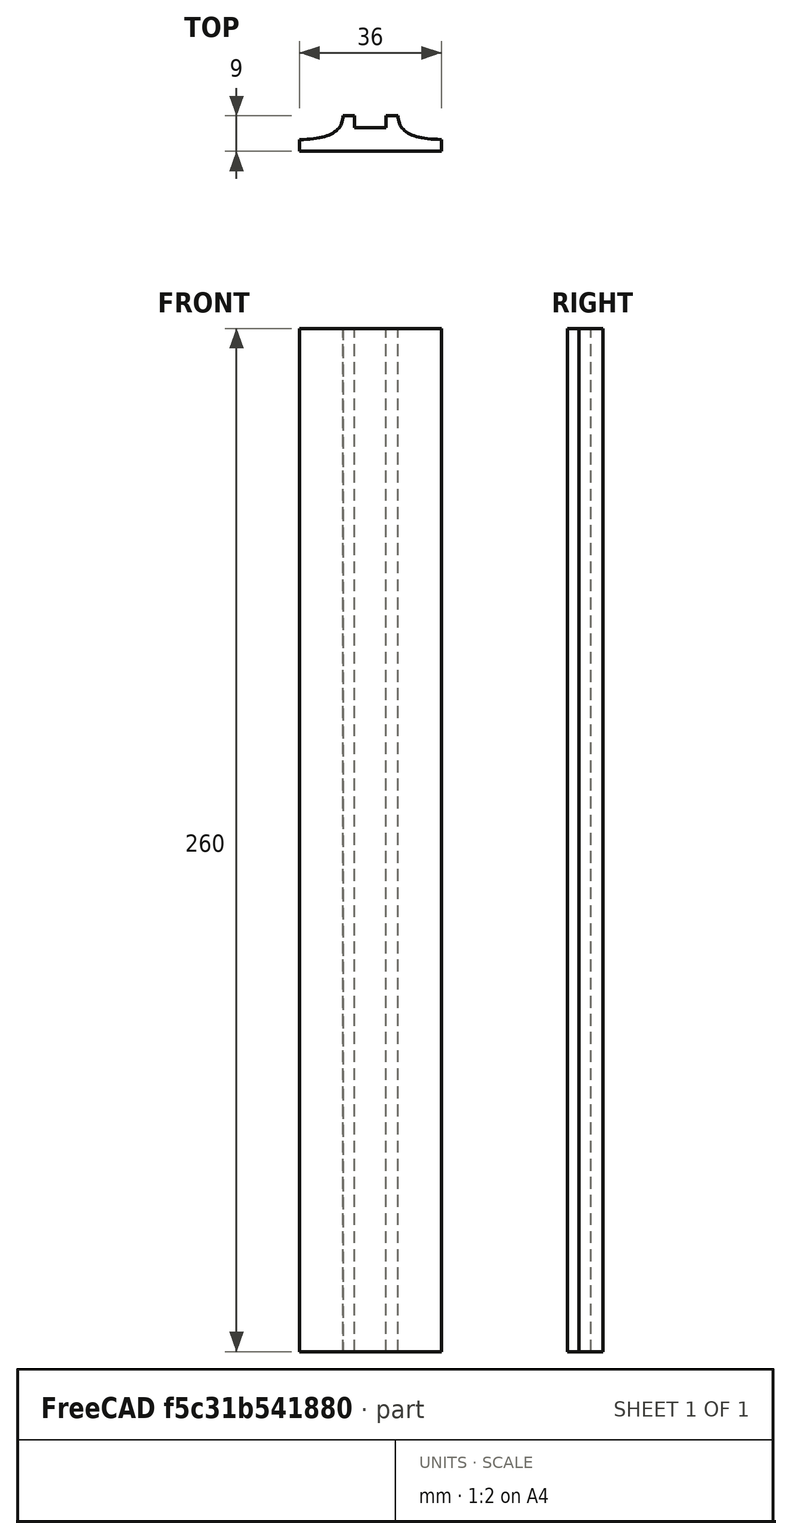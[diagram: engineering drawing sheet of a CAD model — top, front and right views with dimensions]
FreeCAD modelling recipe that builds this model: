
FCSTD DOCUMENT  (FreeCAD 0.19R0.19.2)
Label: laptopStand296.FCStd
License: All rights reserved
LicenseURL: http://en.wikipedia.org/wiki/All_rights_reserved
objects: Sketcher::SketchObject×10, Part::Extrusion×1
note: 11 computed .brp shape members not serialized (recipe doc carries the construction recipe); baked Part::Feature solids carry a one-line shape summary decoded from their .brp

FEATURE [Sketcher::SketchObject] Sketch001  label="legTop"
  FullyConstrained = true
  MapMode = 4
  Placement = pos=(0,0,0) rot=(0.57735,0.57735,0.57735;2.0944rad)
  sketch-geometry (41):
    g0: BSplineCurve PolesCount=3 KnotsCount=2 Degree=2 IsPeriodic=0
    g1: ArcOfCircle CenterX=73.1223 CenterY=-32.291 CenterZ=0 NormalX=0 NormalY=0 NormalZ=1 AngleXU=0 Radius=13 StartAngle=5.92268 EndAngle=9.06428
    g2: ArcOfCircle CenterX=66.7816 CenterY=-49.1439 CenterZ=0 NormalX=0 NormalY=0 NormalZ=1 AngleXU=0 Radius=13 StartAngle=2.78068 EndAngle=5.92131
    g3-g6: Circle x4 (B-spline internal-alignment scaffolding for g7; pole/knot coordinates omitted)
    g7: BSplineCurve PolesCount=4 KnotsCount=2 Degree=3 IsPeriodic=0
    g8: GeomPoint X=28.8094 Y=-19.0875 Z=0
    g9: GeomPoint X=47.0443 Y=-50.4712 Z=0
    g10: Circle CenterX=53.5586 CenterY=-23.2695 CenterZ=0 NormalX=0 NormalY=0 NormalZ=1 AngleXU=0 Radius=3.24518
    g11: LineSegment StartX=17.2232 StartY=-16.0875 StartZ=0 EndX=17.2232 EndY=-19.0875 EndZ=0
    g12: ArcOfCircle CenterX=17.2475 CenterY=-181.166 CenterZ=0 NormalX=0 NormalY=0 NormalZ=1 AngleXU=0 Radius=13 StartAngle=5.92268 EndAngle=7.49361
    g13: ArcOfCircle CenterX=29.5716 CenterY=-148.408 CenterZ=0 NormalX=0 NormalY=0 NormalZ=1 AngleXU=0 Radius=13 StartAngle=4.35228 EndAngle=5.92131
    g14: ArcOfCircle CenterX=35.8967 CenterY=-131.555 CenterZ=0 NormalX=0 NormalY=0 NormalZ=1 AngleXU=0 Radius=13 StartAngle=5.92268 EndAngle=7.49902
    g15: ArcOfCircle CenterX=48.1805 CenterY=-98.7782 CenterZ=0 NormalX=0 NormalY=0 NormalZ=1 AngleXU=0 Radius=13 StartAngle=4.34921 EndAngle=5.92131
    g16: ArcOfCircle CenterX=54.5183 CenterY=-81.9247 CenterZ=0 NormalX=0 NormalY=0 NormalZ=1 AngleXU=0 Radius=13 StartAngle=5.92268 EndAngle=8.70432
    g17: ArcOfCircle CenterX=20.184 CenterY=-217.506 CenterZ=0 NormalX=0 NormalY=0 NormalZ=1 AngleXU=0 Radius=3.81084 StartAngle=1.88136 EndAngle=6.80465
    g18: ArcOfCircle CenterX=36.3663 CenterY=-113.042 CenterZ=0 NormalX=0 NormalY=0 NormalZ=1 AngleXU=0 Radius=3.60555 StartAngle=0.230024 EndAngle=5.3372
    g19: LineSegment StartX=42.6867 StartY=-113.271 StartZ=0 EndX=43.5628 EndY=-110.929 EndZ=0
    g20: ArcOfCircle CenterX=17.7945 CenterY=-162.686 CenterZ=0 NormalX=0 NormalY=0 NormalZ=1 AngleXU=0 Radius=3.60555 StartAngle=0.230024 EndAngle=5.3372
    g21: ArcOfCircle CenterX=49.8795 CenterY=-62.6074 CenterZ=0 NormalX=0 NormalY=0 NormalZ=1 AngleXU=0 Radius=3.84187 StartAngle=4.46973 EndAngle=9.40343
    g22: LineSegment StartX=23.4884 StartY=-215.608 StartZ=0 EndX=94.6579 EndY=-26.1359 EndZ=0
    g23: LineSegment StartX=22.7134 StartY=-166.661 StartZ=0 EndX=21.8316 EndY=-169.001 EndZ=0
    g24: LineSegment StartX=48.061 StartY=-136.14 StartZ=0 EndX=41.7296 EndY=-153.01 EndZ=0
    g25: LineSegment StartX=24.1149 StartY=-162.915 StartZ=0 EndX=24.9906 EndY=-160.574 EndZ=0
    g26: LineSegment StartX=41.2852 StartY=-117.017 StartZ=0 EndX=40.4148 EndY=-119.365 EndZ=0
    g27: LineSegment StartX=48.9563 StartY=-66.3367 StartZ=0 EndX=44.7488 EndY=-73.3482 EndZ=0
    g28: LineSegment StartX=21.3051 StartY=-161.864 StartZ=0 EndX=24.1149 EndY=-162.915 EndZ=0
    g29: LineSegment StartX=19.9036 StartY=-165.61 StartZ=0 EndX=22.7134 EndY=-166.661 EndZ=0
    g30: LineSegment StartX=29.4118 StartY=-185.752 StartZ=0 EndX=19.0195 EndY=-213.878 EndZ=0
    g31: LineSegment StartX=39.8769 StartY=-112.22 StartZ=0 EndX=42.6867 EndY=-113.271 EndZ=0
    g32: LineSegment StartX=38.4753 StartY=-115.966 StartZ=0 EndX=41.2852 EndY=-117.017 EndZ=0
    g33: LineSegment StartX=60.3386 StartY=-103.381 StartZ=0 EndX=66.6827 EndY=-86.5104 EndZ=0
    g34: LineSegment StartX=41.085 StartY=-66.3176 StartZ=0 EndX=46.0385 EndY=-62.5254 EndZ=0
    g35: LineSegment StartX=47.0443 StartY=-50.4712 StartZ=0 EndX=41.085 EndY=-66.3176 EndZ=0
    g36: LineSegment StartX=17.2232 StartY=-16.0875 StartZ=0 EndX=117.223 EndY=-16.0875 EndZ=0
    g37: LineSegment StartX=28.8094 StartY=-19.0875 StartZ=0 EndX=17.2232 EndY=-19.0875 EndZ=0
    g38: LineSegment StartX=117.223 StartY=-16.0875 StartZ=0 EndX=117.223 EndY=-19.0875 EndZ=0
    g39: LineSegment StartX=85.2866 StartY=-36.8766 StartZ=0 EndX=78.9396 EndY=-53.7463 EndZ=0
    g40: LineSegment StartX=60.9579 StartY=-27.7053 StartZ=0 EndX=54.6191 EndY=-44.5532 EndZ=0
  constraints (65):
    c: Block(g0)
    c: Block(g1)
    c: Block(g2)
    c: Weight(g3) = 1
    c: Equal(g3,g4)
    c: Equal(g3,g5)
    c: Equal(g3,g6)
    c: InternalAlignment(g3-g6 -> g7) x4
    c: InternalAlignment(g8,g7)
    c: InternalAlignment(g9,g7)
    c: Block(g10)
    c: Block(g7)
    c: Vertical(g11)
    c: Block(g12)
    c: Block(g13)
    c: Block(g14)
    c: Block(g15)
    c: Block(g16)
    c: Block(g17)
    c: Block(g18)
    c: Block(g19)
    c: Block(g20)
    c: Block(g21)
    c: PointOnObject(g15,g19)
    c: Coincident(g22,g17)
    c: Coincident(g22,g0)
    c: Coincident(g23,g12)
    c: Coincident(g24,g14)
    c: Coincident(g24,g13)
    c: Coincident(g25,g13)
    c: Coincident(g26,g14)
    c: Coincident(g27,g21)
    c: Coincident(g27,g16)
    c: Coincident(g28,g20)
    c: Coincident(g28,g25)
    c: Coincident(g29,g20)
    c: Coincident(g29,g23)
    c: Block(g28)
    c: Block(g29)
    c: Coincident(g30,g12)
    c: Coincident(g30,g17)
    c: Coincident(g31,g18)
    c: Coincident(g31,g19)
    c: Coincident(g32,g18)
    c: Coincident(g32,g26)
    c: Block(g32)
    c: Coincident(g33,g15)
    c: Coincident(g33,g16)
    c: Coincident(g34,g21)
    c: Block(g34)
    c: Coincident(g35,g7)
    c: Coincident(g35,g34)
    c: Coincident(g36,g11)
    c: Horizontal(g36)
    c: Coincident(g37,g7)
    c: Coincident(g37,g11)
    c: Horizontal(g37)
    c: Coincident(g38,g36)
    c: Coincident(g38,g0)
    c: Vertical(g38)
    c: Block(g36)
    c: Coincident(g39,g1)
    c: Coincident(g39,g2)
    c: Coincident(g40,g1)
    c: Coincident(g40,g2)
FEATURE [Sketcher::SketchObject] Sketch002
  FullyConstrained = true
  sketch-geometry (20):
    g0: LineSegment StartX=-2.77179 StartY=-200.304 StartZ=0 EndX=5.22821 EndY=-200.304 EndZ=0
    g1: LineSegment StartX=5.22821 StartY=-200.304 StartZ=0 EndX=5.22821 EndY=-197.304 EndZ=0
    g2: LineSegment StartX=-2.77179 StartY=-200.304 StartZ=0 EndX=-2.77179 EndY=-197.304 EndZ=0
    g3: LineSegment StartX=5.22821 StartY=-197.304 StartZ=0 EndX=8.22821 EndY=-197.304 EndZ=0
    g4: LineSegment StartX=-2.77179 StartY=-197.304 StartZ=0 EndX=-5.77179 EndY=-197.304 EndZ=0
    g5: LineSegment StartX=19.2282 StartY=-203.304 StartZ=0 EndX=19.2282 EndY=-206.304 EndZ=0
    g6: LineSegment StartX=-16.7718 StartY=-203.304 StartZ=0 EndX=-16.7718 EndY=-206.304 EndZ=0
    g7: LineSegment StartX=-16.7718 StartY=-206.304 StartZ=0 EndX=19.2282 EndY=-206.304 EndZ=0
    g8: Circle CenterX=-16.7718 CenterY=-203.304 CenterZ=0 NormalX=0 NormalY=0 NormalZ=1 AngleXU=0 Radius=1
    g9: Circle CenterX=-5.77179 CenterY=-203.304 CenterZ=0 NormalX=0 NormalY=0 NormalZ=1 AngleXU=0 Radius=1
    g10: Circle CenterX=-5.77179 CenterY=-197.304 CenterZ=0 NormalX=0 NormalY=0 NormalZ=1 AngleXU=0 Radius=1
    g11: BSplineCurve PolesCount=3 KnotsCount=2 Degree=2 IsPeriodic=0
    g12: GeomPoint X=-16.7718 Y=-203.304 Z=0
    g13: GeomPoint X=-5.77179 Y=-197.304 Z=0
    g14: Circle CenterX=19.2282 CenterY=-203.304 CenterZ=0 NormalX=0 NormalY=0 NormalZ=1 AngleXU=0 Radius=1
    g15: Circle CenterX=8.22821 CenterY=-203.304 CenterZ=0 NormalX=0 NormalY=0 NormalZ=1 AngleXU=0 Radius=1
    g16: Circle CenterX=8.22821 CenterY=-197.304 CenterZ=0 NormalX=0 NormalY=0 NormalZ=1 AngleXU=0 Radius=1
    g17: BSplineCurve PolesCount=3 KnotsCount=2 Degree=2 IsPeriodic=0
    g18: GeomPoint X=19.2282 Y=-203.304 Z=0
    g19: GeomPoint X=8.22821 Y=-197.304 Z=0
  constraints (41):
    c: Horizontal(g0)
    c: Distance(g0) = 8
    c: Coincident(g1,g0)
    c: Vertical(g1)
    c: Distance(g1) = 3
    c: Coincident(g2,g0)
    c: Vertical(g2)
    c: Distance(g2) = 3
    c: Coincident(g3,g1)
    c: Horizontal(g3)
    c: Distance(g3) = 3
    c: Coincident(g4,g2)
    c: Horizontal(g4)
    c: Distance(g4) = 3
    c: Vertical(g5)
    c: Vertical(g6)
    c: Coincident(g7,g6)
    c: Coincident(g7,g5)
    c: Weight(g8) = 1
    c: Equal(g8,g9)
    c: Equal(g8,g10)
    c: Coincident(g11,g4)
    c: InternalAlignment(g8,g11)
    c: InternalAlignment(g9,g11)
    c: InternalAlignment(g10,g11)
    c: InternalAlignment(g12,g11)
    c: InternalAlignment(g13,g11)
    c: Coincident(g17,g5)
    c: Weight(g14) = 1
    c: Equal(g14,g15)
    c: Equal(g14,g16)
    c: Coincident(g17,g3)
    c: InternalAlignment(g14,g17)
    c: InternalAlignment(g15,g17)
    c: InternalAlignment(g16,g17)
    c: InternalAlignment(g18,g17)
    c: InternalAlignment(g19,g17)
    c: Block(g7)
    c: Block(g17)
    c: Block(g11)
    c: Block(g6)
FEATURE [Part::Extrusion] Extrude003
  Base = -> Sketch002
  Dir = (0,0,1)
  DirMode = 2
  FaceMakerClass = Part::FaceMakerBullseye
  LengthFwd = 260
  LengthRev = 0
  Solid = true
  Symmetric = false
FEATURE [Sketcher::SketchObject] Sketch003  label="original"
  FullyConstrained = false
  sketch-geometry (469):
    g0: LineSegment StartX=-42.9272 StartY=136.221 StartZ=0 EndX=-42.9272 EndY=-103.779 EndZ=0
    g1: LineSegment StartX=407.073 StartY=136.221 StartZ=0 EndX=407.073 EndY=-103.779 EndZ=0
    g2: ArcOfCircle CenterX=-26.9272 CenterY=-83.7794 CenterZ=0 NormalX=0 NormalY=0 NormalZ=1 AngleXU=0 Radius=8 StartAngle=3.14159 EndAngle=6.28319
    g3: ArcOfCircle CenterX=391.073 CenterY=-83.7794 CenterZ=0 NormalX=0 NormalY=0 NormalZ=1 AngleXU=0 Radius=8 StartAngle=3.14159 EndAngle=6.28319
    g4: Circle CenterX=175.022 CenterY=27.0628 CenterZ=0 NormalX=0 NormalY=0 NormalZ=1 AngleXU=0 Radius=1
    g5: Circle CenterX=179.022 CenterY=24.8665 CenterZ=0 NormalX=0 NormalY=0 NormalZ=1 AngleXU=0 Radius=1
    g6: Circle CenterX=179.022 CenterY=27.0628 CenterZ=0 NormalX=0 NormalY=0 NormalZ=1 AngleXU=0 Radius=1
    g7: BSplineCurve PolesCount=3 KnotsCount=2 Degree=2 IsPeriodic=0
    g8: GeomPoint X=175.022 Y=27.0628 Z=0
    g9: GeomPoint X=179.022 Y=27.0628 Z=0
    g10: Circle CenterX=189.124 CenterY=27.0628 CenterZ=0 NormalX=0 NormalY=0 NormalZ=1 AngleXU=0 Radius=1
    g11: Circle CenterX=185.124 CenterY=24.8665 CenterZ=0 NormalX=0 NormalY=0 NormalZ=1 AngleXU=0 Radius=1
    g12: Circle CenterX=185.124 CenterY=27.0628 CenterZ=0 NormalX=0 NormalY=0 NormalZ=1 AngleXU=0 Radius=1
    g13: BSplineCurve PolesCount=3 KnotsCount=2 Degree=2 IsPeriodic=0
    g14: GeomPoint X=189.124 Y=27.0628 Z=0
    g15: GeomPoint X=185.124 Y=27.0628 Z=0
    g16: Circle CenterX=175.022 CenterY=5.37834 CenterZ=0 NormalX=0 NormalY=0 NormalZ=1 AngleXU=0 Radius=1
    g17: Circle CenterX=179.022 CenterY=7.57463 CenterZ=0 NormalX=0 NormalY=0 NormalZ=1 AngleXU=0 Radius=1
    g18: Circle CenterX=179.022 CenterY=5.34704 CenterZ=0 NormalX=0 NormalY=0 NormalZ=1 AngleXU=0 Radius=1
    g19: BSplineCurve PolesCount=3 KnotsCount=2 Degree=2 IsPeriodic=0
    g20: GeomPoint X=175.022 Y=5.37834 Z=0
    g21: GeomPoint X=179.022 Y=5.34704 Z=0
    g22: Circle CenterX=189.124 CenterY=5.37834 CenterZ=0 NormalX=0 NormalY=0 NormalZ=1 AngleXU=0 Radius=1
    g23: Circle CenterX=185.124 CenterY=7.57463 CenterZ=0 NormalX=0 NormalY=0 NormalZ=1 AngleXU=0 Radius=1
    g24: Circle CenterX=185.124 CenterY=5.34704 CenterZ=0 NormalX=0 NormalY=0 NormalZ=1 AngleXU=0 Radius=1
    g25: BSplineCurve PolesCount=3 KnotsCount=2 Degree=2 IsPeriodic=0
    g26: GeomPoint X=189.124 Y=5.37834 Z=0
    g27: GeomPoint X=185.124 Y=5.34704 Z=0
    g28: Circle CenterX=165.871 CenterY=18.1458 CenterZ=0 NormalX=0 NormalY=0 NormalZ=1 AngleXU=0 Radius=1
    g29: Circle CenterX=169.377 CenterY=16.2206 CenterZ=0 NormalX=0 NormalY=0 NormalZ=1 AngleXU=0 Radius=1
    g30: Circle CenterX=165.871 CenterY=14.2956 CenterZ=0 NormalX=0 NormalY=0 NormalZ=1 AngleXU=0 Radius=1
    g31: BSplineCurve PolesCount=3 KnotsCount=2 Degree=2 IsPeriodic=0
    g32: GeomPoint X=165.871 Y=18.1458 Z=0
    g33: GeomPoint X=165.871 Y=14.2956 Z=0
    g34: Circle CenterX=198.275 CenterY=18.1318 CenterZ=0 NormalX=0 NormalY=0 NormalZ=1 AngleXU=0 Radius=1
    g35: Circle CenterX=194.768 CenterY=16.2206 CenterZ=0 NormalX=0 NormalY=0 NormalZ=1 AngleXU=0 Radius=1
    g36: Circle CenterX=198.264 CenterY=14.2963 CenterZ=0 NormalX=0 NormalY=0 NormalZ=1 AngleXU=0 Radius=1
    g37: BSplineCurve PolesCount=3 KnotsCount=2 Degree=2 IsPeriodic=0
    g38: GeomPoint X=198.275 Y=18.1318 Z=0
    g39: GeomPoint X=198.264 Y=14.2963 Z=0
    g40: LineSegment StartX=407.073 StartY=-103.779 StartZ=0 EndX=-42.9272 EndY=-103.779 EndZ=0
    g41: Circle CenterX=125.607 CenterY=54.1951 CenterZ=0 NormalX=0 NormalY=0 NormalZ=1 AngleXU=0 Radius=1
    g42: Circle CenterX=139.632 CenterY=46.4944 CenterZ=0 NormalX=0 NormalY=0 NormalZ=1 AngleXU=0 Radius=1
    g43: Circle CenterX=127.326 CenterY=56.7187 CenterZ=0 NormalX=0 NormalY=0 NormalZ=1 AngleXU=0 Radius=1
    g44: BSplineCurve PolesCount=3 KnotsCount=2 Degree=2 IsPeriodic=0
    g45: GeomPoint X=125.607 Y=54.1951 Z=0
    g46: GeomPoint X=127.326 Y=56.7187 Z=0
    g47: Circle CenterX=236.824 CenterY=56.7187 CenterZ=0 NormalX=0 NormalY=0 NormalZ=1 AngleXU=0 Radius=1
    g48: Circle CenterX=224.513 CenterY=46.4944 CenterZ=0 NormalX=0 NormalY=0 NormalZ=1 AngleXU=0 Radius=1
    g49: Circle CenterX=238.538 CenterY=54.1951 CenterZ=0 NormalX=0 NormalY=0 NormalZ=1 AngleXU=0 Radius=1
    g50: BSplineCurve PolesCount=3 KnotsCount=2 Degree=2 IsPeriodic=0
    g51: GeomPoint X=236.824 Y=56.7187 Z=0
    g52: GeomPoint X=238.538 Y=54.1951 Z=0
    g53: Circle CenterX=238.538 CenterY=-21.7516 CenterZ=0 NormalX=0 NormalY=0 NormalZ=1 AngleXU=0 Radius=1
    g54: Circle CenterX=224.513 CenterY=-14.0532 CenterZ=0 NormalX=0 NormalY=0 NormalZ=1 AngleXU=0 Radius=1
    g55: Circle CenterX=236.584 CenterY=-24.2775 CenterZ=0 NormalX=0 NormalY=0 NormalZ=1 AngleXU=0 Radius=1
    g56: BSplineCurve PolesCount=3 KnotsCount=2 Degree=2 IsPeriodic=0
    g57: GeomPoint X=238.538 Y=-21.7516 Z=0
    g58: GeomPoint X=236.584 Y=-24.2775 Z=0
    g59: Circle CenterX=125.607 CenterY=-21.7539 CenterZ=0 NormalX=0 NormalY=0 NormalZ=1 AngleXU=0 Radius=1
    g60: Circle CenterX=139.632 CenterY=-14.0532 CenterZ=0 NormalX=0 NormalY=0 NormalZ=1 AngleXU=0 Radius=1
    g61: Circle CenterX=127.325 CenterY=-24.2775 CenterZ=0 NormalX=0 NormalY=0 NormalZ=1 AngleXU=0 Radius=1
    g62: BSplineCurve PolesCount=3 KnotsCount=2 Degree=2 IsPeriodic=0
    g63: GeomPoint X=125.607 Y=-21.7539 Z=0
    g64: GeomPoint X=127.325 Y=-24.2775 Z=0
    g65: Circle CenterX=302.996 CenterY=111.695 CenterZ=0 NormalX=0 NormalY=0 NormalZ=1 AngleXU=0 Radius=1
    g66: Circle CenterX=306.073 CenterY=114.251 CenterZ=0 NormalX=0 NormalY=0 NormalZ=1 AngleXU=0 Radius=1
    g67: Circle CenterX=306.073 CenterY=110.251 CenterZ=0 NormalX=0 NormalY=0 NormalZ=1 AngleXU=0 Radius=1
    g68: BSplineCurve PolesCount=3 KnotsCount=2 Degree=2 IsPeriodic=0
    g69: GeomPoint X=302.996 Y=111.695 Z=0
    g70: GeomPoint X=306.073 Y=110.251 Z=0
    g71: Circle CenterX=306.073 CenterY=95.2763 CenterZ=0 NormalX=0 NormalY=0 NormalZ=1 AngleXU=0 Radius=1
    g72: Circle CenterX=306.073 CenterY=91.2763 CenterZ=0 NormalX=0 NormalY=0 NormalZ=1 AngleXU=0 Radius=1
    g73: Circle CenterX=302.567 CenterY=89.3511 CenterZ=0 NormalX=0 NormalY=0 NormalZ=1 AngleXU=0 Radius=1
    g74: BSplineCurve PolesCount=3 KnotsCount=2 Degree=2 IsPeriodic=0
    g75: GeomPoint X=306.073 Y=95.2763 Z=0
    g76: GeomPoint X=302.567 Y=89.3511 Z=0
    g77: LineSegment StartX=306.073 StartY=110.251 StartZ=0 EndX=306.073 EndY=95.2763 EndZ=0
    g78: LineSegment StartX=302.996 StartY=111.695 StartZ=0 EndX=236.824 EndY=56.7187 EndZ=0
    g79: LineSegment StartX=238.538 StartY=54.1951 StartZ=0 EndX=302.567 EndY=89.3511 EndZ=0
    g80: Circle CenterX=61.1496 CenterY=111.695 CenterZ=0 NormalX=0 NormalY=0 NormalZ=1 AngleXU=0 Radius=1
    g81: Circle CenterX=58.0728 CenterY=114.251 CenterZ=0 NormalX=0 NormalY=0 NormalZ=1 AngleXU=0 Radius=1
    g82: Circle CenterX=58.0728 CenterY=110.251 CenterZ=0 NormalX=0 NormalY=0 NormalZ=1 AngleXU=0 Radius=1
    g83: BSplineCurve PolesCount=3 KnotsCount=2 Degree=2 IsPeriodic=0
    g84: GeomPoint X=61.1496 Y=111.695 Z=0
    g85: GeomPoint X=58.0728 Y=110.251 Z=0
    g86: Circle CenterX=61.5791 CenterY=89.3511 CenterZ=0 NormalX=0 NormalY=0 NormalZ=1 AngleXU=0 Radius=1
    g87: Circle CenterX=58.0728 CenterY=91.2763 CenterZ=0 NormalX=0 NormalY=0 NormalZ=1 AngleXU=0 Radius=1
    g88: Circle CenterX=58.0728 CenterY=95.2763 CenterZ=0 NormalX=0 NormalY=0 NormalZ=1 AngleXU=0 Radius=1
    g89: BSplineCurve PolesCount=3 KnotsCount=2 Degree=2 IsPeriodic=0
    g90: GeomPoint X=61.5791 Y=89.3511 Z=0
    g91: GeomPoint X=58.0728 Y=95.2763 Z=0
    g92: LineSegment StartX=58.0728 StartY=110.251 StartZ=0 EndX=58.0728 EndY=95.2763 EndZ=0
    g93: LineSegment StartX=61.1496 StartY=111.695 StartZ=0 EndX=127.326 EndY=56.7187 EndZ=0
    g94: LineSegment StartX=125.607 StartY=54.1951 StartZ=0 EndX=61.5791 EndY=89.3511 EndZ=0
    g95: Circle CenterX=61.5791 CenterY=-56.9099 CenterZ=0 NormalX=0 NormalY=0 NormalZ=1 AngleXU=0 Radius=1
    g96: Circle CenterX=58.0728 CenterY=-58.8351 CenterZ=0 NormalX=0 NormalY=0 NormalZ=1 AngleXU=0 Radius=1
    g97: Circle CenterX=58.0728 CenterY=-62.8351 CenterZ=0 NormalX=0 NormalY=0 NormalZ=1 AngleXU=0 Radius=1
    g98: BSplineCurve PolesCount=3 KnotsCount=2 Degree=2 IsPeriodic=0
    g99: GeomPoint X=61.5791 Y=-56.9099 Z=0
    g100: GeomPoint X=58.0728 Y=-62.8351 Z=0
    g101: Circle CenterX=58.0728 CenterY=-77.8102 CenterZ=0 NormalX=0 NormalY=0 NormalZ=1 AngleXU=0 Radius=1
    g102: Circle CenterX=58.0728 CenterY=-81.8102 CenterZ=0 NormalX=0 NormalY=0 NormalZ=1 AngleXU=0 Radius=1
    g103: Circle CenterX=61.1496 CenterY=-79.2541 CenterZ=0 NormalX=0 NormalY=0 NormalZ=1 AngleXU=0 Radius=1
    g104: BSplineCurve PolesCount=3 KnotsCount=2 Degree=2 IsPeriodic=0
    g105: GeomPoint X=58.0728 Y=-77.8102 Z=0
    g106: GeomPoint X=61.1496 Y=-79.2541 Z=0
    g107: LineSegment StartX=58.0728 StartY=-62.8351 StartZ=0 EndX=58.0728 EndY=-77.8102 EndZ=0
    g108: LineSegment StartX=61.1496 StartY=-79.2541 StartZ=0 EndX=127.325 EndY=-24.2775 EndZ=0
    g109: LineSegment StartX=125.607 StartY=-21.7539 StartZ=0 EndX=61.5791 EndY=-56.9099 EndZ=0
    g110: Circle CenterX=302.567 CenterY=-56.9099 CenterZ=0 NormalX=0 NormalY=0 NormalZ=1 AngleXU=0 Radius=1
    g111: Circle CenterX=306.073 CenterY=-58.8351 CenterZ=0 NormalX=0 NormalY=0 NormalZ=1 AngleXU=0 Radius=1
    g112: Circle CenterX=306.073 CenterY=-62.8351 CenterZ=0 NormalX=0 NormalY=0 NormalZ=1 AngleXU=0 Radius=1
    g113: BSplineCurve PolesCount=3 KnotsCount=2 Degree=2 IsPeriodic=0
    g114: GeomPoint X=302.567 Y=-56.9099 Z=0
    g115: GeomPoint X=306.073 Y=-62.8351 Z=0
    g116: Circle CenterX=302.996 CenterY=-79.2541 CenterZ=0 NormalX=0 NormalY=0 NormalZ=1 AngleXU=0 Radius=1
    g117: Circle CenterX=306.073 CenterY=-81.8102 CenterZ=0 NormalX=0 NormalY=0 NormalZ=1 AngleXU=0 Radius=1
    g118: Circle CenterX=306.073 CenterY=-77.8102 CenterZ=0 NormalX=0 NormalY=0 NormalZ=1 AngleXU=0 Radius=1
    g119: BSplineCurve PolesCount=3 KnotsCount=2 Degree=2 IsPeriodic=0
    g120: GeomPoint X=302.996 Y=-79.2541 Z=0
    g121: GeomPoint X=306.073 Y=-77.8102 Z=0
    g122: LineSegment StartX=306.073 StartY=-62.8351 StartZ=0 EndX=306.073 EndY=-77.8102 EndZ=0
    g123: LineSegment StartX=302.996 StartY=-79.2541 StartZ=0 EndX=236.584 EndY=-24.2775 EndZ=0
    g124: LineSegment StartX=238.538 StartY=-21.7516 StartZ=0 EndX=302.567 EndY=-56.9099 EndZ=0
    g125: Circle CenterX=61.6457 CenterY=-88.8112 CenterZ=0 NormalX=0 NormalY=0 NormalZ=1 AngleXU=0 Radius=1
    g126: Circle CenterX=58.0728 CenterY=-91.7794 CenterZ=0 NormalX=0 NormalY=0 NormalZ=1 AngleXU=0 Radius=1
    g127: Circle CenterX=63.9135 CenterY=-91.7791 CenterZ=0 NormalX=0 NormalY=0 NormalZ=1 AngleXU=0 Radius=1
    g128: BSplineCurve PolesCount=3 KnotsCount=2 Degree=2 IsPeriodic=0
    g129: GeomPoint X=61.6457 Y=-88.8112 Z=0
    g130: GeomPoint X=63.9135 Y=-91.7791 Z=0
    g131: Circle CenterX=179.022 CenterY=-85.8163 CenterZ=0 NormalX=0 NormalY=0 NormalZ=1 AngleXU=0 Radius=1
    g132: Circle CenterX=179.022 CenterY=-91.7794 CenterZ=0 NormalX=0 NormalY=0 NormalZ=1 AngleXU=0 Radius=1
    g133: Circle CenterX=171.895 CenterY=-91.7791 CenterZ=0 NormalX=0 NormalY=0 NormalZ=1 AngleXU=0 Radius=1
    g134: BSplineCurve PolesCount=3 KnotsCount=2 Degree=2 IsPeriodic=0
    g135: GeomPoint X=179.022 Y=-85.8163 Z=0
    g136: GeomPoint X=171.895 Y=-91.7791 Z=0
    g137: Circle CenterX=185.124 CenterY=-86.2028 CenterZ=0 NormalX=0 NormalY=0 NormalZ=1 AngleXU=0 Radius=1
    g138: Circle CenterX=185.124 CenterY=-91.7794 CenterZ=0 NormalX=0 NormalY=0 NormalZ=1 AngleXU=0 Radius=1
    g139: Circle CenterX=191.747 CenterY=-91.7794 CenterZ=0 NormalX=0 NormalY=0 NormalZ=1 AngleXU=0 Radius=1
    g140: BSplineCurve PolesCount=3 KnotsCount=2 Degree=2 IsPeriodic=0
    g141: GeomPoint X=185.124 Y=-86.2028 Z=0
    g142: GeomPoint X=191.747 Y=-91.7794 Z=0
    g143: Circle CenterX=299.888 CenterY=-86.6413 CenterZ=0 NormalX=0 NormalY=0 NormalZ=1 AngleXU=0 Radius=1
    g144: Circle CenterX=306.073 CenterY=-91.7794 CenterZ=0 NormalX=0 NormalY=0 NormalZ=1 AngleXU=0 Radius=1
    g145: Circle CenterX=298.776 CenterY=-91.7794 CenterZ=0 NormalX=0 NormalY=0 NormalZ=1 AngleXU=0 Radius=1
    g146: BSplineCurve PolesCount=3 KnotsCount=2 Degree=2 IsPeriodic=0
    g147: GeomPoint X=299.888 Y=-86.6413 Z=0
    g148: GeomPoint X=298.776 Y=-91.7794 Z=0
    g149: LineSegment StartX=189.124 StartY=5.37834 StartZ=0 EndX=299.888 EndY=-86.6413 EndZ=0
    g150: LineSegment StartX=298.776 StartY=-91.7794 StartZ=0 EndX=191.747 EndY=-91.7794 EndZ=0
    g151: LineSegment StartX=185.124 StartY=-86.2028 StartZ=0 EndX=185.124 EndY=5.34704 EndZ=0
    g152: LineSegment StartX=179.022 StartY=5.34704 StartZ=0 EndX=179.022 EndY=-85.8163 EndZ=0
    g153: LineSegment StartX=171.895 StartY=-91.7791 StartZ=0 EndX=63.9135 EndY=-91.7791 EndZ=0
    g154: LineSegment StartX=61.6457 StartY=-88.8112 StartZ=0 EndX=175.022 EndY=5.37834 EndZ=0
    g155: Circle CenterX=302.073 CenterY=124.221 CenterZ=0 NormalX=0 NormalY=0 NormalZ=1 AngleXU=0 Radius=1
    g156: Circle CenterX=306.073 CenterY=124.221 CenterZ=0 NormalX=0 NormalY=0 NormalZ=1 AngleXU=0 Radius=1
    g157: Circle CenterX=302.996 CenterY=121.665 CenterZ=0 NormalX=0 NormalY=0 NormalZ=1 AngleXU=0 Radius=1
    g158: BSplineCurve PolesCount=3 KnotsCount=2 Degree=2 IsPeriodic=0
    g159: GeomPoint X=302.073 Y=124.221 Z=0
    g160: GeomPoint X=302.996 Y=121.665 Z=0
    g161: Circle CenterX=189.124 CenterY=124.221 CenterZ=0 NormalX=0 NormalY=0 NormalZ=1 AngleXU=0 Radius=1
    g162: Circle CenterX=185.124 CenterY=124.221 CenterZ=0 NormalX=0 NormalY=0 NormalZ=1 AngleXU=0 Radius=1
    g163: Circle CenterX=185.124 CenterY=120.221 CenterZ=0 NormalX=0 NormalY=0 NormalZ=1 AngleXU=0 Radius=1
    g164: BSplineCurve PolesCount=3 KnotsCount=2 Degree=2 IsPeriodic=0
    g165: GeomPoint X=189.124 Y=124.221 Z=0
    g166: GeomPoint X=185.124 Y=120.221 Z=0
    g167: Circle CenterX=175.022 CenterY=124.221 CenterZ=0 NormalX=0 NormalY=0 NormalZ=1 AngleXU=0 Radius=1
    g168: Circle CenterX=179.022 CenterY=124.221 CenterZ=0 NormalX=0 NormalY=0 NormalZ=1 AngleXU=0 Radius=1
    g169: Circle CenterX=179.022 CenterY=120.221 CenterZ=0 NormalX=0 NormalY=0 NormalZ=1 AngleXU=0 Radius=1
    g170: BSplineCurve PolesCount=3 KnotsCount=2 Degree=2 IsPeriodic=0
    g171: GeomPoint X=175.022 Y=124.221 Z=0
    g172: GeomPoint X=179.022 Y=120.221 Z=0
    g173: Circle CenterX=62.0728 CenterY=124.221 CenterZ=0 NormalX=0 NormalY=0 NormalZ=1 AngleXU=0 Radius=1
    g174: Circle CenterX=58.0728 CenterY=124.221 CenterZ=0 NormalX=0 NormalY=0 NormalZ=1 AngleXU=0 Radius=1
    g175: Circle CenterX=61.1496 CenterY=121.665 CenterZ=0 NormalX=0 NormalY=0 NormalZ=1 AngleXU=0 Radius=1
    g176: BSplineCurve PolesCount=3 KnotsCount=2 Degree=2 IsPeriodic=0
    g177: GeomPoint X=62.0728 Y=124.221 Z=0
    g178: GeomPoint X=61.1496 Y=121.665 Z=0
    g179: LineSegment StartX=179.022 StartY=120.221 StartZ=0 EndX=179.022 EndY=27.0628 EndZ=0
    g180: LineSegment StartX=185.124 StartY=27.0628 StartZ=0 EndX=185.124 EndY=120.221 EndZ=0
    g181: LineSegment StartX=302.996 StartY=121.665 StartZ=0 EndX=189.124 EndY=27.0628 EndZ=0
    g182: LineSegment StartX=175.022 StartY=27.0628 StartZ=0 EndX=61.1496 EndY=121.665 EndZ=0
    g183: Circle CenterX=61.5791 CenterY=75.4095 CenterZ=0 NormalX=0 NormalY=0 NormalZ=1 AngleXU=0 Radius=1
    g184: Circle CenterX=58.0728 CenterY=77.3346 CenterZ=0 NormalX=0 NormalY=0 NormalZ=1 AngleXU=0 Radius=1
    g185: Circle CenterX=58.0728 CenterY=73.3346 CenterZ=0 NormalX=0 NormalY=0 NormalZ=1 AngleXU=0 Radius=1
    g186: BSplineCurve PolesCount=3 KnotsCount=2 Degree=2 IsPeriodic=0
    g187: GeomPoint X=61.5791 Y=75.4095 Z=0
    g188: GeomPoint X=58.0728 Y=73.3346 Z=0
    g189: Circle CenterX=58.0728 CenterY=-40.8935 CenterZ=0 NormalX=0 NormalY=0 NormalZ=1 AngleXU=0 Radius=1
    g190: Circle CenterX=58.0728 CenterY=-44.8935 CenterZ=0 NormalX=0 NormalY=0 NormalZ=1 AngleXU=0 Radius=1
    g191: Circle CenterX=61.5791 CenterY=-42.9683 CenterZ=0 NormalX=0 NormalY=0 NormalZ=1 AngleXU=0 Radius=1
    g192: BSplineCurve PolesCount=3 KnotsCount=2 Degree=2 IsPeriodic=0
    g193: GeomPoint X=58.0728 Y=-40.8935 Z=0
    g194: GeomPoint X=61.5791 Y=-42.9683 Z=0
    g195: LineSegment StartX=61.5791 StartY=-42.9683 StartZ=0 EndX=165.871 EndY=14.2956 EndZ=0
    g196: LineSegment StartX=165.871 StartY=18.1458 StartZ=0 EndX=61.5791 EndY=75.4095 EndZ=0
    g197: LineSegment StartX=58.0728 StartY=73.3346 StartZ=0 EndX=58.0728 EndY=-40.8935 EndZ=0
    g198: Circle CenterX=302.567 CenterY=-42.9683 CenterZ=0 NormalX=0 NormalY=0 NormalZ=1 AngleXU=0 Radius=1
    g199: Circle CenterX=306.073 CenterY=-44.8935 CenterZ=0 NormalX=0 NormalY=0 NormalZ=1 AngleXU=0 Radius=1
    g200: Circle CenterX=306.073 CenterY=-40.8935 CenterZ=0 NormalX=0 NormalY=0 NormalZ=1 AngleXU=0 Radius=1
    g201: BSplineCurve PolesCount=3 KnotsCount=2 Degree=2 IsPeriodic=0
    g202: GeomPoint X=302.567 Y=-42.9683 Z=0
    g203: GeomPoint X=306.073 Y=-40.8935 Z=0
    g204: Circle CenterX=306.073 CenterY=73.3346 CenterZ=0 NormalX=0 NormalY=0 NormalZ=1 AngleXU=0 Radius=1
    g205: Circle CenterX=306.073 CenterY=77.3346 CenterZ=0 NormalX=0 NormalY=0 NormalZ=1 AngleXU=0 Radius=1
    g206: Circle CenterX=302.535 CenterY=75.4095 CenterZ=0 NormalX=0 NormalY=0 NormalZ=1 AngleXU=0 Radius=1
    g207: BSplineCurve PolesCount=3 KnotsCount=2 Degree=2 IsPeriodic=0
    g208: GeomPoint X=306.073 Y=73.3346 Z=0
    g209: GeomPoint X=302.535 Y=75.4095 Z=0
    g210: LineSegment StartX=302.567 StartY=-42.9683 StartZ=0 EndX=198.264 EndY=14.2963 EndZ=0
    g211: LineSegment StartX=198.275 StartY=18.1318 StartZ=0 EndX=302.535 EndY=75.4095 EndZ=0
    g212: LineSegment StartX=306.073 StartY=73.3346 StartZ=0 EndX=306.073 EndY=-40.8935 EndZ=0
    g213: LineSegment StartX=322.073 StartY=105.865 StartZ=0 EndX=328.643 EndY=105.865 EndZ=0
    g214: LineSegment StartX=318.073 StartY=120.221 StartZ=0 EndX=318.073 EndY=109.865 EndZ=0
    g215: LineSegment StartX=336.157 StartY=107.779 StartZ=0 EndX=362.567 EndY=122.294 EndZ=0
    g216: Circle CenterX=362.073 CenterY=124.221 CenterZ=0 NormalX=0 NormalY=0 NormalZ=1 AngleXU=0 Radius=1
    g217: Circle CenterX=366.073 CenterY=124.221 CenterZ=0 NormalX=0 NormalY=0 NormalZ=1 AngleXU=0 Radius=1
    g218: Circle CenterX=362.567 CenterY=122.294 CenterZ=0 NormalX=0 NormalY=0 NormalZ=1 AngleXU=0 Radius=1
    g219: BSplineCurve PolesCount=3 KnotsCount=2 Degree=2 IsPeriodic=0
    g220: GeomPoint X=362.073 Y=124.221 Z=0
    g221: GeomPoint X=362.567 Y=122.294 Z=0
    g222: Circle CenterX=322.073 CenterY=124.221 CenterZ=0 NormalX=0 NormalY=0 NormalZ=1 AngleXU=0 Radius=1
    g223: Circle CenterX=318.073 CenterY=124.221 CenterZ=0 NormalX=0 NormalY=0 NormalZ=1 AngleXU=0 Radius=1
    g224: Circle CenterX=318.073 CenterY=120.221 CenterZ=0 NormalX=0 NormalY=0 NormalZ=1 AngleXU=0 Radius=1
    g225: BSplineCurve PolesCount=3 KnotsCount=2 Degree=2 IsPeriodic=0
    g226: GeomPoint X=322.073 Y=124.221 Z=0
    g227: GeomPoint X=318.073 Y=120.221 Z=0
    g228: Circle CenterX=322.073 CenterY=105.865 CenterZ=0 NormalX=0 NormalY=0 NormalZ=1 AngleXU=0 Radius=1
    g229: Circle CenterX=318.073 CenterY=105.865 CenterZ=0 NormalX=0 NormalY=0 NormalZ=1 AngleXU=0 Radius=1
    g230: Circle CenterX=318.073 CenterY=109.865 CenterZ=0 NormalX=0 NormalY=0 NormalZ=1 AngleXU=0 Radius=1
    g231: BSplineCurve PolesCount=3 KnotsCount=2 Degree=2 IsPeriodic=0
    g232: GeomPoint X=322.073 Y=105.865 Z=0
    g233: GeomPoint X=318.073 Y=109.865 Z=0
    g234: Circle CenterX=336.157 CenterY=107.779 CenterZ=0 NormalX=0 NormalY=0 NormalZ=1 AngleXU=0 Radius=1
    g235: Circle CenterX=332.651 CenterY=105.853 CenterZ=0 NormalX=0 NormalY=0 NormalZ=1 AngleXU=0 Radius=1
    g236: Circle CenterX=328.643 CenterY=105.865 CenterZ=0 NormalX=0 NormalY=0 NormalZ=1 AngleXU=0 Radius=1
    g237: BSplineCurve PolesCount=3 KnotsCount=2 Degree=2 IsPeriodic=0
    g238: GeomPoint X=336.157 Y=107.779 Z=0
    g239: GeomPoint X=328.643 Y=105.865 Z=0
    g240: LineSegment StartX=322.073 StartY=124.221 StartZ=0 EndX=362.073 EndY=124.221 EndZ=0
    g241: Circle CenterX=371.567 CenterY=-80.8644 CenterZ=0 NormalX=0 NormalY=0 NormalZ=1 AngleXU=0 Radius=1
    g242: Circle CenterX=375.073 CenterY=-82.7896 CenterZ=0 NormalX=0 NormalY=0 NormalZ=1 AngleXU=0 Radius=1
    g243: Circle CenterX=375.073 CenterY=-78.7896 CenterZ=0 NormalX=0 NormalY=0 NormalZ=1 AngleXU=0 Radius=1
    g244: BSplineCurve PolesCount=3 KnotsCount=2 Degree=2 IsPeriodic=0
    g245: GeomPoint X=371.567 Y=-80.8644 Z=0
    g246: GeomPoint X=375.073 Y=-78.7896 Z=0
    g247: Circle CenterX=321.579 CenterY=-53.4075 CenterZ=0 NormalX=0 NormalY=0 NormalZ=1 AngleXU=0 Radius=1
    g248: Circle CenterX=318.073 CenterY=-51.4823 CenterZ=0 NormalX=0 NormalY=0 NormalZ=1 AngleXU=0 Radius=1
    g249: Circle CenterX=318.073 CenterY=-47.4805 CenterZ=0 NormalX=0 NormalY=0 NormalZ=1 AngleXU=0 Radius=1
    g250: BSplineCurve PolesCount=3 KnotsCount=2 Degree=2 IsPeriodic=0
    g251: GeomPoint X=321.579 Y=-53.4075 Z=0
    g252: GeomPoint X=318.073 Y=-47.4805 Z=0
    g253: LineSegment StartX=371.567 StartY=-80.8644 StartZ=0 EndX=321.579 EndY=-53.4075 EndZ=0
    g254: Circle CenterX=321.579 CenterY=-67.3492 CenterZ=0 NormalX=0 NormalY=0 NormalZ=1 AngleXU=0 Radius=1
    g255: Circle CenterX=318.073 CenterY=-65.424 CenterZ=0 NormalX=0 NormalY=0 NormalZ=1 AngleXU=0 Radius=1
    g256: Circle CenterX=318.073 CenterY=-69.424 CenterZ=0 NormalX=0 NormalY=0 NormalZ=1 AngleXU=0 Radius=1
    g257: BSplineCurve PolesCount=3 KnotsCount=2 Degree=2 IsPeriodic=0
    g258: GeomPoint X=321.579 Y=-67.3492 Z=0
    g259: GeomPoint X=318.073 Y=-69.424 Z=0
    g260: Circle CenterX=362.567 CenterY=-89.8542 CenterZ=0 NormalX=0 NormalY=0 NormalZ=1 AngleXU=0 Radius=1
    g261: Circle CenterX=366.073 CenterY=-91.7794 CenterZ=0 NormalX=0 NormalY=0 NormalZ=1 AngleXU=0 Radius=1
    g262: Circle CenterX=362.073 CenterY=-91.7794 CenterZ=0 NormalX=0 NormalY=0 NormalZ=1 AngleXU=0 Radius=1
    g263: BSplineCurve PolesCount=3 KnotsCount=2 Degree=2 IsPeriodic=0
    g264: GeomPoint X=362.567 Y=-89.8542 Z=0
    g265: GeomPoint X=362.073 Y=-91.7794 Z=0
    g266: Circle CenterX=322.073 CenterY=-91.7794 CenterZ=0 NormalX=0 NormalY=0 NormalZ=1 AngleXU=0 Radius=1
    g267: Circle CenterX=318.073 CenterY=-91.7794 CenterZ=0 NormalX=0 NormalY=0 NormalZ=1 AngleXU=0 Radius=1
    g268: Circle CenterX=318.073 CenterY=-87.7794 CenterZ=0 NormalX=0 NormalY=0 NormalZ=1 AngleXU=0 Radius=1
    g269: BSplineCurve PolesCount=3 KnotsCount=2 Degree=2 IsPeriodic=0
    g270: GeomPoint X=322.073 Y=-91.7794 Z=0
    g271: GeomPoint X=318.073 Y=-87.7794 Z=0
    g272: LineSegment StartX=362.567 StartY=-89.8542 StartZ=0 EndX=321.579 EndY=-67.3492 EndZ=0
    g273: LineSegment StartX=318.073 StartY=-69.424 StartZ=0 EndX=318.073 EndY=-87.7794 EndZ=0
    g274: LineSegment StartX=322.073 StartY=-91.7794 StartZ=0 EndX=362.073 EndY=-91.7794 EndZ=0
    g275: Circle CenterX=2.07281 CenterY=124.221 CenterZ=0 NormalX=0 NormalY=0 NormalZ=1 AngleXU=0 Radius=1
    g276: Circle CenterX=1.57905 CenterY=122.295 CenterZ=0 NormalX=0 NormalY=0 NormalZ=1 AngleXU=0 Radius=1
    g277: BSplineCurve PolesCount=3 KnotsCount=2 Degree=2 IsPeriodic=0
    g278: GeomPoint X=2.07281 Y=124.221 Z=0
    g279: GeomPoint X=1.57905 Y=122.295 Z=0
    g280: Circle CenterX=42.0728 CenterY=124.221 CenterZ=0 NormalX=0 NormalY=0 NormalZ=1 AngleXU=0 Radius=1
    g281: Circle CenterX=46.0728 CenterY=124.221 CenterZ=0 NormalX=0 NormalY=0 NormalZ=1 AngleXU=0 Radius=1
    g282: Circle CenterX=46.0728 CenterY=120.221 CenterZ=0 NormalX=0 NormalY=0 NormalZ=1 AngleXU=0 Radius=1
    g283: BSplineCurve PolesCount=3 KnotsCount=2 Degree=2 IsPeriodic=0
    g284: GeomPoint X=42.0728 Y=124.221 Z=0
    g285: GeomPoint X=46.0728 Y=120.221 Z=0
    g286: Circle CenterX=46.0728 CenterY=109.865 CenterZ=0 NormalX=0 NormalY=0 NormalZ=1 AngleXU=0 Radius=1
    g287: Circle CenterX=46.0728 CenterY=105.865 CenterZ=0 NormalX=0 NormalY=0 NormalZ=1 AngleXU=0 Radius=1
    g288: Circle CenterX=42.0728 CenterY=105.865 CenterZ=0 NormalX=0 NormalY=0 NormalZ=1 AngleXU=0 Radius=1
    g289: BSplineCurve PolesCount=3 KnotsCount=2 Degree=2 IsPeriodic=0
    g290: GeomPoint X=46.0728 Y=109.865 Z=0
    g291: GeomPoint X=42.0728 Y=105.865 Z=0
    g292: Circle CenterX=35.5028 CenterY=105.865 CenterZ=0 NormalX=0 NormalY=0 NormalZ=1 AngleXU=0 Radius=1
    g293: Circle CenterX=31.5028 CenterY=105.865 CenterZ=0 NormalX=0 NormalY=0 NormalZ=1 AngleXU=0 Radius=1
    g294: Circle CenterX=27.9965 CenterY=107.79 CenterZ=0 NormalX=0 NormalY=0 NormalZ=1 AngleXU=0 Radius=1
    g295: BSplineCurve PolesCount=3 KnotsCount=2 Degree=2 IsPeriodic=0
    g296: GeomPoint X=35.5028 Y=105.865 Z=0
    g297: GeomPoint X=27.9965 Y=107.79 Z=0
    g298: LineSegment StartX=2.07281 StartY=124.221 StartZ=0 EndX=42.0728 EndY=124.221 EndZ=0
    g299: LineSegment StartX=46.0728 StartY=120.221 StartZ=0 EndX=46.0728 EndY=109.865 EndZ=0
    g300: LineSegment StartX=42.0728 StartY=105.865 StartZ=0 EndX=35.5028 EndY=105.865 EndZ=0
    g301: LineSegment StartX=27.9965 StartY=107.79 StartZ=0 EndX=1.57905 EndY=122.295 EndZ=0
    g302: Circle CenterX=42.5666 CenterY=-67.3492 CenterZ=0 NormalX=0 NormalY=0 NormalZ=1 AngleXU=0 Radius=1
    g303: Circle CenterX=46.0728 CenterY=-65.424 CenterZ=0 NormalX=0 NormalY=0 NormalZ=1 AngleXU=0 Radius=1
    g304: Circle CenterX=46.0728 CenterY=-69.424 CenterZ=0 NormalX=0 NormalY=0 NormalZ=1 AngleXU=0 Radius=1
    g305: BSplineCurve PolesCount=3 KnotsCount=2 Degree=2 IsPeriodic=0
    g306: GeomPoint X=42.5666 Y=-67.3492 Z=0
    g307: GeomPoint X=46.0728 Y=-69.424 Z=0
    g308: Circle CenterX=46.0728 CenterY=-87.7794 CenterZ=0 NormalX=0 NormalY=0 NormalZ=1 AngleXU=0 Radius=1
    g309: Circle CenterX=46.0728 CenterY=-91.7794 CenterZ=0 NormalX=0 NormalY=0 NormalZ=1 AngleXU=0 Radius=1
    g310: Circle CenterX=42.0728 CenterY=-91.7794 CenterZ=0 NormalX=0 NormalY=0 NormalZ=1 AngleXU=0 Radius=1
    g311: BSplineCurve PolesCount=3 KnotsCount=2 Degree=2 IsPeriodic=0
    g312: GeomPoint X=46.0728 Y=-87.7794 Z=0
    g313: GeomPoint X=42.0728 Y=-91.7794 Z=0
    g314: Circle CenterX=2.07281 CenterY=-91.7794 CenterZ=0 NormalX=0 NormalY=0 NormalZ=1 AngleXU=0 Radius=1
    g315: Circle CenterX=-1.92719 CenterY=-91.7794 CenterZ=0 NormalX=0 NormalY=0 NormalZ=1 AngleXU=0 Radius=1
    g316: Circle CenterX=1.57905 CenterY=-89.8542 CenterZ=0 NormalX=0 NormalY=0 NormalZ=1 AngleXU=0 Radius=1
    g317: BSplineCurve PolesCount=3 KnotsCount=2 Degree=2 IsPeriodic=0
    g318: GeomPoint X=2.07281 Y=-91.7794 Z=0
    g319: GeomPoint X=1.57905 Y=-89.8542 Z=0
    g320: LineSegment StartX=2.07281 StartY=-91.7794 StartZ=0 EndX=42.0728 EndY=-91.7794 EndZ=0
    g321: LineSegment StartX=46.0728 StartY=-87.7794 StartZ=0 EndX=46.0728 EndY=-69.424 EndZ=0
    g322: LineSegment StartX=42.5666 StartY=-67.3492 StartZ=0 EndX=1.57905 EndY=-89.8542 EndZ=0
    g323: Circle CenterX=322.073 CenterY=76.4095 CenterZ=0 NormalX=0 NormalY=0 NormalZ=1 AngleXU=0 Radius=4
    g324: BSplineCurve PolesCount=3 KnotsCount=2 Degree=2 IsPeriodic=0
    g325: GeomPoint X=318.073 Y=72.4095 Z=0
    g326: GeomPoint X=322.073 Y=76.4095 Z=0
    g327: Circle CenterX=375.073 CenterY=72.4095 CenterZ=0 NormalX=0 NormalY=0 NormalZ=1 AngleXU=0 Radius=1
    g328: Circle CenterX=375.073 CenterY=76.4095 CenterZ=0 NormalX=0 NormalY=0 NormalZ=1 AngleXU=0 Radius=1
    g329: Circle CenterX=371.073 CenterY=76.4095 CenterZ=0 NormalX=0 NormalY=0 NormalZ=1 AngleXU=0 Radius=1
    g330: BSplineCurve PolesCount=3 KnotsCount=2 Degree=2 IsPeriodic=0
    g331: GeomPoint X=375.073 Y=72.4095 Z=0
    g332: GeomPoint X=371.073 Y=76.4095 Z=0
    g333: LineSegment StartX=322.073 StartY=76.4095 StartZ=0 EndX=371.073 EndY=76.4095 EndZ=0
    g334: LineSegment StartX=318.073 StartY=72.4095 StartZ=0 EndX=318.073 EndY=-47.4805 EndZ=0
    g335: LineSegment StartX=375.073 StartY=72.4095 StartZ=0 EndX=375.073 EndY=-78.7896 EndZ=0
    g336: ArcOfCircle CenterX=-26.9272 CenterY=22.1087 CenterZ=0 NormalX=0 NormalY=0 NormalZ=1 AngleXU=0 Radius=4 StartAngle=5e-16 EndAngle=3.14159
    g337: LineSegment StartX=-22.9272 StartY=22.1087 StartZ=0 EndX=-18.9272 EndY=-83.7794 EndZ=0
    g338: LineSegment StartX=-34.9272 StartY=-83.7794 StartZ=0 EndX=-30.9272 EndY=22.1087 EndZ=0
    g339: ArcOfCircle CenterX=391.073 CenterY=22.1087 CenterZ=0 NormalX=0 NormalY=0 NormalZ=1 AngleXU=0 Radius=4 StartAngle=0 EndAngle=3.14159
    g340: LineSegment StartX=387.073 StartY=22.1087 StartZ=0 EndX=383.073 EndY=-83.7794 EndZ=0
    g341: LineSegment StartX=395.073 StartY=22.1087 StartZ=0 EndX=399.073 EndY=-83.7794 EndZ=0
    g342: Circle CenterX=-10.9272 CenterY=-78.7794 CenterZ=0 NormalX=0 NormalY=0 NormalZ=1 AngleXU=0 Radius=1
    g343: Circle CenterX=-10.9272 CenterY=-82.7794 CenterZ=0 NormalX=0 NormalY=0 NormalZ=1 AngleXU=0 Radius=1
    g344: Circle CenterX=-7.42095 CenterY=-80.8542 CenterZ=0 NormalX=0 NormalY=0 NormalZ=1 AngleXU=0 Radius=1
    g345: BSplineCurve PolesCount=3 KnotsCount=2 Degree=2 IsPeriodic=0
    g346: GeomPoint X=-10.9272 Y=-78.7794 Z=0
    g347: GeomPoint X=-7.42095 Y=-80.8542 Z=0
    g348: Circle CenterX=42.5666 CenterY=-53.4075 CenterZ=0 NormalX=0 NormalY=0 NormalZ=1 AngleXU=0 Radius=1
    g349: Circle CenterX=46.0728 CenterY=-51.4823 CenterZ=0 NormalX=0 NormalY=0 NormalZ=1 AngleXU=0 Radius=1
    g350: Circle CenterX=46.0728 CenterY=-47.4823 CenterZ=0 NormalX=0 NormalY=0 NormalZ=1 AngleXU=0 Radius=1
    g351: BSplineCurve PolesCount=3 KnotsCount=2 Degree=2 IsPeriodic=0
    g352: GeomPoint X=42.5666 Y=-53.4075 Z=0
    g353: GeomPoint X=46.0728 Y=-47.4823 Z=0
    g354: Circle CenterX=46.0728 CenterY=72.4095 CenterZ=0 NormalX=0 NormalY=0 NormalZ=1 AngleXU=0 Radius=1
    g355: Circle CenterX=46.0728 CenterY=76.4095 CenterZ=0 NormalX=0 NormalY=0 NormalZ=1 AngleXU=0 Radius=1
    g356: Circle CenterX=42.0728 CenterY=76.4095 CenterZ=0 NormalX=0 NormalY=0 NormalZ=1 AngleXU=0 Radius=1
    g357: BSplineCurve PolesCount=3 KnotsCount=2 Degree=2 IsPeriodic=0
    g358: GeomPoint X=46.0728 Y=72.4095 Z=0
    g359: GeomPoint X=42.0728 Y=76.4095 Z=0
    g360: Circle CenterX=-6.92719 CenterY=76.4095 CenterZ=0 NormalX=0 NormalY=0 NormalZ=1 AngleXU=0 Radius=1
    g361: Circle CenterX=-10.9272 CenterY=76.4095 CenterZ=0 NormalX=0 NormalY=0 NormalZ=1 AngleXU=0 Radius=1
    g362: Circle CenterX=-10.9272 CenterY=72.4095 CenterZ=0 NormalX=0 NormalY=0 NormalZ=1 AngleXU=0 Radius=1
    g363: BSplineCurve PolesCount=3 KnotsCount=2 Degree=2 IsPeriodic=0
    g364: GeomPoint X=-6.92719 Y=76.4095 Z=0
    g365: GeomPoint X=-10.9272 Y=72.4095 Z=0
    g366: LineSegment StartX=-10.9272 StartY=72.4095 StartZ=0 EndX=-10.9272 EndY=-78.7794 EndZ=0
    g367: LineSegment StartX=-7.42095 StartY=-80.8542 StartZ=0 EndX=42.5666 EndY=-53.4075 EndZ=0
    g368: LineSegment StartX=46.0728 StartY=-47.4823 StartZ=0 EndX=46.0728 EndY=72.4095 EndZ=0
    g369: LineSegment StartX=42.0728 StartY=76.4095 StartZ=0 EndX=-6.92719 EndY=76.4095 EndZ=0
    g370: LineSegment StartX=-42.9272 StartY=136.221 StartZ=0 EndX=407.073 EndY=136.221 EndZ=0
    g371: LineSegment StartX=232.072 StartY=136.221 StartZ=0 EndX=220.072 EndY=136.221 EndZ=0
    g372: LineSegment StartX=232.072 StartY=136.221 StartZ=0 EndX=232.072 EndY=124.221 EndZ=0
    g373: LineSegment StartX=220.072 StartY=136.221 StartZ=0 EndX=220.072 EndY=124.221 EndZ=0
    g374: LineSegment StartX=220.072 StartY=136.221 StartZ=0 EndX=226.072 EndY=136.221 EndZ=0
    g375: LineSegment StartX=220.072 StartY=136.221 StartZ=0 EndX=220.072 EndY=130.221 EndZ=0
    g376: LineSegment StartX=220.072 StartY=124.221 StartZ=0 EndX=226.072 EndY=124.221 EndZ=0
    g377: LineSegment StartX=232.072 StartY=124.221 StartZ=0 EndX=232.072 EndY=127.221 EndZ=0
    g378: LineSegment StartX=232.072 StartY=136.221 StartZ=0 EndX=232.072 EndY=133.221 EndZ=0
    g379-g383: Circle x5 (B-spline internal-alignment scaffolding for g384; pole/knot coordinates omitted)
    g384: BSplineCurve PolesCount=5 KnotsCount=3 Degree=3 IsPeriodic=0
    g385: GeomPoint X=232.072 Y=133.221 Z=0
    g386: GeomPoint X=223.072 Y=130.221 Z=0
    g387: GeomPoint X=232.072 Y=127.221 Z=0
    g388: LineSegment StartX=189.124 StartY=124.221 StartZ=0 EndX=302.073 EndY=124.221 EndZ=0
    g389: LineSegment StartX=132.072 StartY=136.221 StartZ=0 EndX=132.072 EndY=124.221 EndZ=0
    g390: LineSegment StartX=132.072 StartY=136.221 StartZ=0 EndX=144.072 EndY=136.221 EndZ=0
    g391: LineSegment StartX=144.072 StartY=136.221 StartZ=0 EndX=144.072 EndY=124.221 EndZ=0
    g392: LineSegment StartX=144.072 StartY=136.221 StartZ=0 EndX=138.072 EndY=136.221 EndZ=0
    g393: LineSegment StartX=144.072 StartY=136.221 StartZ=0 EndX=144.072 EndY=130.221 EndZ=0
    g394: LineSegment StartX=132.072 StartY=136.221 StartZ=0 EndX=132.072 EndY=133.221 EndZ=0
    g395: LineSegment StartX=132.072 StartY=133.221 StartZ=0 EndX=132.072 EndY=127.221 EndZ=0
    g396-g400: Circle x5 (B-spline internal-alignment scaffolding for g401; pole/knot coordinates omitted)
    g401: BSplineCurve PolesCount=5 KnotsCount=3 Degree=3 IsPeriodic=0
    g402: GeomPoint X=132.072 Y=133.221 Z=0
    g403: GeomPoint X=141.072 Y=130.221 Z=0
    g404: GeomPoint X=132.072 Y=127.221 Z=0
    g405: LineSegment StartX=132.072 StartY=124.221 StartZ=0 EndX=175.022 EndY=124.221 EndZ=0
    g406: LineSegment StartX=62.0728 StartY=124.221 StartZ=0 EndX=132.072 EndY=124.221 EndZ=0
    g407: LineSegment StartX=132.072 StartY=136.221 StartZ=0 EndX=131.457 EndY=138.832 EndZ=0
    ... +61 more geometry lines
  constraints (808):
    c: Vertical(g0)
    c: Vertical(g1)
    c: Block(g1)
    c: Block(g0)
    c: Weight(g4) = 1
    c: Equal(g4,g5)
    c: Equal(g4,g6)
    c: InternalAlignment(g4,g7)
    c: InternalAlignment(g5,g7)
    c: InternalAlignment(g6,g7)
    c: InternalAlignment(g8,g7)
    c: InternalAlignment(g9,g7)
    c: Weight(g10) = 1
    c: Equal(g10,g11)
    c: Equal(g10,g12)
    c: InternalAlignment(g10,g13)
    c: InternalAlignment(g11,g13)
    c: InternalAlignment(g12,g13)
    c: InternalAlignment(g14,g13)
    c: InternalAlignment(g15,g13)
    c: Block(g13)
    c: Block(g7)
    c: Weight(g16) = 1
    c: Equal(g16,g17)
    c: Equal(g16,g18)
    c: InternalAlignment(g16,g19)
    c: InternalAlignment(g17,g19)
    c: InternalAlignment(g18,g19)
    c: InternalAlignment(g20,g19)
    c: InternalAlignment(g21,g19)
    c: Weight(g22) = 1
    c: Equal(g22,g23)
    c: Equal(g22,g24)
    c: InternalAlignment(g22,g25)
    c: InternalAlignment(g23,g25)
    c: InternalAlignment(g24,g25)
    c: InternalAlignment(g26,g25)
    c: InternalAlignment(g27,g25)
    c: Block(g25)
    c: Block(g19)
    c: Weight(g28) = 1
    c: Equal(g28,g29)
    c: Equal(g28,g30)
    c: InternalAlignment(g28,g31)
    c: InternalAlignment(g29,g31)
    c: InternalAlignment(g30,g31)
    c: InternalAlignment(g32,g31)
    c: InternalAlignment(g33,g31)
    c: Weight(g34) = 1
    c: Equal(g34,g35)
    c: Equal(g34,g36)
    c: InternalAlignment(g34,g37)
    c: InternalAlignment(g35,g37)
    c: InternalAlignment(g36,g37)
    c: InternalAlignment(g38,g37)
    c: InternalAlignment(g39,g37)
    c: Block(g31)
    c: Block(g37)
    c: Coincident(g40,g1)
    c: Coincident(g40,g0)
    c: Horizontal(g40)
    c: Distance(g40) = 450
    c: Weight(g41) = 1
    c: Equal(g41,g42)
    c: Equal(g41,g43)
    c: InternalAlignment(g41,g44)
    c: InternalAlignment(g42,g44)
    c: InternalAlignment(g43,g44)
    c: InternalAlignment(g45,g44)
    c: InternalAlignment(g46,g44)
    c: Block(g44)
    c: Weight(g47) = 1
    c: Equal(g47,g48)
    c: Equal(g47,g49)
    c: InternalAlignment(g47,g50)
    c: InternalAlignment(g48,g50)
    c: InternalAlignment(g49,g50)
    c: InternalAlignment(g51,g50)
    c: InternalAlignment(g52,g50)
    c: Block(g50)
    c: Weight(g53) = 1
    c: Equal(g53,g54)
    c: Equal(g53,g55)
    c: InternalAlignment(g53,g56)
    c: InternalAlignment(g54,g56)
    c: InternalAlignment(g55,g56)
    c: InternalAlignment(g57,g56)
    c: InternalAlignment(g58,g56)
    c: Block(g56)
    c: Weight(g59) = 1
    c: Equal(g59,g60)
    c: Equal(g59,g61)
    c: InternalAlignment(g59,g62)
    c: InternalAlignment(g60,g62)
    c: InternalAlignment(g61,g62)
    c: InternalAlignment(g63,g62)
    c: InternalAlignment(g64,g62)
    c: Block(g62)
    c: Weight(g65) = 1
    c: Equal(g65,g66)
    c: Equal(g65,g67)
    c: InternalAlignment(g65,g68)
    c: InternalAlignment(g66,g68)
    c: InternalAlignment(g67,g68)
    c: InternalAlignment(g69,g68)
    c: InternalAlignment(g70,g68)
    c: Weight(g71) = 1
    c: Equal(g71,g72)
    c: Equal(g71,g73)
    c: InternalAlignment(g71,g74)
    c: InternalAlignment(g72,g74)
    c: InternalAlignment(g73,g74)
    c: InternalAlignment(g75,g74)
    c: InternalAlignment(g76,g74)
    c: Block(g68)
    c: Block(g74)
    c: Coincident(g77,g68)
    c: Coincident(g77,g74)
    c: Vertical(g77)
    c: Coincident(g78,g68)
    c: Coincident(g78,g50)
    c: Coincident(g79,g50)
    c: Coincident(g79,g74)
    c: Weight(g80) = 1
    c: Equal(g80,g81)
    c: Equal(g80,g82)
    c: InternalAlignment(g80,g83)
    c: InternalAlignment(g81,g83)
    c: InternalAlignment(g82,g83)
    c: InternalAlignment(g84,g83)
    c: InternalAlignment(g85,g83)
    c: Weight(g86) = 1
    c: Equal(g86,g87)
    c: Equal(g86,g88)
    c: InternalAlignment(g86,g89)
    c: InternalAlignment(g87,g89)
    c: InternalAlignment(g88,g89)
    c: InternalAlignment(g90,g89)
    c: InternalAlignment(g91,g89)
    c: Block(g83)
    c: Block(g89)
    c: Coincident(g92,g83)
    c: Coincident(g92,g89)
    c: Vertical(g92)
    c: Coincident(g93,g83)
    c: Coincident(g93,g44)
    c: Coincident(g94,g44)
    c: Coincident(g94,g89)
    c: Weight(g95) = 1
    c: Equal(g95,g96)
    c: Equal(g95,g97)
    c: InternalAlignment(g95,g98)
    c: InternalAlignment(g96,g98)
    c: InternalAlignment(g97,g98)
    c: InternalAlignment(g99,g98)
    c: InternalAlignment(g100,g98)
    c: Weight(g101) = 1
    c: Equal(g101,g102)
    c: Equal(g101,g103)
    c: InternalAlignment(g101,g104)
    c: InternalAlignment(g102,g104)
    c: InternalAlignment(g103,g104)
    c: InternalAlignment(g105,g104)
    c: InternalAlignment(g106,g104)
    c: Block(g98)
    c: Block(g104)
    c: Coincident(g107,g98)
    c: Coincident(g107,g104)
    c: Vertical(g107)
    c: Coincident(g108,g104)
    c: Coincident(g108,g62)
    c: Coincident(g109,g62)
    c: Coincident(g109,g98)
    c: Weight(g110) = 1
    c: Equal(g110,g111)
    c: Equal(g110,g112)
    c: InternalAlignment(g110,g113)
    c: InternalAlignment(g111,g113)
    c: InternalAlignment(g112,g113)
    c: InternalAlignment(g114,g113)
    c: InternalAlignment(g115,g113)
    c: Weight(g116) = 1
    c: Equal(g116,g117)
    c: Equal(g116,g118)
    c: InternalAlignment(g116,g119)
    c: InternalAlignment(g117,g119)
    c: InternalAlignment(g118,g119)
    c: InternalAlignment(g120,g119)
    c: InternalAlignment(g121,g119)
    c: Block(g113)
    c: Block(g119)
    c: Coincident(g122,g113)
    c: Coincident(g122,g119)
    c: Vertical(g122)
    c: Coincident(g123,g119)
    c: Coincident(g123,g56)
    c: Coincident(g124,g56)
    c: Coincident(g124,g113)
    c: Weight(g125) = 1
    c: Equal(g125,g126)
    c: Equal(g125,g127)
    c: InternalAlignment(g125,g128)
    c: InternalAlignment(g126,g128)
    c: InternalAlignment(g127,g128)
    c: InternalAlignment(g129,g128)
    c: InternalAlignment(g130,g128)
    c: Weight(g131) = 1
    c: Equal(g131,g132)
    c: Equal(g131,g133)
    c: InternalAlignment(g131,g134)
    c: InternalAlignment(g132,g134)
    c: InternalAlignment(g133,g134)
    c: InternalAlignment(g135,g134)
    c: InternalAlignment(g136,g134)
    c: Weight(g137) = 1
    c: Equal(g137,g138)
    c: Equal(g137,g139)
    c: InternalAlignment(g137,g140)
    c: InternalAlignment(g138,g140)
    c: InternalAlignment(g139,g140)
    c: InternalAlignment(g141,g140)
    c: InternalAlignment(g142,g140)
    c: Weight(g143) = 1
    c: Equal(g143,g144)
    c: Equal(g143,g145)
    c: InternalAlignment(g143,g146)
    c: InternalAlignment(g144,g146)
    c: InternalAlignment(g145,g146)
    c: InternalAlignment(g147,g146)
    c: InternalAlignment(g148,g146)
    c: Block(g146)
    c: Block(g140)
    c: Block(g134)
    c: Block(g128)
    c: Coincident(g149,g25)
    c: Coincident(g149,g146)
    c: Coincident(g150,g146)
    c: Coincident(g150,g140)
    c: Horizontal(g150)
    c: Coincident(g151,g140)
    c: Coincident(g151,g25)
    c: Vertical(g151)
    c: Coincident(g152,g19)
    c: Coincident(g152,g134)
    c: Vertical(g152)
    c: Coincident(g153,g134)
    c: Coincident(g153,g128)
    c: Horizontal(g153)
    c: Coincident(g154,g128)
    c: Coincident(g154,g19)
    c: Weight(g155) = 1
    c: Equal(g155,g156)
    c: Equal(g155,g157)
    c: InternalAlignment(g155,g158)
    c: InternalAlignment(g156,g158)
    c: InternalAlignment(g157,g158)
    c: InternalAlignment(g159,g158)
    c: InternalAlignment(g160,g158)
    c: Weight(g161) = 1
    c: Equal(g161,g162)
    c: Equal(g161,g163)
    c: InternalAlignment(g161,g164)
    c: InternalAlignment(g162,g164)
    c: InternalAlignment(g163,g164)
    c: InternalAlignment(g165,g164)
    c: InternalAlignment(g166,g164)
    c: Weight(g167) = 1
    c: Equal(g167,g168)
    c: Equal(g167,g169)
    c: InternalAlignment(g167,g170)
    c: InternalAlignment(g168,g170)
    c: InternalAlignment(g169,g170)
    c: InternalAlignment(g171,g170)
    c: InternalAlignment(g172,g170)
    c: Weight(g173) = 1
    c: Equal(g173,g174)
    c: Equal(g173,g175)
    c: InternalAlignment(g173,g176)
    c: InternalAlignment(g174,g176)
    c: InternalAlignment(g175,g176)
    c: InternalAlignment(g177,g176)
    c: InternalAlignment(g178,g176)
    c: Block(g176)
    c: Block(g170)
    c: Block(g164)
    c: Block(g158)
    c: Coincident(g179,g170)
    c: Coincident(g179,g7)
    c: Vertical(g179)
    c: Coincident(g180,g13)
    c: Coincident(g180,g164)
    c: Vertical(g180)
    c: Coincident(g181,g158)
    c: Coincident(g181,g13)
    c: Coincident(g182,g7)
    c: Weight(g183) = 1
    c: Equal(g183,g184)
    c: Equal(g183,g185)
    c: InternalAlignment(g183,g186)
    c: InternalAlignment(g184,g186)
    c: InternalAlignment(g185,g186)
    c: InternalAlignment(g187,g186)
    c: InternalAlignment(g188,g186)
    c: Weight(g189) = 1
    c: Equal(g189,g190)
    c: Equal(g189,g191)
    c: InternalAlignment(g189,g192)
    c: InternalAlignment(g190,g192)
    c: InternalAlignment(g191,g192)
    c: InternalAlignment(g193,g192)
    c: InternalAlignment(g194,g192)
    c: Block(g192)
    c: Block(g186)
    c: Coincident(g195,g192)
    c: Coincident(g195,g31)
    c: Coincident(g196,g31)
    c: Coincident(g196,g186)
    c: Coincident(g197,g186)
    c: Coincident(g197,g192)
    c: Vertical(g197)
    c: Weight(g198) = 1
    c: Equal(g198,g199)
    c: Equal(g198,g200)
    c: InternalAlignment(g198,g201)
    c: InternalAlignment(g199,g201)
    c: InternalAlignment(g200,g201)
    c: InternalAlignment(g202,g201)
    c: InternalAlignment(g203,g201)
    c: Weight(g204) = 1
    c: Equal(g204,g205)
    c: Equal(g204,g206)
    c: InternalAlignment(g204,g207)
    c: InternalAlignment(g205,g207)
    c: InternalAlignment(g206,g207)
    c: InternalAlignment(g208,g207)
    c: InternalAlignment(g209,g207)
    c: Block(g207)
    c: Block(g201)
    c: Coincident(g210,g201)
    c: Coincident(g210,g37)
    c: Coincident(g211,g37)
    c: Coincident(g211,g207)
    c: Coincident(g212,g207)
    c: Coincident(g212,g201)
    c: Vertical(g212)
    c: Horizontal(g213)
    c: Block(g213)
    c: Vertical(g214)
    c: Block(g214)
    c: Block(g215)
    c: Weight(g216) = 1
    c: Equal(g216,g217)
    c: Equal(g216,g218)
    c: InternalAlignment(g216,g219)
    c: InternalAlignment(g217,g219)
    c: InternalAlignment(g218,g219)
    c: InternalAlignment(g220,g219)
    c: InternalAlignment(g221,g219)
    c: Weight(g222) = 1
    c: Equal(g222,g223)
    c: Equal(g222,g224)
    c: InternalAlignment(g222,g225)
    c: InternalAlignment(g223,g225)
    c: InternalAlignment(g224,g225)
    c: InternalAlignment(g226,g225)
    c: InternalAlignment(g227,g225)
    c: Weight(g228) = 1
    c: Equal(g228,g229)
    c: Equal(g228,g230)
    c: InternalAlignment(g228,g231)
    c: InternalAlignment(g229,g231)
    c: InternalAlignment(g230,g231)
    c: InternalAlignment(g232,g231)
    c: InternalAlignment(g233,g231)
    c: Weight(g234) = 1
    c: Equal(g234,g235)
    c: Equal(g234,g236)
    c: InternalAlignment(g234,g237)
    c: InternalAlignment(g235,g237)
    c: InternalAlignment(g236,g237)
    c: InternalAlignment(g238,g237)
    c: InternalAlignment(g239,g237)
    c: Block(g219)
    c: Block(g225)
    c: Block(g231)
    c: Block(g237)
    c: Coincident(g240,g225)
    c: Coincident(g240,g219)
    c: Horizontal(g240)
    c: Block(g182)
    c: Weight(g241) = 1
    c: Equal(g241,g242)
    c: Equal(g241,g243)
    c: InternalAlignment(g241,g244)
    c: InternalAlignment(g242,g244)
    c: InternalAlignment(g243,g244)
    c: InternalAlignment(g245,g244)
    c: InternalAlignment(g246,g244)
    c: Weight(g247) = 1
    c: Equal(g247,g248)
    c: Equal(g247,g249)
    c: InternalAlignment(g247,g250)
    c: InternalAlignment(g248,g250)
    c: InternalAlignment(g249,g250)
    c: InternalAlignment(g251,g250)
    c: InternalAlignment(g252,g250)
    c: Block(g244)
    c: Block(g250)
    c: Coincident(g253,g244)
    c: Coincident(g253,g250)
    c: Weight(g254) = 1
    c: Equal(g254,g255)
    c: Equal(g254,g256)
    c: InternalAlignment(g254,g257)
    c: InternalAlignment(g255,g257)
    c: InternalAlignment(g256,g257)
    c: InternalAlignment(g258,g257)
    c: InternalAlignment(g259,g257)
    c: Weight(g260) = 1
    c: Equal(g260,g261)
    c: Equal(g260,g262)
    c: InternalAlignment(g260,g263)
    c: InternalAlignment(g261,g263)
    c: InternalAlignment(g262,g263)
    c: InternalAlignment(g264,g263)
    c: InternalAlignment(g265,g263)
    c: Weight(g266) = 1
    c: Equal(g266,g267)
    c: Equal(g266,g268)
    c: InternalAlignment(g266,g269)
    c: InternalAlignment(g267,g269)
    c: InternalAlignment(g268,g269)
    c: InternalAlignment(g270,g269)
    c: InternalAlignment(g271,g269)
    c: Block(g269)
    c: Block(g263)
    c: Block(g257)
    c: Coincident(g272,g263)
    c: Coincident(g272,g257)
    c: Coincident(g273,g257)
    c: Coincident(g273,g269)
    c: Vertical(g273)
    c: Coincident(g274,g269)
    c: Coincident(g274,g263)
    c: Horizontal(g274)
    c: Weight(g275) = 1
    c: Equal(g275,g276)
    c: InternalAlignment(g275,g277)
    c: InternalAlignment(g276,g277)
    c: InternalAlignment(g278,g277)
    c: InternalAlignment(g279,g277)
    c: Weight(g280) = 1
    c: InternalAlignment(g281,g283)
    c: InternalAlignment(g282,g283)
    c: InternalAlignment(g284,g283)
    c: InternalAlignment(g285,g283)
    c: Weight(g286) = 1
    c: Equal(g286,g287)
    c: Equal(g286,g288)
    c: InternalAlignment(g286,g289)
    c: InternalAlignment(g287,g289)
    c: InternalAlignment(g288,g289)
    c: InternalAlignment(g290,g289)
    c: InternalAlignment(g291,g289)
    c: Equal(g292,g293)
    c: Equal(g292,g294)
    c: InternalAlignment(g292,g295)
    c: InternalAlignment(g293,g295)
    c: InternalAlignment(g294,g295)
    c: InternalAlignment(g296,g295)
    c: InternalAlignment(g297,g295)
    c: Block(g283)
    c: Block(g289)
    c: Block(g295)
    c: Block(g277)
    c: Coincident(g298,g277)
    c: Coincident(g298,g283)
    c: Horizontal(g298)
    c: Coincident(g299,g283)
    c: Coincident(g299,g289)
    c: Vertical(g299)
    c: Coincident(g300,g289)
    c: Coincident(g300,g295)
    c: Horizontal(g300)
    c: Coincident(g301,g295)
    c: Coincident(g301,g277)
    c: Weight(g302) = 1
    c: Equal(g302,g303)
    c: Equal(g302,g304)
    c: InternalAlignment(g302,g305)
    c: InternalAlignment(g303,g305)
    c: InternalAlignment(g304,g305)
    c: InternalAlignment(g306,g305)
    c: InternalAlignment(g307,g305)
    c: Weight(g308) = 1
    c: Equal(g308,g309)
    c: Equal(g308,g310)
    c: InternalAlignment(g308,g311)
    c: InternalAlignment(g309,g311)
    c: InternalAlignment(g310,g311)
    c: InternalAlignment(g312,g311)
    c: Weight(g314) = 1
    c: Equal(g314,g315)
    c: Equal(g314,g316)
    c: InternalAlignment(g314,g317)
    c: InternalAlignment(g315,g317)
    c: InternalAlignment(g316,g317)
    c: InternalAlignment(g318,g317)
    c: InternalAlignment(g319,g317)
    c: Block(g317)
    c: Block(g311)
    c: Block(g305)
    c: Coincident(g320,g317)
    c: Coincident(g320,g311)
    c: Horizontal(g320)
    c: Coincident(g321,g311)
    c: Coincident(g321,g305)
    c: Vertical(g321)
    c: Coincident(g322,g305)
    c: Coincident(g322,g317)
    c: InternalAlignment(g323,g324)
    c: InternalAlignment(g325,g324)
    c: InternalAlignment(g326,g324)
    c: Block(g324)
    c: Equal(g327,g328)
    c: Equal(g327,g329)
    c: InternalAlignment(g327,g330)
    c: InternalAlignment(g328,g330)
    c: InternalAlignment(g329,g330)
    c: InternalAlignment(g331,g330)
    c: InternalAlignment(g332,g330)
    c: Block(g330)
    c: Coincident(g333,g324)
    c: Horizontal(g333)
    c: Block(g333)
    c: Coincident(g334,g324)
    c: Coincident(g334,g250)
    c: Vertical(g334)
    c: Coincident(g335,g330)
    c: Coincident(g335,g244)
    c: Vertical(g335)
    c: Block(g336)
    c: Block(g2)
    c: Distance(g334) = 119.89
    c: Coincident(g337,g336)
    c: Coincident(g337,g2)
    c: Coincident(g338,g2)
    c: Coincident(g338,g336)
    c: Block(g3)
    c: Block(g339)
    c: Coincident(g340,g339)
    c: Coincident(g340,g3)
    c: Coincident(g341,g339)
    c: Coincident(g341,g3)
    c: Block(g341)
    c: Block(g340)
    c: Weight(g342) = 1
    c: Equal(g342,g344)
    c: InternalAlignment(g342,g345)
    c: InternalAlignment(g343,g345)
    c: InternalAlignment(g344,g345)
    c: InternalAlignment(g346,g345)
    c: InternalAlignment(g347,g345)
    c: InternalAlignment(g352,g351)
    c: InternalAlignment(g353,g351)
    c: InternalAlignment(g355,g357)
    c: Horizontal(g369)
    c: Coincident(g370,g0)
    c: Horizontal(g370)
    c: Block(g370)
    c: Distance(g370) = 450
    c: Horizontal(g371)
    c: Distance(g371) = 12
    c: Coincident(g373,g371)
    c: Vertical(g373)
    c: Horizontal(g374)
    c: Vertical(g375)
    c: Distance(g375) = 6
    c: Coincident(g375,g371)
    c: Coincident(g374,g371)
    c: Block(g373)
    c: Coincident(g376,g373)
    c: Horizontal(g376)
    c: Distance(g376) = 6
    c: Vertical(g377)
    c: Distance(g377) = 3
    c: Vertical(g378)
    c: Distance(g378) = 3
    c: Coincident(g372,g377)
    c: Coincident(g384,g378)
    c: Weight(g379) = 1
    c: Equal(g379,g380)
    c: Coincident(g380,g374)
    c: Equal(g379,g381)
    c: Coincident(g381,g375)
    c: Equal(g379,g382)
    c: Coincident(g382,g376)
    c: Equal(g379,g383)
    c: Coincident(g384,g377)
    c: InternalAlignment(g379-g383 -> g384) x5
    c: InternalAlignment(g385,g384)
    c: InternalAlignment(g386,g384)
    c: InternalAlignment(g387,g384)
    c: Coincident(g388,g164)
    c: Coincident(g388,g158)
    c: Coincident(g392,g390)
    c: Vertical(g393)
    c: Distance(g393) = 6
    c: Coincident(g393,g390)
    c: Vertical(g394)
    c: Distance(g394) = 3
    c: Vertical(g395)
    c: Distance(g395) = 6
    c: Coincident(g395,g394)
    c: Coincident(g401,g394)
    c: Weight(g396) = 1
    c: Equal(g396,g397)
    c: Coincident(g397,g392)
    c: Equal(g396,g398)
    c: Coincident(g398,g393)
    c: Equal(g396,g399)
    c: Equal(g396,g400)
    c: Coincident(g401,g395)
    c: InternalAlignment(g396-g400 -> g401) x5
    c: InternalAlignment(g402,g401)
    c: InternalAlignment(g403,g401)
    c: InternalAlignment(g404,g401)
    c: Coincident(g405,g389)
    c: Coincident(g405,g170)
    c: Horizontal(g405)
    c: Block(g401)
    c: Coincident(g406,g176)
    c: Coincident(g406,g389)
    c: Horizontal(g406)
    c: Block(g405)
    c: Coincident(g408,g389)
    c: PointOnObject(g408,g153)
    c: Vertical(g408)
    c: Block(g409)
    c: Coincident(g410,g409)
    c: Vertical(g410)
    c: PointOnObject(g410,g40)
    c: Block(g410)
    c: Coincident(g411,g409)
    c: Vertical(g411)
    c: Block(g411)
    c: Vertical(g412)
    c: Distance(g412) = 3
    c: Equal(g379,g415) = 1
    c: Equal(g415,g416)
    c: InternalAlignment(g415,g417)
    c: InternalAlignment(g416,g417)
    c: InternalAlignment(g413,g417)
    c: InternalAlignment(g414,g417)
    c: InternalAlignment(g418,g417)
    c: Block(g417)
    c: Coincident(g418,g412)
    c: Coincident(g419,g417)
    c: PointOnObject(g419,g150)
    c: Vertical(g419)
    c: Distance(g420) = 3
    c: Block(g420)
    c: Distance(g421) = 3
    c: Parallel(g421,g420)
    c: Coincident(g421,g420)
    c: Coincident(g422,g420)
    c: Perpendicular(g422,g420)
    c: Distance(g422) = 3
    c: Coincident(g423,g421)
    c: Perpendicular(g423,g421)
    c: Distance(g423) = 3
    c: Coincident(g424,g420)
    c: Perpendicular(g424,g421)
    c: Distance(g424) = 6
    c: Coincident(g425,g424)
    c: PointOnObject(g423,g425)
    c: Coincident(g426,g420)
    c: PointOnObject(g426,g79)
    c: Block(g426)
    c: Distance(g427) = 2.76
    c: Coincident(g428,g427)
    c: Parallel(g427,g428)
    c: PointOnObject(g428,g181)
    c: Distance(g428) = 2.41
    c: Block(g428)
    c: Coincident(g429,g427)
    c: Distance(g429) = 6.6
    c: Perpendicular(g429,g428)
    c: Distance(g430) = 6.6
    c: Coincident(g431,g429)
    c: Coincident(g431,g430)
    c: Block(g432)
    c: Coincident(g433,g432)
    c: Vertical(g433)
    c: Distance(g433) = 3.6
    c: Coincident(g434,g427)
    c: Parallel(g427,g434)
    c: PointOnObject(g434,g78)
    c: Block(g434)
    c: Coincident(g435,g421)
    c: Parallel(g435,g421)
    c: PointOnObject(g435,g211)
    c: Block(g435)
    c: Coincident(g436,g435)
    c: Vertical(g436)
    c: PointOnObject(g436,g210)
    c: Coincident(g437,g436)
    c: Perpendicular(g437,g210)
    c: Distance(g437) = 3
    c: Coincident(g438,g437)
    c: Block(g437)
    c: Distance(g438) = 3
    c: Parallel(g437,g438)
    c: Coincident(g439,g438)
    c: Distance(g439) = 3
    c: Parallel(g438,g439)
    c: Coincident(g440,g439)
    c: Parallel(g440,g437)
    c: PointOnObject(g440,g124)
    c: PointOnObject(g441,g53)
    c: Tangent(g440,g441)
    c: Coincident(g442,g439)
    c: Perpendicular(g442,g439)
    c: Coincident(g443,g437)
    c: Parallel(g443,g442)
    c: Distance(g443) = 3
    c: Distance(g442) = 3
    c: PointOnObject(g442,g444)
    c: Block(g444)
    c: PointOnObject(g445,g123)
    c: Perpendicular(g123,g445)
    c: Distance(g445) = 2.41
    c: Block(g445)
    c: Coincident(g446,g445)
    c: Perpendicular(g123,g446)
    c: Distance(g446) = 2.76
    c: Coincident(g447,g446)
    c: Perpendicular(g123,g447)
    c: PointOnObject(g447,g149)
    c: Coincident(g448,g445)
    c: Parallel(g123,g448)
    c: Distance(g448) = 6.6
    c: Coincident(g449,g446)
    c: Parallel(g123,g449)
    c: Coincident(g450,g448)
    c: Distance(g449) = 6.6
    c: Coincident(g449,g450)
    c: Block(g149)
    c: Block(g124)
    c: Block(g211)
    c: Block(g181)
    c: Block(g78)
    c: Block(g79)
    c: Block(g430)
    c: Coincident(g451,g447)
    c: Distance(g451) = 46
    c: Parallel(g149,g451)
    c: Coincident(g452,g451)
    c: Horizontal(g452)
    c: PointOnObject(g452,g154)
    c: Coincident(g453,g451)
    c: Vertical(g453)
    c: Distance(g453) = 9
    c: Block(g452)
    c: PointOnObject(g454,g93)
    c: Distance(g455) = 6.6
    c: Distance(g456) = 6.6
    c: Block(g454)
    c: Coincident(g457,g456)
    c: Coincident(g457,g455)
    c: Perpendicular(g457,g182)
    c: Coincident(g458,g455)
    c: Perpendicular(g458,g182)
    c: PointOnObject(g458,g182)
    c: Block(g458)
    c: Block(g457)
    c: Block(g456)
    c: PointOnObject(g459,g196)
    c: Perpendicular(g196,g459)
    c: Distance(g459) = 3
    c: Coincident(g460,g459)
    c: Perpendicular(g196,g460)
    c: Distance(g460) = 3
    c: Coincident(g461,g460)
    c: Perpendicular(g196,g461)
    c: Distance(g461) = 3
    c: Coincident(g462,g461)
    c: Tangent(g462,g41)
    c: PointOnObject(g462,g94)
    c: Block(g462)
    c: Block(g459)
    c: Coincident(g463,g459)
    c: Parallel(g196,g463)
    c: Distance(g463) = 3
    c: Coincident(g464,g461)
    c: Distance(g464) = 3
    c: Parallel(g196,g464)
    c: Coincident(g465,g460)
    c: Distance(g465) = 6
    c: Parallel(g465,g196)
    c: Coincident(g466,g465)
    c: PointOnObject(g464,g466)
    c: Block(g466)
    c: Coincident(g467,g458)
    c: Vertical(g467)
    c: PointOnObject(g467,g195)
    c: Coincident(g468,g467)
    c: Perpendicular(g195,g468)
FEATURE [Sketcher::SketchObject] Sketch004  label="rightSideBottom"
  FullyConstrained = false
  sketch-geometry (91):
    g0: ArcOfCircle CenterX=391.073 CenterY=-83.7794 CenterZ=0 NormalX=0 NormalY=0 NormalZ=1 AngleXU=0 Radius=8 StartAngle=3.14159 EndAngle=6.28319
    g1: Circle CenterX=306.073 CenterY=-81.8102 CenterZ=0 NormalX=0 NormalY=0 NormalZ=1 AngleXU=0 Radius=1
    g2: Circle CenterX=306.073 CenterY=-77.8102 CenterZ=0 NormalX=0 NormalY=0 NormalZ=1 AngleXU=0 Radius=1
    g3: Circle CenterX=302.567 CenterY=-42.9683 CenterZ=0 NormalX=0 NormalY=0 NormalZ=1 AngleXU=0 Radius=1
    g4: Circle CenterX=306.073 CenterY=-44.8935 CenterZ=0 NormalX=0 NormalY=0 NormalZ=1 AngleXU=0 Radius=1
    g5: Circle CenterX=306.073 CenterY=-40.8935 CenterZ=0 NormalX=0 NormalY=0 NormalZ=1 AngleXU=0 Radius=1
    g6: BSplineCurve PolesCount=3 KnotsCount=2 Degree=2 IsPeriodic=0
    g7: GeomPoint X=302.567 Y=-42.9683 Z=0
    g8: GeomPoint X=306.073 Y=-40.8935 Z=0
    g9: Circle CenterX=371.567 CenterY=-80.8644 CenterZ=0 NormalX=0 NormalY=0 NormalZ=1 AngleXU=0 Radius=1
    g10: Circle CenterX=375.073 CenterY=-82.7896 CenterZ=0 NormalX=0 NormalY=0 NormalZ=1 AngleXU=0 Radius=1
    g11: Circle CenterX=375.073 CenterY=-78.7896 CenterZ=0 NormalX=0 NormalY=0 NormalZ=1 AngleXU=0 Radius=1
    g12: GeomPoint X=371.567 Y=-80.8644 Z=0
    g13: GeomPoint X=375.073 Y=-78.7896 Z=0
    g14: Circle CenterX=318.073 CenterY=-51.4823 CenterZ=0 NormalX=0 NormalY=0 NormalZ=1 AngleXU=0 Radius=1
    g15: Circle CenterX=318.073 CenterY=-47.4805 CenterZ=0 NormalX=0 NormalY=0 NormalZ=1 AngleXU=0 Radius=1
    g16: GeomPoint X=321.579 Y=-53.4075 Z=0
    g17: GeomPoint X=318.073 Y=-47.4805 Z=0
    g18: Circle CenterX=321.579 CenterY=-67.3492 CenterZ=0 NormalX=0 NormalY=0 NormalZ=1 AngleXU=0 Radius=1
    g19: Circle CenterX=318.073 CenterY=-65.424 CenterZ=0 NormalX=0 NormalY=0 NormalZ=1 AngleXU=0 Radius=1
    g20: Circle CenterX=318.073 CenterY=-69.424 CenterZ=0 NormalX=0 NormalY=0 NormalZ=1 AngleXU=0 Radius=1
    g21: GeomPoint X=321.579 Y=-67.3492 Z=0
    g22: GeomPoint X=318.073 Y=-69.424 Z=0
    g23: Circle CenterX=362.567 CenterY=-89.8542 CenterZ=0 NormalX=0 NormalY=0 NormalZ=1 AngleXU=0 Radius=1
    g24: Circle CenterX=366.073 CenterY=-91.7794 CenterZ=0 NormalX=0 NormalY=0 NormalZ=1 AngleXU=0 Radius=1
    g25: Circle CenterX=362.073 CenterY=-91.7794 CenterZ=0 NormalX=0 NormalY=0 NormalZ=1 AngleXU=0 Radius=1
    g26: GeomPoint X=362.567 Y=-89.8542 Z=0
    g27: GeomPoint X=362.073 Y=-91.7794 Z=0
    g28: Circle CenterX=322.073 CenterY=-91.7794 CenterZ=0 NormalX=0 NormalY=0 NormalZ=1 AngleXU=0 Radius=1
    g29: Circle CenterX=318.073 CenterY=-91.7794 CenterZ=0 NormalX=0 NormalY=0 NormalZ=1 AngleXU=0 Radius=1
    g30: Circle CenterX=318.073 CenterY=-87.7794 CenterZ=0 NormalX=0 NormalY=0 NormalZ=1 AngleXU=0 Radius=1
    g31: GeomPoint X=322.073 Y=-91.7794 Z=0
    g32: GeomPoint X=318.073 Y=-87.7794 Z=0
    g33: ArcOfCircle CenterX=391.073 CenterY=22.1087 CenterZ=0 NormalX=0 NormalY=0 NormalZ=1 AngleXU=0 Radius=4 StartAngle=0 EndAngle=3.14159
    g34: LineSegment StartX=387.073 StartY=22.1087 StartZ=0 EndX=383.073 EndY=-83.7794 EndZ=0
    g35: LineSegment StartX=395.073 StartY=22.1087 StartZ=0 EndX=399.073 EndY=-83.7794 EndZ=0
    g36: LineSegment StartX=232.072 StartY=-103.779 StartZ=0 EndX=232.072 EndY=-100.779 EndZ=0
    g37: GeomPoint X=232.072 Y=-94.7794 Z=0
    g38: GeomPoint X=223.072 Y=-97.7794 Z=0
    g39: Circle CenterX=232.072 CenterY=-94.7794 CenterZ=0 NormalX=0 NormalY=0 NormalZ=1 AngleXU=0 Radius=1
    g40: Circle CenterX=232.072 CenterY=-100.779 CenterZ=0 NormalX=0 NormalY=0 NormalZ=1 AngleXU=0 Radius=1
    g41: BSplineCurve PolesCount=5 KnotsCount=3 Degree=3 IsPeriodic=0
    g42: GeomPoint X=232.072 Y=-100.779 Z=0
    g43: LineSegment StartX=232.072 StartY=-94.7794 StartZ=0 EndX=232.072 EndY=-91.7794 EndZ=0
    g44: LineSegment StartX=245.072 StartY=-31.3037 StartZ=0 EndX=243.535 EndY=-33.1602 EndZ=0
    g45: LineSegment StartX=241.775 StartY=-35.2862 StartZ=0 EndX=240.266 EndY=-37.1092 EndZ=0
    g46: LineSegment StartX=243.535 StartY=-33.1602 StartZ=0 EndX=248.619 EndY=-37.3688 EndZ=0
    g47: LineSegment StartX=241.775 StartY=-35.2862 StartZ=0 EndX=246.859 EndY=-39.4949 EndZ=0
    g48: LineSegment StartX=248.619 StartY=-37.3688 StartZ=0 EndX=246.859 EndY=-39.4949 EndZ=0
    g49: LineSegment StartX=232.072 StartY=-103.779 StartZ=0 EndX=407.073 EndY=-103.779 EndZ=0
    g50: LineSegment StartX=299.888 StartY=-86.6413 StartZ=0 EndX=240.266 EndY=-37.1092 EndZ=0
    g51: LineSegment StartX=245.072 StartY=-11.4025 StartZ=0 EndX=302.567 EndY=-42.9683 EndZ=0
    g52: BSplineCurve PolesCount=3 KnotsCount=2 Degree=2 IsPeriodic=0
    g53: BSplineCurve PolesCount=3 KnotsCount=2 Degree=2 IsPeriodic=0
    g54: LineSegment StartX=321.579 StartY=-53.4075 StartZ=0 EndX=371.567 EndY=-80.8644 EndZ=0
    g55: BSplineCurve PolesCount=3 KnotsCount=2 Degree=2 IsPeriodic=0
    g56: BSplineCurve PolesCount=3 KnotsCount=2 Degree=2 IsPeriodic=0
    g57: BSplineCurve PolesCount=3 KnotsCount=2 Degree=2 IsPeriodic=0
    g58: LineSegment StartX=318.073 StartY=-69.424 StartZ=0 EndX=318.073 EndY=-87.7794 EndZ=0
    g59: LineSegment StartX=321.579 StartY=-67.3492 StartZ=0 EndX=362.567 EndY=-89.8542 EndZ=0
    g60: LineSegment StartX=362.073 StartY=-91.7794 StartZ=0 EndX=322.073 EndY=-91.7794 EndZ=0
    g61: BSplineCurve PolesCount=3 KnotsCount=2 Degree=2 IsPeriodic=0
    g62: BSplineCurve PolesCount=3 KnotsCount=2 Degree=2 IsPeriodic=0
    g63: LineSegment StartX=245.072 StartY=-31.3037 StartZ=0 EndX=302.996 EndY=-79.2541 EndZ=0
    g64: LineSegment StartX=302.567 StartY=-56.9099 StartZ=0 EndX=239.193 EndY=-22.1109 EndZ=0
    g65: LineSegment StartX=306.073 StartY=-62.8351 StartZ=0 EndX=306.073 EndY=-77.8102 EndZ=0
    g66: BSplineCurve PolesCount=3 KnotsCount=2 Degree=2 IsPeriodic=0
    g67: LineSegment StartX=298.776 StartY=-91.7794 StartZ=0 EndX=232.072 EndY=-91.7794 EndZ=0
    g68: LineSegment StartX=245.072 StartY=-11.4025 StartZ=0 EndX=243.628 EndY=-14.0323 EndZ=0
    g69: LineSegment StartX=240.741 StartY=-19.2917 StartZ=0 EndX=239.193 EndY=-22.1109 EndZ=0
    g70: LineSegment StartX=243.628 StartY=-14.0323 StartZ=0 EndX=246.258 EndY=-15.476 EndZ=0
    g71: LineSegment StartX=240.741 StartY=-19.2917 StartZ=0 EndX=243.37 EndY=-20.7355 EndZ=0
    g72: ArcOfCircle CenterX=247.444 CenterY=-19.5495 CenterZ=0 NormalX=0 NormalY=0 NormalZ=1 AngleXU=0 Radius=4.24264 StartAngle=3.4249 EndAngle=8.13729
    g73: LineSegment StartX=407.073 StartY=-103.779 StartZ=0 EndX=407.073 EndY=48.2206 EndZ=0
    g74: LineSegment StartX=375.073 StartY=48.2206 StartZ=0 EndX=375.073 EndY=-78.7896 EndZ=0
    g75: LineSegment StartX=375.073 StartY=48.2206 StartZ=0 EndX=382.073 EndY=48.2206 EndZ=0
    g76: LineSegment StartX=407.073 StartY=48.2206 StartZ=0 EndX=400.073 EndY=48.2206 EndZ=0
    g77: LineSegment StartX=394.073 StartY=48.2206 StartZ=0 EndX=394.073 EndY=52.2206 EndZ=0
    g78: LineSegment StartX=388.073 StartY=48.2206 StartZ=0 EndX=388.073 EndY=58.2206 EndZ=0
    g79: ArcOfCircle CenterX=385.073 CenterY=61.2206 CenterZ=0 NormalX=0 NormalY=0 NormalZ=1 AngleXU=0 Radius=4.24264 StartAngle=5.49779 EndAngle=10.2102
    g80: ArcOfCircle CenterX=397.073 CenterY=55.2206 CenterZ=0 NormalX=0 NormalY=0 NormalZ=1 AngleXU=0 Radius=4.24264 StartAngle=5.49779 EndAngle=10.2102
    g81: LineSegment StartX=382.073 StartY=58.2206 StartZ=0 EndX=382.073 EndY=48.2206 EndZ=0
    g82: LineSegment StartX=400.073 StartY=52.2206 StartZ=0 EndX=400.073 EndY=48.2206 EndZ=0
    g83: LineSegment StartX=394.073 StartY=48.2206 StartZ=0 EndX=388.073 EndY=48.2206 EndZ=0
    g84: LineSegment StartX=306.073 StartY=-40.8935 StartZ=0 EndX=306.073 EndY=-27.5935 EndZ=0
    g85: LineSegment StartX=318.073 StartY=-27.5935 StartZ=0 EndX=318.073 EndY=-47.4805 EndZ=0
    g86: LineSegment StartX=306.073 StartY=-27.5935 StartZ=0 EndX=310.073 EndY=-27.5935 EndZ=0
    g87: LineSegment StartX=318.073 StartY=-27.5935 StartZ=0 EndX=314.073 EndY=-27.5935 EndZ=0
    g88: LineSegment StartX=310.073 StartY=-27.5935 StartZ=0 EndX=310.073 EndY=-31.5935 EndZ=0
    g89: LineSegment StartX=314.073 StartY=-27.5935 StartZ=0 EndX=314.073 EndY=-31.5935 EndZ=0
    g90: ArcOfCircle CenterX=312.073 CenterY=-33.5935 CenterZ=0 NormalX=0 NormalY=0 NormalZ=1 AngleXU=0 Radius=2.82843 StartAngle=2.35619 EndAngle=7.06858
  constraints (121):
    c: Distance(g44) = 2.41
    c: Block(g44)
    c: Coincident(g46,g44)
    c: Coincident(g49,g36)
    c: Horizontal(g49)
    c: Block(g49)
    c: Coincident(g50,g45)
    c: Block(g50)
    c: Coincident(g51,g6)
    c: Block(g51)
    c: Coincident(g54,g52)
    c: Coincident(g54,g53)
    c: Coincident(g58,g56)
    c: Coincident(g58,g57)
    c: Vertical(g58)
    c: Coincident(g59,g56)
    c: Coincident(g59,g55)
    c: Coincident(g60,g55)
    c: Coincident(g60,g57)
    c: Horizontal(g60)
    c: Block(g61)
    c: Block(g62)
    c: Coincident(g63,g44)
    c: Coincident(g63,g62)
    c: Coincident(g64,g61)
    c: Coincident(g65,g61)
    c: Coincident(g65,g62)
    c: Vertical(g65)
    c: Block(g66)
    c: Coincident(g66,g50)
    c: Coincident(g67,g66)
    c: Coincident(g67,g43)
    c: Horizontal(g67)
    c: Coincident(g68,g51)
    c: Perpendicular(g68,g51)
    c: Coincident(g69,g64)
    c: Coincident(g70,g68)
    c: Distance(g70) = 3
    c: Distance(g71) = 3
    c: Perpendicular(g68,g70)
    c: Coincident(g72,g70)
    c: Coincident(g72,g71)
    c: Block(g72)
    c: Block(g69)
    c: Block(g71)
    c: Block(g54)
    c: Block(g59)
    c: Block(g58)
    c: Block(g60)
    c: Block(g67)
    c: Block(g43)
    c: Block(g36)
    c: Block(g48)
    c: Block(g46)
    c: Block(g47)
    c: Block(g45)
    c: Block(g35)
    c: Block(g34)
    c: Block(g0)
    c: Block(g33)
    c: Block(g52)
    c: Block(g6)
    c: Block(g41)
    c: Block(g57)
    c: Block(g55)
    c: Block(g53)
    c: Block(g68)
    c: Distance(g48) = 2.76
    c: Distance(g47) = 6.6
    c: Distance(g45) = 2.36657
    c: Coincident(g73,g49)
    c: Vertical(g73)
    c: Distance(g73) = 152
    c: Coincident(g74,g53)
    c: Vertical(g74)
    c: Block(g74)
    c: Coincident(g75,g74)
    c: Horizontal(g75)
    c: Distance(g75) = 7
    c: Horizontal(g76)
    c: Distance(g76) = 7
    c: Coincident(g76,g73)
    c: Vertical(g77)
    c: Distance(g77) = 4
    c: Vertical(g78)
    c: Distance(g78) = 10
    c: Coincident(g79,g78)
    c: Coincident(g80,g77)
    c: Block(g80)
    c: Block(g79)
    c: Coincident(g81,g79)
    c: Coincident(g81,g75)
    c: Vertical(g81)
    c: Coincident(g82,g80)
    c: Coincident(g82,g76)
    c: Vertical(g82)
    c: Coincident(g83,g77)
    c: Coincident(g83,g78)
    c: Horizontal(g83)
    c: Coincident(g84,g6)
    c: Vertical(g84)
    c: Distance(g84) = 13.3
    c: Coincident(g85,g52)
    c: Vertical(g85)
    c: Block(g85)
    c: Coincident(g86,g84)
    c: Horizontal(g86)
    c: Distance(g86) = 4
    c: Coincident(g87,g85)
    c: Horizontal(g87)
    c: Distance(g87) = 4
    c: Coincident(g88,g86)
    c: Vertical(g88)
    c: Coincident(g89,g87)
    c: Vertical(g89)
    c: Distance(g88) = 4
    c: Distance(g89) = 4
    c: Coincident(g90,g88)
    c: Coincident(g90,g89)
    c: Block(g90)
    c: Block(g56)
FEATURE [Sketcher::SketchObject] Sketch005  label="middleTop"
  FullyConstrained = true
  sketch-geometry (133):
    g0: Circle CenterX=175.025 CenterY=27.0667 CenterZ=0 NormalX=0 NormalY=0 NormalZ=1 AngleXU=0 Radius=1
    g1: Circle CenterX=179.022 CenterY=24.8665 CenterZ=0 NormalX=0 NormalY=0 NormalZ=1 AngleXU=0 Radius=1
    g2: Circle CenterX=179.022 CenterY=27.0606 CenterZ=0 NormalX=0 NormalY=0 NormalZ=1 AngleXU=0 Radius=1
    g3: BSplineCurve PolesCount=3 KnotsCount=2 Degree=2 IsPeriodic=0
    g4: GeomPoint X=175.025 Y=27.0667 Z=0
    g5: GeomPoint X=179.022 Y=27.0606 Z=0
    g6: Circle CenterX=189.124 CenterY=27.0628 CenterZ=0 NormalX=0 NormalY=0 NormalZ=1 AngleXU=0 Radius=1
    g7: Circle CenterX=185.124 CenterY=24.8665 CenterZ=0 NormalX=0 NormalY=0 NormalZ=1 AngleXU=0 Radius=1
    g8: Circle CenterX=185.124 CenterY=27.0606 CenterZ=0 NormalX=0 NormalY=0 NormalZ=1 AngleXU=0 Radius=1
    g9: BSplineCurve PolesCount=3 KnotsCount=2 Degree=2 IsPeriodic=0
    g10: GeomPoint X=189.124 Y=27.0628 Z=0
    g11: GeomPoint X=185.124 Y=27.0606 Z=0
    g12: Circle CenterX=165.871 CenterY=18.1458 CenterZ=0 NormalX=0 NormalY=0 NormalZ=1 AngleXU=0 Radius=1
    g13: Circle CenterX=169.377 CenterY=16.2206 CenterZ=0 NormalX=0 NormalY=0 NormalZ=1 AngleXU=0 Radius=1
    g14: Circle CenterX=165.871 CenterY=14.2956 CenterZ=0 NormalX=0 NormalY=0 NormalZ=1 AngleXU=0 Radius=1
    g15: BSplineCurve PolesCount=3 KnotsCount=2 Degree=2 IsPeriodic=0
    g16: GeomPoint X=165.871 Y=18.1458 Z=0
    g17: GeomPoint X=165.871 Y=14.2956 Z=0
    g18: Circle CenterX=198.275 CenterY=18.1318 CenterZ=0 NormalX=0 NormalY=0 NormalZ=1 AngleXU=0 Radius=1
    g19: Circle CenterX=194.768 CenterY=16.2206 CenterZ=0 NormalX=0 NormalY=0 NormalZ=1 AngleXU=0 Radius=1
    g20: Circle CenterX=198.264 CenterY=14.2963 CenterZ=0 NormalX=0 NormalY=0 NormalZ=1 AngleXU=0 Radius=1
    g21: BSplineCurve PolesCount=3 KnotsCount=2 Degree=2 IsPeriodic=0
    g22: GeomPoint X=198.275 Y=18.1318 Z=0
    g23: GeomPoint X=198.264 Y=14.2963 Z=0
    g24: Circle CenterX=125.607 CenterY=54.1951 CenterZ=0 NormalX=0 NormalY=0 NormalZ=1 AngleXU=0 Radius=1
    g25: Circle CenterX=139.632 CenterY=46.4944 CenterZ=0 NormalX=0 NormalY=0 NormalZ=1 AngleXU=0 Radius=1
    g26: Circle CenterX=127.326 CenterY=56.7187 CenterZ=0 NormalX=0 NormalY=0 NormalZ=1 AngleXU=0 Radius=1
    g27: BSplineCurve PolesCount=3 KnotsCount=2 Degree=2 IsPeriodic=0
    g28: GeomPoint X=125.607 Y=54.1951 Z=0
    g29: GeomPoint X=127.326 Y=56.7187 Z=0
    g30: Circle CenterX=236.824 CenterY=56.7187 CenterZ=0 NormalX=0 NormalY=0 NormalZ=1 AngleXU=0 Radius=1
    g31: Circle CenterX=224.513 CenterY=46.4944 CenterZ=0 NormalX=0 NormalY=0 NormalZ=1 AngleXU=0 Radius=1
    g32: Circle CenterX=238.538 CenterY=54.1951 CenterZ=0 NormalX=0 NormalY=0 NormalZ=1 AngleXU=0 Radius=1
    g33: BSplineCurve PolesCount=3 KnotsCount=2 Degree=2 IsPeriodic=0
    g34: GeomPoint X=236.824 Y=56.7187 Z=0
    g35: GeomPoint X=238.538 Y=54.1951 Z=0
    g36: Circle CenterX=189.121 CenterY=124.221 CenterZ=0 NormalX=0 NormalY=0 NormalZ=1 AngleXU=0 Radius=1
    g37: Circle CenterX=185.124 CenterY=124.221 CenterZ=0 NormalX=0 NormalY=0 NormalZ=1 AngleXU=0 Radius=1
    g38: Circle CenterX=185.124 CenterY=120.221 CenterZ=0 NormalX=0 NormalY=0 NormalZ=1 AngleXU=0 Radius=1
    g39: BSplineCurve PolesCount=3 KnotsCount=2 Degree=2 IsPeriodic=0
    g40: GeomPoint X=189.121 Y=124.221 Z=0
    g41: GeomPoint X=185.124 Y=120.221 Z=0
    g42: Circle CenterX=175.022 CenterY=124.221 CenterZ=0 NormalX=0 NormalY=0 NormalZ=1 AngleXU=0 Radius=1
    g43: Circle CenterX=179.022 CenterY=124.221 CenterZ=0 NormalX=0 NormalY=0 NormalZ=1 AngleXU=0 Radius=1
    g44: Circle CenterX=179.022 CenterY=120.221 CenterZ=0 NormalX=0 NormalY=0 NormalZ=1 AngleXU=0 Radius=1
    g45: BSplineCurve PolesCount=3 KnotsCount=2 Degree=2 IsPeriodic=0
    g46: GeomPoint X=175.022 Y=124.221 Z=0
    g47: GeomPoint X=179.022 Y=120.221 Z=0
    g48: LineSegment StartX=232.071 StartY=124.221 StartZ=0 EndX=232.071 EndY=127.221 EndZ=0
    g49-g52: Circle x4 (B-spline internal-alignment scaffolding for g53; pole/knot coordinates omitted)
    g53: BSplineCurve PolesCount=5 KnotsCount=3 Degree=3 IsPeriodic=0
    g54: GeomPoint X=232.072 Y=133.221 Z=0
    g55: GeomPoint X=223.072 Y=130.221 Z=0
    g56: GeomPoint X=232.071 Y=127.221 Z=0
    g57-g61: Circle x5 (B-spline internal-alignment scaffolding for g62; pole/knot coordinates omitted)
    g62: BSplineCurve PolesCount=5 KnotsCount=3 Degree=3 IsPeriodic=0
    g63: GeomPoint X=132.072 Y=133.221 Z=0
    g64: GeomPoint X=141.072 Y=130.221 Z=0
    g65: GeomPoint X=132.072 Y=127.221 Z=0
    g66: ArcOfCircle CenterX=247.391 CenterY=52.0843 CenterZ=0 NormalX=0 NormalY=0 NormalZ=1 AngleXU=0 Radius=4.24264 StartAngle=4.42912 EndAngle=9.14151
    g67: LineSegment StartX=240.687 StartY=51.8263 StartZ=0 EndX=239.192 EndY=54.5542 EndZ=0
    g68: LineSegment StartX=243.575 StartY=46.5669 StartZ=0 EndX=245.072 EndY=43.8408 EndZ=0
    g69: LineSegment StartX=240.168 StartY=69.471 StartZ=0 EndX=241.708 EndY=67.6172 EndZ=0
    g70: LineSegment StartX=246.783 StartY=71.8328 StartZ=0 EndX=248.546 EndY=69.7098 EndZ=0
    g71: LineSegment StartX=245.073 StartY=63.5726 StartZ=0 EndX=243.476 EndY=65.4955 EndZ=0
    g72: LineSegment StartX=123.967 StartY=69.4706 StartZ=0 EndX=122.37 EndY=67.5474 EndZ=0
    g73: LineSegment StartX=232.072 StartY=133.221 StartZ=0 EndX=232.072 EndY=136.221 EndZ=0
    g74: LineSegment StartX=232.072 StartY=136.221 StartZ=0 EndX=132.072 EndY=136.221 EndZ=0
    g75: LineSegment StartX=132.072 StartY=136.221 StartZ=0 EndX=132.072 EndY=133.221 EndZ=0
    g76: LineSegment StartX=132.072 StartY=127.221 StartZ=0 EndX=132.072 EndY=124.221 EndZ=0
    g77: LineSegment StartX=132.072 StartY=124.221 StartZ=0 EndX=175.022 EndY=124.221 EndZ=0
    g78: LineSegment StartX=189.121 StartY=124.221 StartZ=0 EndX=232.071 EndY=124.221 EndZ=0
    g79: LineSegment StartX=185.124 StartY=120.221 StartZ=0 EndX=185.124 EndY=27.0606 EndZ=0
    g80: LineSegment StartX=189.124 StartY=27.0628 StartZ=0 EndX=240.168 EndY=69.471 EndZ=0
    g81: LineSegment StartX=241.708 StartY=67.6172 StartZ=0 EndX=246.783 EndY=71.8328 EndZ=0
    g82: LineSegment StartX=248.546 StartY=69.7098 StartZ=0 EndX=243.476 EndY=65.4955 EndZ=0
    g83: LineSegment StartX=245.073 StartY=63.5726 StartZ=0 EndX=236.824 EndY=56.7187 EndZ=0
    g84: LineSegment StartX=238.538 StartY=54.1951 StartZ=0 EndX=239.192 EndY=54.5542 EndZ=0
    g85: LineSegment StartX=240.687 StartY=51.8263 StartZ=0 EndX=243.317 EndY=53.2701 EndZ=0
    g86: LineSegment StartX=246.205 StartY=48.0108 StartZ=0 EndX=243.575 EndY=46.5669 EndZ=0
    g87: LineSegment StartX=245.072 StartY=43.8408 StartZ=0 EndX=198.275 EndY=18.1318 EndZ=0
    g88: LineSegment StartX=165.871 StartY=18.1458 StartZ=0 EndX=118.934 EndY=43.9178 EndZ=0
    g89: LineSegment StartX=118.934 StartY=43.9178 StartZ=0 EndX=120.377 EndY=46.5474 EndZ=0
    g90: LineSegment StartX=117.748 StartY=47.9913 StartZ=0 EndX=120.377 EndY=46.5474 EndZ=0
    g91: LineSegment StartX=120.635 StartY=53.2507 StartZ=0 EndX=123.265 EndY=51.8068 EndZ=0
    g92: LineSegment StartX=123.265 StartY=51.8068 StartZ=0 EndX=124.73 EndY=54.6766 EndZ=0
    g93: ArcOfCircle CenterX=116.562 CenterY=52.0649 CenterZ=0 NormalX=0 NormalY=0 NormalZ=1 AngleXU=0 Radius=4.24264 StartAngle=0.283267 EndAngle=4.99566
    g94: LineSegment StartX=124.73 StartY=54.6766 StartZ=0 EndX=125.607 EndY=54.1951 EndZ=0
    g95: LineSegment StartX=127.326 StartY=56.7187 StartZ=0 EndX=119.072 EndY=63.5741 EndZ=0
    g96: LineSegment StartX=119.072 StartY=63.5741 StartZ=0 EndX=120.669 EndY=65.4973 EndZ=0
    g97: LineSegment StartX=120.669 StartY=65.4973 StartZ=0 EndX=115.591 EndY=69.7147 EndZ=0
    g98: LineSegment StartX=115.591 StartY=69.7147 StartZ=0 EndX=117.293 EndY=71.7641 EndZ=0
    g99: LineSegment StartX=117.293 StartY=71.7641 StartZ=0 EndX=122.37 EndY=67.5474 EndZ=0
    g100: LineSegment StartX=123.967 StartY=69.4706 StartZ=0 EndX=175.025 EndY=27.0667 EndZ=0
    g101: LineSegment StartX=179.022 StartY=27.0606 StartZ=0 EndX=179.022 EndY=120.221 EndZ=0
    g102-g117: Circle x16 (B-spline internal-alignment scaffolding for g118; pole/knot coordinates omitted)
    g118: BSplineCurve PolesCount=16 KnotsCount=14 Degree=3 IsPeriodic=0
    g119-g132: GeomPoint x14 (B-spline internal-alignment scaffolding for g118; pole/knot coordinates omitted)
  constraints (180):
    c: Weight(g0) = 1
    c: Equal(g0,g1)
    c: Equal(g0,g2)
    c: InternalAlignment(g0,g3)
    c: InternalAlignment(g1,g3)
    c: InternalAlignment(g2,g3)
    c: InternalAlignment(g4,g3)
    c: InternalAlignment(g5,g3)
    c: Weight(g6) = 1
    c: Equal(g6,g7)
    c: Equal(g6,g8)
    c: InternalAlignment(g6,g9)
    c: InternalAlignment(g7,g9)
    c: InternalAlignment(g8,g9)
    c: InternalAlignment(g10,g9)
    c: InternalAlignment(g11,g9)
    c: Block(g9)
    c: Block(g3)
    c: Weight(g12) = 1
    c: Equal(g12,g13)
    c: Equal(g12,g14)
    c: InternalAlignment(g12,g15)
    c: InternalAlignment(g13,g15)
    c: InternalAlignment(g14,g15)
    c: InternalAlignment(g16,g15)
    c: InternalAlignment(g17,g15)
    c: Weight(g18) = 1
    c: Equal(g18,g19)
    c: Equal(g18,g20)
    c: InternalAlignment(g18,g21)
    c: InternalAlignment(g19,g21)
    c: InternalAlignment(g20,g21)
    c: InternalAlignment(g22,g21)
    c: InternalAlignment(g23,g21)
    c: Block(g15)
    c: Block(g21)
    c: Weight(g24) = 1
    c: Equal(g24,g25)
    c: Equal(g24,g26)
    c: InternalAlignment(g24,g27)
    c: InternalAlignment(g25,g27)
    c: InternalAlignment(g26,g27)
    c: InternalAlignment(g28,g27)
    c: InternalAlignment(g29,g27)
    c: Block(g27)
    c: Weight(g30) = 1
    c: Equal(g30,g31)
    c: Equal(g30,g32)
    c: InternalAlignment(g30,g33)
    c: InternalAlignment(g31,g33)
    c: InternalAlignment(g32,g33)
    c: InternalAlignment(g34,g33)
    c: InternalAlignment(g35,g33)
    c: Block(g33)
    c: Weight(g36) = 1
    c: Equal(g36,g37)
    c: Equal(g36,g38)
    c: InternalAlignment(g36,g39)
    c: InternalAlignment(g37,g39)
    c: InternalAlignment(g38,g39)
    c: InternalAlignment(g40,g39)
    c: InternalAlignment(g41,g39)
    c: Weight(g42) = 1
    c: Equal(g42,g43)
    c: Equal(g42,g44)
    c: InternalAlignment(g42,g45)
    c: InternalAlignment(g43,g45)
    c: InternalAlignment(g44,g45)
    c: InternalAlignment(g46,g45)
    c: InternalAlignment(g47,g45)
    c: Block(g45)
    c: Block(g39)
    c: Vertical(g48)
    c: Distance(g48) = 3
    c: Weight(g49) = 1
    c: Equal(g49,g50)
    c: Equal(g49,g51)
    c: Equal(g49,g52)
    c: Coincident(g53,g48)
    c: InternalAlignment(g49-g52 -> g53) x4
    c: InternalAlignment(g54,g53)
    c: InternalAlignment(g55,g53)
    c: InternalAlignment(g56,g53)
    c: Weight(g57) = 1
    c: Equal(g57, g58-g61) x4
    c: InternalAlignment(g57-g61 -> g62) x5
    c: InternalAlignment(g63,g62)
    c: InternalAlignment(g64,g62)
    c: InternalAlignment(g65,g62)
    c: Block(g62)
    c: Block(g67)
    c: Block(g68)
    c: Distance(g69) = 2.41
    c: Distance(g70) = 2.76
    c: Distance(g71) = 2.5
    c: Distance(g72) = 2.5
    c: Block(g66)
    c: Block(g48)
    c: Block(g53)
    c: Coincident(g73,g53)
    c: Vertical(g73)
    c: Distance(g73) = 3
    c: Coincident(g74,g73)
    c: Horizontal(g74)
    c: Distance(g74) = 100
    c: Coincident(g75,g74)
    c: Coincident(g75,g62)
    c: Vertical(g75)
    c: Distance(g75) = 3
    c: Coincident(g76,g62)
    c: Vertical(g76)
    c: Distance(g76) = 3
    c: Coincident(g77,g76)
    c: Coincident(g77,g45)
    c: Horizontal(g77)
    c: Distance(g77) = 42.95
    c: Coincident(g78,g39)
    c: Coincident(g78,g48)
    c: Horizontal(g78)
    c: Distance(g78) = 42.95
    c: Coincident(g79,g39)
    c: Coincident(g79,g9)
    c: Vertical(g79)
    c: Distance(g79) = 93.16
    c: Coincident(g80,g9)
    c: Coincident(g80,g69)
    c: Angle(g80) = 0.693245
    c: Block(g80)
    c: Coincident(g81,g69)
    c: Coincident(g81,g70)
    c: Block(g81)
    c: Coincident(g82,g70)
    c: Coincident(g82,g71)
    c: Block(g82)
    c: Coincident(g83,g71)
    c: Coincident(g83,g33)
    c: Block(g71)
    c: Coincident(g84,g33)
    c: Coincident(g84,g67)
    c: Coincident(g85,g67)
    c: Coincident(g85,g66)
    c: Coincident(g86,g66)
    c: Coincident(g86,g68)
    c: Coincident(g87,g68)
    c: Coincident(g87,g21)
    c: Coincident(g88,g15)
    c: Coincident(g89,g88)
    c: Block(g89)
    c: Coincident(g90,g89)
    c: Block(g90)
    c: Block(g91)
    c: Coincident(g92,g91)
    c: Block(g92)
    c: Coincident(g93,g91)
    c: Coincident(g93,g90)
    c: Block(g93)
    c: Coincident(g94,g92)
    c: Coincident(g94,g27)
    c: Coincident(g95,g27)
    c: Block(g95)
    c: Coincident(g96,g95)
    c: Coincident(g97,g96)
    c: Coincident(g98,g97)
    c: Coincident(g99,g98)
    c: Coincident(g99,g72)
    c: Block(g98)
    c: Block(g96)
    c: Block(g72)
    c: Coincident(g100,g72)
    c: Coincident(g100,g3)
    c: Coincident(g101,g3)
    c: Coincident(g101,g45)
    c: Vertical(g101)
    c: Coincident(g118,g21)
    c: Weight(g102) = 1
    c: Equal(g102, g103-g117) x15
    c: Coincident(g118,g15)
    c: InternalAlignment(g102-g117 -> g118) x16
    c: InternalAlignment(g119-g132 -> g118) x14
    c: Block(g118)
FEATURE [Sketcher::SketchObject] Sketch006  label="leftSideTop"
  FullyConstrained = true
  sketch-geometry (99):
    g0: Circle CenterX=61.1495 CenterY=111.695 CenterZ=0 NormalX=0 NormalY=0 NormalZ=1 AngleXU=0 Radius=1
    g1: Circle CenterX=58.0728 CenterY=114.251 CenterZ=0 NormalX=0 NormalY=0 NormalZ=1 AngleXU=0 Radius=1
    g2: Circle CenterX=58.0728 CenterY=110.251 CenterZ=0 NormalX=0 NormalY=0 NormalZ=1 AngleXU=0 Radius=1
    g3: BSplineCurve PolesCount=3 KnotsCount=2 Degree=2 IsPeriodic=0
    g4: GeomPoint X=61.1495 Y=111.695 Z=0
    g5: GeomPoint X=58.0728 Y=110.251 Z=0
    g6: Circle CenterX=61.5791 CenterY=89.3511 CenterZ=0 NormalX=0 NormalY=0 NormalZ=1 AngleXU=0 Radius=1
    g7: Circle CenterX=58.0728 CenterY=91.2763 CenterZ=0 NormalX=0 NormalY=0 NormalZ=1 AngleXU=0 Radius=1
    g8: Circle CenterX=58.0728 CenterY=95.2763 CenterZ=0 NormalX=0 NormalY=0 NormalZ=1 AngleXU=0 Radius=1
    g9: BSplineCurve PolesCount=3 KnotsCount=2 Degree=2 IsPeriodic=0
    g10: GeomPoint X=61.5791 Y=89.3511 Z=0
    g11: GeomPoint X=58.0728 Y=95.2763 Z=0
    g12: Circle CenterX=62.0728 CenterY=124.221 CenterZ=0 NormalX=0 NormalY=0 NormalZ=1 AngleXU=0 Radius=1
    g13: Circle CenterX=58.0728 CenterY=124.221 CenterZ=0 NormalX=0 NormalY=0 NormalZ=1 AngleXU=0 Radius=1
    g14: Circle CenterX=61.1496 CenterY=121.665 CenterZ=0 NormalX=0 NormalY=0 NormalZ=1 AngleXU=0 Radius=1
    g15: BSplineCurve PolesCount=3 KnotsCount=2 Degree=2 IsPeriodic=0
    g16: GeomPoint X=62.0728 Y=124.221 Z=0
    g17: GeomPoint X=61.1496 Y=121.665 Z=0
    g18: Circle CenterX=61.5791 CenterY=75.4095 CenterZ=0 NormalX=0 NormalY=0 NormalZ=1 AngleXU=0 Radius=1
    g19: Circle CenterX=58.0728 CenterY=77.3346 CenterZ=0 NormalX=0 NormalY=0 NormalZ=1 AngleXU=0 Radius=1
    g20: Circle CenterX=58.0728 CenterY=73.3346 CenterZ=0 NormalX=0 NormalY=0 NormalZ=1 AngleXU=0 Radius=1
    g21: BSplineCurve PolesCount=3 KnotsCount=2 Degree=2 IsPeriodic=0
    g22: GeomPoint X=61.5791 Y=75.4095 Z=0
    g23: GeomPoint X=58.0728 Y=73.3346 Z=0
    g24: Circle CenterX=2.07281 CenterY=124.221 CenterZ=0 NormalX=0 NormalY=0 NormalZ=1 AngleXU=0 Radius=1
    g25: Circle CenterX=1.57905 CenterY=122.295 CenterZ=0 NormalX=0 NormalY=0 NormalZ=1 AngleXU=0 Radius=1
    g26: BSplineCurve PolesCount=3 KnotsCount=2 Degree=2 IsPeriodic=0
    g27: GeomPoint X=2.07281 Y=124.221 Z=0
    g28: GeomPoint X=1.57905 Y=122.295 Z=0
    g29: Circle CenterX=46.0728 CenterY=124.221 CenterZ=0 NormalX=0 NormalY=0 NormalZ=1 AngleXU=0 Radius=1
    g30: Circle CenterX=46.0728 CenterY=120.221 CenterZ=0 NormalX=0 NormalY=0 NormalZ=1 AngleXU=0 Radius=1
    g31: BSplineCurve PolesCount=3 KnotsCount=2 Degree=2 IsPeriodic=0
    g32: GeomPoint X=42.0728 Y=124.221 Z=0
    g33: GeomPoint X=46.0728 Y=120.221 Z=0
    g34: Circle CenterX=46.0728 CenterY=109.865 CenterZ=0 NormalX=0 NormalY=0 NormalZ=1 AngleXU=0 Radius=1
    g35: Circle CenterX=46.0728 CenterY=105.865 CenterZ=0 NormalX=0 NormalY=0 NormalZ=1 AngleXU=0 Radius=1
    g36: Circle CenterX=42.0728 CenterY=105.865 CenterZ=0 NormalX=0 NormalY=0 NormalZ=1 AngleXU=0 Radius=1
    g37: BSplineCurve PolesCount=3 KnotsCount=2 Degree=2 IsPeriodic=0
    g38: GeomPoint X=46.0728 Y=109.865 Z=0
    g39: GeomPoint X=42.0728 Y=105.865 Z=0
    g40: Circle CenterX=35.5028 CenterY=105.865 CenterZ=0 NormalX=0 NormalY=0 NormalZ=1 AngleXU=0 Radius=1
    g41: Circle CenterX=31.5028 CenterY=105.865 CenterZ=0 NormalX=0 NormalY=0 NormalZ=1 AngleXU=0 Radius=1
    g42: Circle CenterX=27.9965 CenterY=107.79 CenterZ=0 NormalX=0 NormalY=0 NormalZ=1 AngleXU=0 Radius=1
    g43: BSplineCurve PolesCount=3 KnotsCount=2 Degree=2 IsPeriodic=0
    g44: GeomPoint X=35.5028 Y=105.865 Z=0
    g45: GeomPoint X=27.9965 Y=107.79 Z=0
    g46-g50: Circle x5 (B-spline internal-alignment scaffolding for g51; pole/knot coordinates omitted)
    g51: BSplineCurve PolesCount=5 KnotsCount=3 Degree=3 IsPeriodic=0
    g52: GeomPoint X=132.072 Y=133.221 Z=0
    g53: GeomPoint X=141.072 Y=130.221 Z=0
    g54: GeomPoint X=132.072 Y=127.221 Z=0
    g55: ArcOfCircle CenterX=116.562 CenterY=52.0649 CenterZ=0 NormalX=0 NormalY=0 NormalZ=1 AngleXU=0 Radius=4.24264 StartAngle=0.283268 EndAngle=4.99566
    g56: LineSegment StartX=123.967 StartY=69.4706 StartZ=0 EndX=122.37 EndY=67.5474 EndZ=0
    g57: LineSegment StartX=117.293 StartY=71.7641 StartZ=0 EndX=115.591 EndY=69.7147 EndZ=0
    g58: LineSegment StartX=120.669 StartY=65.4973 StartZ=0 EndX=119.072 EndY=63.5741 EndZ=0
    g59: LineSegment StartX=124.73 StartY=54.6766 StartZ=0 EndX=123.265 EndY=51.8068 EndZ=0
    g60: LineSegment StartX=120.377 StartY=46.5474 StartZ=0 EndX=118.934 EndY=43.9178 EndZ=0
    g61: BSplineCurve PolesCount=3 KnotsCount=2 Degree=2 IsPeriodic=0
    g62: BSplineCurve PolesCount=3 KnotsCount=2 Degree=2 IsPeriodic=0
    g63: LineSegment StartX=61.5791 StartY=75.4095 StartZ=0 EndX=118.934 EndY=43.9178 EndZ=0
    g64: LineSegment StartX=117.748 StartY=47.9913 StartZ=0 EndX=120.377 EndY=46.5474 EndZ=0
    g65: LineSegment StartX=120.635 StartY=53.2507 StartZ=0 EndX=123.265 EndY=51.8068 EndZ=0
    g66: LineSegment StartX=124.73 StartY=54.6766 StartZ=0 EndX=61.5791 EndY=89.3511 EndZ=0
    g67: LineSegment StartX=58.0728 StartY=95.2763 StartZ=0 EndX=58.0728 EndY=110.251 EndZ=0
    g68: LineSegment StartX=61.1495 StartY=111.695 StartZ=0 EndX=119.072 EndY=63.5741 EndZ=0
    g69: LineSegment StartX=120.669 StartY=65.4973 StartZ=0 EndX=115.591 EndY=69.7147 EndZ=0
    g70: LineSegment StartX=117.293 StartY=71.7641 StartZ=0 EndX=122.37 EndY=67.5474 EndZ=0
    g71: LineSegment StartX=123.967 StartY=69.4706 StartZ=0 EndX=61.1496 EndY=121.665 EndZ=0
    g72: LineSegment StartX=62.0728 StartY=124.221 StartZ=0 EndX=132.072 EndY=124.221 EndZ=0
    g73: LineSegment StartX=132.072 StartY=127.221 StartZ=0 EndX=132.072 EndY=124.221 EndZ=0
    g74: LineSegment StartX=132.072 StartY=133.221 StartZ=0 EndX=132.072 EndY=136.221 EndZ=0
    g75: LineSegment StartX=132.072 StartY=136.221 StartZ=0 EndX=-42.9272 EndY=136.221 EndZ=0
    g76: LineSegment StartX=2.07281 StartY=124.221 StartZ=0 EndX=42.0728 EndY=124.221 EndZ=0
    g77: LineSegment StartX=46.0728 StartY=120.221 StartZ=0 EndX=46.0728 EndY=109.865 EndZ=0
    g78: LineSegment StartX=42.0728 StartY=105.865 StartZ=0 EndX=35.5028 EndY=105.865 EndZ=0
    g79: LineSegment StartX=27.9965 StartY=107.79 StartZ=0 EndX=1.57905 EndY=122.295 EndZ=0
    g80: LineSegment StartX=-6.92718 StartY=76.4095 StartZ=0 EndX=42.0728 EndY=76.4095 EndZ=0
    g81: LineSegment StartX=-17.9272 StartY=48.2206 StartZ=0 EndX=-17.9272 EndY=58.2206 EndZ=0
    g82: LineSegment StartX=-35.9272 StartY=48.2206 StartZ=0 EndX=-35.9272 EndY=52.2206 EndZ=0
    g83: LineSegment StartX=-29.9272 StartY=48.2206 StartZ=0 EndX=-29.9272 EndY=52.2206 EndZ=0
    g84: LineSegment StartX=-23.9272 StartY=48.2206 StartZ=0 EndX=-23.9272 EndY=58.2206 EndZ=0
    g85: ArcOfCircle CenterX=-32.9272 CenterY=55.2206 CenterZ=0 NormalX=0 NormalY=0 NormalZ=1 AngleXU=0 Radius=4.24264 StartAngle=5.49779 EndAngle=10.2102
    g86: ArcOfCircle CenterX=-20.9272 CenterY=61.2206 CenterZ=0 NormalX=0 NormalY=0 NormalZ=1 AngleXU=0 Radius=4.24264 StartAngle=5.49779 EndAngle=10.2102
    g87: LineSegment StartX=-10.9272 StartY=48.2206 StartZ=0 EndX=-10.9272 EndY=72.4095 EndZ=0
    g88: LineSegment StartX=-42.9272 StartY=48.2206 StartZ=0 EndX=-42.9272 EndY=136.221 EndZ=0
    g89: LineSegment StartX=46.0728 StartY=72.4095 StartZ=0 EndX=46.0728 EndY=-27.5905 EndZ=0
    g90: LineSegment StartX=58.0728 StartY=-27.5905 StartZ=0 EndX=58.0728 EndY=73.3346 EndZ=0
    g91: LineSegment StartX=50.0728 StartY=-27.5905 StartZ=0 EndX=50.0728 EndY=-31.5905 EndZ=0
    g92: LineSegment StartX=54.0728 StartY=-27.5905 StartZ=0 EndX=54.0728 EndY=-31.5905 EndZ=0
    g93: ArcOfCircle CenterX=52.0728 CenterY=-33.5905 CenterZ=0 NormalX=0 NormalY=0 NormalZ=1 AngleXU=0 Radius=2.82843 StartAngle=2.35619 EndAngle=7.06858
    g94: LineSegment StartX=46.0728 StartY=-27.5905 StartZ=0 EndX=50.0728 EndY=-27.5905 EndZ=0
    g95: LineSegment StartX=54.0728 StartY=-27.5905 StartZ=0 EndX=58.0728 EndY=-27.5905 EndZ=0
    g96: LineSegment StartX=-17.9272 StartY=48.2206 StartZ=0 EndX=-10.9272 EndY=48.2206 EndZ=0
    g97: LineSegment StartX=-29.9272 StartY=48.2206 StartZ=0 EndX=-23.9272 EndY=48.2206 EndZ=0
    g98: LineSegment StartX=-42.9272 StartY=48.2206 StartZ=0 EndX=-35.9272 EndY=48.2206 EndZ=0
  constraints (172):
    c: Weight(g0) = 1
    c: Equal(g0,g1)
    c: Equal(g0,g2)
    c: InternalAlignment(g0,g3)
    c: InternalAlignment(g1,g3)
    c: InternalAlignment(g2,g3)
    c: InternalAlignment(g4,g3)
    c: InternalAlignment(g5,g3)
    c: Weight(g6) = 1
    c: Equal(g6,g7)
    c: Equal(g6,g8)
    c: InternalAlignment(g6,g9)
    c: InternalAlignment(g7,g9)
    c: InternalAlignment(g8,g9)
    c: InternalAlignment(g10,g9)
    c: InternalAlignment(g11,g9)
    c: Block(g3)
    c: Block(g9)
    c: Weight(g12) = 1
    c: Equal(g12,g13)
    c: Equal(g12,g14)
    c: InternalAlignment(g12,g15)
    c: InternalAlignment(g13,g15)
    c: InternalAlignment(g14,g15)
    c: InternalAlignment(g16,g15)
    c: InternalAlignment(g17,g15)
    c: Block(g15)
    c: Weight(g18) = 1
    c: Equal(g18,g19)
    c: Equal(g18,g20)
    c: InternalAlignment(g18,g21)
    c: InternalAlignment(g19,g21)
    c: InternalAlignment(g20,g21)
    c: InternalAlignment(g22,g21)
    c: InternalAlignment(g23,g21)
    c: Block(g21)
    c: Weight(g24) = 1
    c: Equal(g24,g25)
    c: InternalAlignment(g24,g26)
    c: InternalAlignment(g25,g26)
    c: InternalAlignment(g27,g26)
    c: InternalAlignment(g28,g26)
    c: InternalAlignment(g29,g31)
    c: InternalAlignment(g30,g31)
    c: InternalAlignment(g32,g31)
    c: InternalAlignment(g33,g31)
    c: Weight(g34) = 1
    c: Equal(g34,g35)
    c: Equal(g34,g36)
    c: InternalAlignment(g34,g37)
    c: InternalAlignment(g35,g37)
    c: InternalAlignment(g36,g37)
    c: InternalAlignment(g38,g37)
    c: InternalAlignment(g39,g37)
    c: Equal(g40,g41)
    c: Equal(g40,g42)
    c: InternalAlignment(g40,g43)
    c: InternalAlignment(g41,g43)
    c: InternalAlignment(g42,g43)
    c: InternalAlignment(g44,g43)
    c: InternalAlignment(g45,g43)
    c: Block(g31)
    c: Block(g37)
    c: Block(g43)
    c: Block(g26)
    c: Weight(g46) = 1
    c: Equal(g46, g47-g50) x4
    c: InternalAlignment(g46-g50 -> g51) x5
    c: InternalAlignment(g52,g51)
    c: InternalAlignment(g53,g51)
    c: InternalAlignment(g54,g51)
    c: Block(g51)
    c: Block(g55)
    c: Block(g56)
    c: Block(g57)
    c: Block(g58)
    c: Block(g59)
    c: Block(g60)
    c: Block(g61)
    c: Block(g62)
    c: Coincident(g90,g21)
    c: Coincident(g63,g21)
    c: Coincident(g63,g60)
    c: Coincident(g64,g55)
    c: Coincident(g64,g60)
    c: Coincident(g65,g55)
    c: Coincident(g65,g59)
    c: Coincident(g66,g59)
    c: Coincident(g66,g9)
    c: Coincident(g67,g9)
    c: Coincident(g67,g3)
    c: Vertical(g67)
    c: Coincident(g68,g3)
    c: Coincident(g68,g58)
    c: Coincident(g69,g58)
    c: Coincident(g69,g57)
    c: Coincident(g70,g57)
    c: Coincident(g70,g56)
    c: Coincident(g71,g56)
    c: Coincident(g71,g15)
    c: Coincident(g72,g15)
    c: Horizontal(g72)
    c: Coincident(g73,g51)
    c: Coincident(g73,g72)
    c: Vertical(g73)
    c: Coincident(g74,g51)
    c: Vertical(g74)
    c: Coincident(g75,g74)
    c: Horizontal(g75)
    c: Coincident(g76,g26)
    c: Coincident(g76,g31)
    c: Horizontal(g76)
    c: Coincident(g77,g31)
    c: Coincident(g77,g37)
    c: Vertical(g77)
    c: Coincident(g78,g37)
    c: Coincident(g78,g43)
    c: Horizontal(g78)
    c: Coincident(g79,g43)
    c: Coincident(g79,g26)
    c: Coincident(g80,g62)
    c: Coincident(g80,g61)
    c: Horizontal(g80)
    c: Vertical(g81)
    c: Distance(g81) = 10
    c: Vertical(g82)
    c: Distance(g82) = 4
    c: Vertical(g83)
    c: Distance(g83) = 4
    c: Vertical(g84)
    c: Distance(g84) = 10
    c: Coincident(g85,g83)
    c: Coincident(g85,g82)
    c: Block(g85)
    c: Coincident(g86,g84)
    c: Coincident(g86,g81)
    c: Block(g86)
    c: Coincident(g87,g62)
    c: Vertical(g87)
    c: Coincident(g88,g75)
    c: Vertical(g88)
    c: Block(g75)
    c: Coincident(g89,g61)
    c: Vertical(g89)
    c: Distance(g89) = 100
    c: Block(g90)
    c: Vertical(g91)
    c: Distance(g91) = 4
    c: Vertical(g92)
    c: Distance(g92) = 4
    c: Coincident(g93,g91)
    c: Coincident(g93,g92)
    c: Block(g93)
    c: Coincident(g94,g89)
    c: Coincident(g94,g91)
    c: Horizontal(g94)
    c: Distance(g94) = 4
    c: Coincident(g95,g92)
    c: Coincident(g95,g90)
    c: Horizontal(g95)
    c: Distance(g95) = 4
    c: Block(g87)
    c: Block(g88)
    c: Coincident(g96,g81)
    c: Coincident(g96,g87)
    c: Horizontal(g96)
    c: Coincident(g97,g83)
    c: Coincident(g97,g84)
    c: Horizontal(g97)
    c: Coincident(g98,g88)
    c: Coincident(g98,g82)
    c: Horizontal(g98)
FEATURE [Sketcher::SketchObject] Sketch007  label="leftSideBottom"
  FullyConstrained = true
  sketch-geometry (92):
    g0: ArcOfCircle CenterX=-26.9272 CenterY=-83.7794 CenterZ=0 NormalX=0 NormalY=0 NormalZ=1 AngleXU=0 Radius=8 StartAngle=3.14159 EndAngle=6.28319
    g1: Circle CenterX=61.5791 CenterY=-56.9099 CenterZ=0 NormalX=0 NormalY=0 NormalZ=1 AngleXU=0 Radius=1
    g2: Circle CenterX=58.0728 CenterY=-58.8351 CenterZ=0 NormalX=0 NormalY=0 NormalZ=1 AngleXU=0 Radius=1
    g3: Circle CenterX=58.0728 CenterY=-62.8351 CenterZ=0 NormalX=0 NormalY=0 NormalZ=1 AngleXU=0 Radius=1
    g4: BSplineCurve PolesCount=3 KnotsCount=2 Degree=2 IsPeriodic=0
    g5: GeomPoint X=61.5791 Y=-56.9099 Z=0
    g6: GeomPoint X=58.0728 Y=-62.8351 Z=0
    g7: Circle CenterX=58.0728 CenterY=-77.8102 CenterZ=0 NormalX=0 NormalY=0 NormalZ=1 AngleXU=0 Radius=1
    g8: Circle CenterX=58.0728 CenterY=-81.8102 CenterZ=0 NormalX=0 NormalY=0 NormalZ=1 AngleXU=0 Radius=1
    g9: Circle CenterX=61.1496 CenterY=-79.2541 CenterZ=0 NormalX=0 NormalY=0 NormalZ=1 AngleXU=0 Radius=1
    g10: BSplineCurve PolesCount=3 KnotsCount=2 Degree=2 IsPeriodic=0
    g11: GeomPoint X=58.0728 Y=-77.8102 Z=0
    g12: GeomPoint X=61.1496 Y=-79.2541 Z=0
    g13: Circle CenterX=61.6457 CenterY=-88.8112 CenterZ=0 NormalX=0 NormalY=0 NormalZ=1 AngleXU=0 Radius=1
    g14: Circle CenterX=58.0728 CenterY=-91.7794 CenterZ=0 NormalX=0 NormalY=0 NormalZ=1 AngleXU=0 Radius=1
    g15: Circle CenterX=63.9135 CenterY=-91.8014 CenterZ=0 NormalX=0 NormalY=0 NormalZ=1 AngleXU=0 Radius=1
    g16: BSplineCurve PolesCount=3 KnotsCount=2 Degree=2 IsPeriodic=0
    g17: GeomPoint X=61.6457 Y=-88.8112 Z=0
    g18: GeomPoint X=63.9135 Y=-91.8014 Z=0
    g19: Circle CenterX=58.0728 CenterY=-40.8935 CenterZ=0 NormalX=0 NormalY=0 NormalZ=1 AngleXU=0 Radius=1
    g20: Circle CenterX=58.0728 CenterY=-44.8935 CenterZ=0 NormalX=0 NormalY=0 NormalZ=1 AngleXU=0 Radius=1
    g21: Circle CenterX=61.5791 CenterY=-42.9683 CenterZ=0 NormalX=0 NormalY=0 NormalZ=1 AngleXU=0 Radius=1
    g22: BSplineCurve PolesCount=3 KnotsCount=2 Degree=2 IsPeriodic=0
    g23: GeomPoint X=58.0728 Y=-40.8935 Z=0
    g24: GeomPoint X=61.5791 Y=-42.9683 Z=0
    g25: Circle CenterX=42.5666 CenterY=-67.3492 CenterZ=0 NormalX=0 NormalY=0 NormalZ=1 AngleXU=0 Radius=1
    g26: Circle CenterX=46.0728 CenterY=-65.424 CenterZ=0 NormalX=0 NormalY=0 NormalZ=1 AngleXU=0 Radius=1
    g27: Circle CenterX=46.0728 CenterY=-69.424 CenterZ=0 NormalX=0 NormalY=0 NormalZ=1 AngleXU=0 Radius=1
    g28: BSplineCurve PolesCount=3 KnotsCount=2 Degree=2 IsPeriodic=0
    g29: GeomPoint X=42.5666 Y=-67.3492 Z=0
    g30: GeomPoint X=46.0728 Y=-69.424 Z=0
    g31: Circle CenterX=2.07281 CenterY=-91.7794 CenterZ=0 NormalX=0 NormalY=0 NormalZ=1 AngleXU=0 Radius=1
    g32: Circle CenterX=-1.92719 CenterY=-91.7794 CenterZ=0 NormalX=0 NormalY=0 NormalZ=1 AngleXU=0 Radius=1
    g33: Circle CenterX=1.57905 CenterY=-89.8542 CenterZ=0 NormalX=0 NormalY=0 NormalZ=1 AngleXU=0 Radius=1
    g34: BSplineCurve PolesCount=3 KnotsCount=2 Degree=2 IsPeriodic=0
    g35: GeomPoint X=2.07281 Y=-91.7794 Z=0
    g36: GeomPoint X=1.57905 Y=-89.8542 Z=0
    g37: ArcOfCircle CenterX=-26.9272 CenterY=22.1087 CenterZ=0 NormalX=0 NormalY=0 NormalZ=1 AngleXU=0 Radius=4 StartAngle=5e-16 EndAngle=3.14159
    g38: Circle CenterX=-10.9272 CenterY=-78.7794 CenterZ=0 NormalX=0 NormalY=0 NormalZ=1 AngleXU=0 Radius=1
    g39: Circle CenterX=-10.9272 CenterY=-82.7794 CenterZ=0 NormalX=0 NormalY=0 NormalZ=1 AngleXU=0 Radius=1
    g40: Circle CenterX=-7.42095 CenterY=-80.8542 CenterZ=0 NormalX=0 NormalY=0 NormalZ=1 AngleXU=0 Radius=1
    g41: BSplineCurve PolesCount=3 KnotsCount=2 Degree=2 IsPeriodic=0
    g42: GeomPoint X=-10.9272 Y=-78.7794 Z=0
    g43: GeomPoint X=-7.42095 Y=-80.8542 Z=0
    g44: BSplineCurve PolesCount=3 KnotsCount=2 Degree=2 IsPeriodic=0
    g45: GeomPoint X=42.5666 Y=-53.4075 Z=0
    g46: GeomPoint X=46.0728 Y=-47.4823 Z=0
    g47: BSplineCurve PolesCount=5 KnotsCount=3 Degree=3 IsPeriodic=0
    g48: LineSegment StartX=124.814 StartY=-22.1885 StartZ=0 EndX=123.265 EndY=-19.3655 EndZ=0
    g49: ArcOfCircle CenterX=116.562 CenterY=-19.6236 CenterZ=0 NormalX=0 NormalY=0 NormalZ=1 AngleXU=0 Radius=4.24264 StartAngle=1.28753 EndAngle=6.00037
    g50: LineSegment StartX=-30.9272 StartY=22.1087 StartZ=0 EndX=-34.9272 EndY=-83.7794 EndZ=0
    g51: LineSegment StartX=-22.9272 StartY=22.1087 StartZ=0 EndX=-18.9272 EndY=-83.7794 EndZ=0
    g52: LineSegment StartX=118.934 StartY=-11.4765 StartZ=0 EndX=120.377 EndY=-14.1062 EndZ=0
    g53: LineSegment StartX=118.86 StartY=-31.3104 StartZ=0 EndX=120.377 EndY=-33.1447 EndZ=0
    g54: LineSegment StartX=115.291 StartY=-37.3514 StartZ=0 EndX=117.05 EndY=-39.4781 EndZ=0
    g55: LineSegment StartX=122.136 StartY=-35.2714 StartZ=0 EndX=123.656 EndY=-37.1092 EndZ=0
    g56: BSplineCurve PolesCount=3 KnotsCount=2 Degree=2 IsPeriodic=0
    g57: LineSegment StartX=132.072 StartY=-100.779 StartZ=0 EndX=132.072 EndY=-103.779 EndZ=0
    g58: LineSegment StartX=132.072 StartY=-91.8014 StartZ=0 EndX=132.072 EndY=-94.7791 EndZ=0
    g59: LineSegment StartX=63.9135 StartY=-91.8014 StartZ=0 EndX=132.072 EndY=-91.8014 EndZ=0
    g60: LineSegment StartX=61.6457 StartY=-88.8112 StartZ=0 EndX=123.656 EndY=-37.1092 EndZ=0
    g61: LineSegment StartX=122.136 StartY=-35.2714 StartZ=0 EndX=117.05 EndY=-39.4781 EndZ=0
    g62: LineSegment StartX=115.291 StartY=-37.3514 StartZ=0 EndX=120.377 EndY=-33.1447 EndZ=0
    g63: LineSegment StartX=118.86 StartY=-31.3104 StartZ=0 EndX=61.1496 EndY=-79.2541 EndZ=0
    g64: LineSegment StartX=58.0728 StartY=-77.8102 StartZ=0 EndX=58.0728 EndY=-62.8351 EndZ=0
    g65: LineSegment StartX=61.5791 StartY=-56.9099 StartZ=0 EndX=124.814 EndY=-22.1885 EndZ=0
    g66: LineSegment StartX=120.636 StartY=-20.8076 StartZ=0 EndX=123.265 EndY=-19.3655 EndZ=0
    g67: LineSegment StartX=117.748 StartY=-15.55 StartZ=0 EndX=120.377 EndY=-14.1062 EndZ=0
    g68: LineSegment StartX=118.934 StartY=-11.4765 StartZ=0 EndX=61.5791 EndY=-42.9683 EndZ=0
    g69: LineSegment StartX=-42.9272 StartY=-103.779 StartZ=0 EndX=132.072 EndY=-103.779 EndZ=0
    g70: LineSegment StartX=42.5666 StartY=-53.4075 StartZ=0 EndX=-7.42095 EndY=-80.8542 EndZ=0
    g71: LineSegment StartX=-10.9272 StartY=-78.7794 StartZ=0 EndX=-10.9272 EndY=48.2206 EndZ=0
    g72: LineSegment StartX=2.07281 StartY=-91.7794 StartZ=0 EndX=42.0728 EndY=-91.7794 EndZ=0
    g73: LineSegment StartX=46.0728 StartY=-87.7794 StartZ=0 EndX=46.0728 EndY=-69.424 EndZ=0
    g74: LineSegment StartX=42.5666 StartY=-67.3492 StartZ=0 EndX=1.57905 EndY=-89.8542 EndZ=0
    g75: LineSegment StartX=-42.9272 StartY=-103.779 StartZ=0 EndX=-42.9272 EndY=48.2206 EndZ=0
    g76: LineSegment StartX=-17.9272 StartY=48.2206 StartZ=0 EndX=-17.9272 EndY=58.2206 EndZ=0
    g77: LineSegment StartX=-35.9272 StartY=48.2206 StartZ=0 EndX=-35.9272 EndY=52.2206 EndZ=0
    g78: LineSegment StartX=-29.9272 StartY=48.2206 StartZ=0 EndX=-29.9272 EndY=52.2206 EndZ=0
    g79: LineSegment StartX=-23.9272 StartY=48.2206 StartZ=0 EndX=-23.9272 EndY=58.2206 EndZ=0
    g80: ArcOfCircle CenterX=-32.9272 CenterY=55.2206 CenterZ=0 NormalX=0 NormalY=0 NormalZ=1 AngleXU=0 Radius=4.24264 StartAngle=5.49779 EndAngle=10.2102
    g81: ArcOfCircle CenterX=-20.9272 CenterY=61.2206 CenterZ=0 NormalX=0 NormalY=0 NormalZ=1 AngleXU=0 Radius=4.24264 StartAngle=5.49779 EndAngle=10.2102
    g82: LineSegment StartX=-17.9272 StartY=48.2206 StartZ=0 EndX=-10.9272 EndY=48.2206 EndZ=0
    g83: LineSegment StartX=-42.9272 StartY=48.2206 StartZ=0 EndX=-35.9272 EndY=48.2206 EndZ=0
    g84: LineSegment StartX=50.0728 StartY=-27.5905 StartZ=0 EndX=50.0728 EndY=-31.5905 EndZ=0
    g85: LineSegment StartX=54.0728 StartY=-27.5905 StartZ=0 EndX=54.0728 EndY=-31.5905 EndZ=0
    g86: ArcOfCircle CenterX=52.0728 CenterY=-33.5905 CenterZ=0 NormalX=0 NormalY=0 NormalZ=1 AngleXU=0 Radius=2.82843 StartAngle=2.35619 EndAngle=7.06858
    g87: LineSegment StartX=46.0728 StartY=-27.5905 StartZ=0 EndX=50.0728 EndY=-27.5905 EndZ=0
    g88: LineSegment StartX=54.0728 StartY=-27.5905 StartZ=0 EndX=58.0728 EndY=-27.5905 EndZ=0
    g89: LineSegment StartX=46.0728 StartY=-27.5905 StartZ=0 EndX=46.0728 EndY=-47.4823 EndZ=0
    g90: LineSegment StartX=58.0728 StartY=-27.5905 StartZ=0 EndX=58.0728 EndY=-40.8935 EndZ=0
    g91: LineSegment StartX=-29.9272 StartY=48.2206 StartZ=0 EndX=-23.9272 EndY=48.2206 EndZ=0
  constraints (170):
    c: Weight(g1) = 1
    c: Equal(g1,g2)
    c: Equal(g1,g3)
    c: InternalAlignment(g1,g4)
    c: InternalAlignment(g2,g4)
    c: InternalAlignment(g3,g4)
    c: InternalAlignment(g5,g4)
    c: InternalAlignment(g6,g4)
    c: Weight(g7) = 1
    c: Equal(g7,g8)
    c: Equal(g7,g9)
    c: InternalAlignment(g7,g10)
    c: InternalAlignment(g8,g10)
    c: InternalAlignment(g9,g10)
    c: InternalAlignment(g11,g10)
    c: InternalAlignment(g12,g10)
    c: Block(g4)
    c: Block(g10)
    c: Weight(g13) = 1
    c: Equal(g13,g14)
    c: Equal(g13,g15)
    c: InternalAlignment(g13,g16)
    c: InternalAlignment(g14,g16)
    c: InternalAlignment(g15,g16)
    c: InternalAlignment(g17,g16)
    c: InternalAlignment(g18,g16)
    c: Block(g16)
    c: Weight(g19) = 1
    c: Equal(g19,g20)
    c: Equal(g19,g21)
    c: InternalAlignment(g19,g22)
    c: InternalAlignment(g20,g22)
    c: InternalAlignment(g21,g22)
    c: InternalAlignment(g23,g22)
    c: InternalAlignment(g24,g22)
    c: Block(g22)
    c: Weight(g25) = 1
    c: Equal(g25,g26)
    c: Equal(g25,g27)
    c: InternalAlignment(g25,g28)
    c: InternalAlignment(g26,g28)
    c: InternalAlignment(g27,g28)
    c: InternalAlignment(g29,g28)
    c: InternalAlignment(g30,g28)
    c: Weight(g31) = 1
    c: Equal(g31,g32)
    c: Equal(g31,g33)
    c: InternalAlignment(g31,g34)
    c: InternalAlignment(g32,g34)
    c: InternalAlignment(g33,g34)
    c: InternalAlignment(g35,g34)
    c: InternalAlignment(g36,g34)
    c: Block(g34)
    c: Block(g28)
    c: Block(g37)
    c: Block(g0)
    c: Weight(g38) = 1
    c: Equal(g38,g40)
    c: InternalAlignment(g38,g41)
    c: InternalAlignment(g39,g41)
    c: InternalAlignment(g40,g41)
    c: InternalAlignment(g42,g41)
    c: InternalAlignment(g43,g41)
    c: InternalAlignment(g45,g44)
    c: InternalAlignment(g46,g44)
    c: Block(g47)
    c: Block(g44)
    c: Block(g41)
    c: Block(g48)
    c: Block(g49)
    c: Coincident(g50,g37)
    c: Coincident(g50,g0)
    c: Coincident(g51,g37)
    c: Coincident(g51,g0)
    c: Block(g51)
    c: Block(g50)
    c: Block(g52)
    c: Block(g53)
    c: Block(g54)
    c: Block(g55)
    c: Block(g56)
    c: Coincident(g57,g47)
    c: Vertical(g57)
    c: Coincident(g58,g47)
    c: Vertical(g58)
    c: Coincident(g59,g16)
    c: Coincident(g59,g58)
    c: Horizontal(g59)
    c: Coincident(g60,g16)
    c: Coincident(g60,g55)
    c: Coincident(g61,g55)
    c: Coincident(g61,g54)
    c: Coincident(g62,g54)
    c: Coincident(g62,g53)
    c: Coincident(g63,g53)
    c: Coincident(g63,g10)
    c: Coincident(g64,g10)
    c: Coincident(g64,g4)
    c: Vertical(g64)
    c: Coincident(g65,g4)
    c: Coincident(g65,g48)
    c: Coincident(g66,g49)
    c: Coincident(g66,g48)
    c: Coincident(g67,g49)
    c: Coincident(g67,g52)
    c: Coincident(g68,g52)
    c: Coincident(g68,g22)
    c: Coincident(g69,g57)
    c: Horizontal(g69)
    c: Coincident(g70,g44)
    c: Coincident(g70,g41)
    c: Coincident(g71,g41)
    c: Vertical(g71)
    c: Coincident(g72,g34)
    c: Coincident(g72,g56)
    c: Horizontal(g72)
    c: Coincident(g73,g56)
    c: Coincident(g73,g28)
    c: Vertical(g73)
    c: Coincident(g74,g28)
    c: Coincident(g74,g34)
    c: Block(g69)
    c: Coincident(g75,g69)
    c: Vertical(g75)
    c: Distance(g75) = 152
    c: Block(g71)
    c: Vertical(g76)
    c: Distance(g76) = 10
    c: Vertical(g77)
    c: Distance(g77) = 4
    c: Vertical(g78)
    c: Distance(g78) = 4
    c: Vertical(g79)
    c: Distance(g79) = 10
    c: Coincident(g80,g78)
    c: Coincident(g80,g77)
    c: Block(g80)
    c: Coincident(g81,g79)
    c: Coincident(g81,g76)
    c: Block(g81)
    c: Coincident(g82,g76)
    c: Coincident(g82,g71)
    c: Horizontal(g82)
    c: Coincident(g83,g75)
    c: Coincident(g83,g77)
    c: Horizontal(g83)
    c: Distance(g83) = 7
    c: Distance(g82) = 7
    c: Vertical(g84)
    c: Distance(g84) = 4
    c: Vertical(g85)
    c: Distance(g85) = 4
    c: Coincident(g86,g84)
    c: Coincident(g86,g85)
    c: Block(g86)
    c: Coincident(g87,g84)
    c: Horizontal(g87)
    c: Distance(g87) = 4
    c: Coincident(g88,g85)
    c: Horizontal(g88)
    c: Distance(g88) = 4
    c: Coincident(g89,g87)
    c: Coincident(g89,g44)
    c: Vertical(g89)
    c: Coincident(g90,g88)
    c: Coincident(g90,g22)
    c: Vertical(g90)
    c: Coincident(g91,g78)
    c: Coincident(g91,g79)
    c: Horizontal(g91)
FEATURE [Sketcher::SketchObject] Sketch008  label="rightSideTop"
  FullyConstrained = false
  sketch-geometry (108):
    g0: Circle CenterX=302.996 CenterY=111.695 CenterZ=0 NormalX=0 NormalY=0 NormalZ=1 AngleXU=0 Radius=1
    g1: Circle CenterX=306.073 CenterY=114.251 CenterZ=0 NormalX=0 NormalY=0 NormalZ=1 AngleXU=0 Radius=1
    g2: Circle CenterX=306.073 CenterY=110.251 CenterZ=0 NormalX=0 NormalY=0 NormalZ=1 AngleXU=0 Radius=1
    g3: BSplineCurve PolesCount=3 KnotsCount=2 Degree=2 IsPeriodic=0
    g4: GeomPoint X=302.996 Y=111.695 Z=0
    g5: GeomPoint X=306.073 Y=110.251 Z=0
    g6: Circle CenterX=306.073 CenterY=95.2763 CenterZ=0 NormalX=0 NormalY=0 NormalZ=1 AngleXU=0 Radius=1
    g7: Circle CenterX=306.073 CenterY=91.2763 CenterZ=0 NormalX=0 NormalY=0 NormalZ=1 AngleXU=0 Radius=1
    g8: Circle CenterX=302.567 CenterY=89.3511 CenterZ=0 NormalX=0 NormalY=0 NormalZ=1 AngleXU=0 Radius=1
    g9: BSplineCurve PolesCount=3 KnotsCount=2 Degree=2 IsPeriodic=0
    g10: GeomPoint X=306.073 Y=95.2763 Z=0
    g11: GeomPoint X=302.567 Y=89.3511 Z=0
    g12: LineSegment StartX=306.073 StartY=110.251 StartZ=0 EndX=306.073 EndY=95.2763 EndZ=0
    g13: Circle CenterX=302.073 CenterY=124.221 CenterZ=0 NormalX=0 NormalY=0 NormalZ=1 AngleXU=0 Radius=1
    g14: Circle CenterX=306.073 CenterY=124.221 CenterZ=0 NormalX=0 NormalY=0 NormalZ=1 AngleXU=0 Radius=1
    g15: Circle CenterX=302.996 CenterY=121.665 CenterZ=0 NormalX=0 NormalY=0 NormalZ=1 AngleXU=0 Radius=1
    g16: BSplineCurve PolesCount=3 KnotsCount=2 Degree=2 IsPeriodic=0
    g17: GeomPoint X=302.073 Y=124.221 Z=0
    g18: GeomPoint X=302.996 Y=121.665 Z=0
    g19: Circle CenterX=306.073 CenterY=73.3346 CenterZ=0 NormalX=0 NormalY=0 NormalZ=1 AngleXU=0 Radius=1
    g20: Circle CenterX=306.073 CenterY=77.3346 CenterZ=0 NormalX=0 NormalY=0 NormalZ=1 AngleXU=0 Radius=1
    g21: Circle CenterX=302.535 CenterY=75.4095 CenterZ=0 NormalX=0 NormalY=0 NormalZ=1 AngleXU=0 Radius=1
    g22: BSplineCurve PolesCount=3 KnotsCount=2 Degree=2 IsPeriodic=0
    g23: GeomPoint X=306.073 Y=73.3346 Z=0
    g24: GeomPoint X=302.535 Y=75.4095 Z=0
    g25: Circle CenterX=362.073 CenterY=124.221 CenterZ=0 NormalX=0 NormalY=0 NormalZ=1 AngleXU=0 Radius=1
    g26: Circle CenterX=366.073 CenterY=124.221 CenterZ=0 NormalX=0 NormalY=0 NormalZ=1 AngleXU=0 Radius=1
    g27: Circle CenterX=362.567 CenterY=122.294 CenterZ=0 NormalX=0 NormalY=0 NormalZ=1 AngleXU=0 Radius=1
    g28: BSplineCurve PolesCount=3 KnotsCount=2 Degree=2 IsPeriodic=0
    g29: GeomPoint X=362.073 Y=124.221 Z=0
    g30: GeomPoint X=362.567 Y=122.294 Z=0
    g31: Circle CenterX=322.073 CenterY=124.221 CenterZ=0 NormalX=0 NormalY=0 NormalZ=1 AngleXU=0 Radius=1
    g32: Circle CenterX=318.073 CenterY=124.221 CenterZ=0 NormalX=0 NormalY=0 NormalZ=1 AngleXU=0 Radius=1
    g33: Circle CenterX=318.073 CenterY=120.221 CenterZ=0 NormalX=0 NormalY=0 NormalZ=1 AngleXU=0 Radius=1
    g34: BSplineCurve PolesCount=3 KnotsCount=2 Degree=2 IsPeriodic=0
    g35: GeomPoint X=322.073 Y=124.221 Z=0
    g36: GeomPoint X=318.073 Y=120.221 Z=0
    g37: Circle CenterX=322.073 CenterY=105.865 CenterZ=0 NormalX=0 NormalY=0 NormalZ=1 AngleXU=0 Radius=1
    g38: Circle CenterX=318.073 CenterY=105.865 CenterZ=0 NormalX=0 NormalY=0 NormalZ=1 AngleXU=0 Radius=1
    g39: Circle CenterX=318.073 CenterY=109.865 CenterZ=0 NormalX=0 NormalY=0 NormalZ=1 AngleXU=0 Radius=1
    g40: BSplineCurve PolesCount=3 KnotsCount=2 Degree=2 IsPeriodic=0
    g41: GeomPoint X=322.073 Y=105.865 Z=0
    g42: GeomPoint X=318.073 Y=109.865 Z=0
    g43: Circle CenterX=336.157 CenterY=107.779 CenterZ=0 NormalX=0 NormalY=0 NormalZ=1 AngleXU=0 Radius=1
    g44: Circle CenterX=332.651 CenterY=105.853 CenterZ=0 NormalX=0 NormalY=0 NormalZ=1 AngleXU=0 Radius=1
    g45: Circle CenterX=328.643 CenterY=105.865 CenterZ=0 NormalX=0 NormalY=0 NormalZ=1 AngleXU=0 Radius=1
    g46: BSplineCurve PolesCount=3 KnotsCount=2 Degree=2 IsPeriodic=0
    g47: GeomPoint X=336.157 Y=107.779 Z=0
    g48: GeomPoint X=328.643 Y=105.865 Z=0
    g49: Circle CenterX=322.073 CenterY=76.4095 CenterZ=0 NormalX=0 NormalY=0 NormalZ=1 AngleXU=0 Radius=4
    g50: BSplineCurve PolesCount=3 KnotsCount=2 Degree=2 IsPeriodic=0
    g51: GeomPoint X=318.073 Y=72.4095 Z=0
    g52: GeomPoint X=322.073 Y=76.4095 Z=0
    g53: Circle CenterX=375.073 CenterY=72.4095 CenterZ=0 NormalX=0 NormalY=0 NormalZ=1 AngleXU=0 Radius=1
    g54: Circle CenterX=375.073 CenterY=76.4095 CenterZ=0 NormalX=0 NormalY=0 NormalZ=1 AngleXU=0 Radius=1
    g55: Circle CenterX=371.073 CenterY=76.4095 CenterZ=0 NormalX=0 NormalY=0 NormalZ=1 AngleXU=0 Radius=1
    g56: BSplineCurve PolesCount=3 KnotsCount=2 Degree=2 IsPeriodic=0
    g57: GeomPoint X=375.073 Y=72.4095 Z=0
    g58: GeomPoint X=371.073 Y=76.4095 Z=0
    g59: LineSegment StartX=322.073 StartY=76.4095 StartZ=0 EndX=371.073 EndY=76.4095 EndZ=0
    g60: Circle CenterX=232.072 CenterY=133.221 CenterZ=0 NormalX=0 NormalY=0 NormalZ=1 AngleXU=0 Radius=1
    g61: Circle CenterX=226.072 CenterY=136.221 CenterZ=0 NormalX=0 NormalY=0 NormalZ=1 AngleXU=0 Radius=1
    g62: Circle CenterX=226.072 CenterY=124.221 CenterZ=0 NormalX=0 NormalY=0 NormalZ=1 AngleXU=0 Radius=1
    g63: Circle CenterX=232.072 CenterY=127.221 CenterZ=0 NormalX=0 NormalY=0 NormalZ=1 AngleXU=0 Radius=1
    g64: BSplineCurve PolesCount=5 KnotsCount=3 Degree=3 IsPeriodic=0
    g65: GeomPoint X=232.072 Y=133.221 Z=0
    g66: GeomPoint X=223.072 Y=130.221 Z=0
    g67: GeomPoint X=232.072 Y=127.221 Z=0
    g68: LineSegment StartX=240.687 StartY=51.8263 StartZ=0 EndX=243.317 EndY=53.2701 EndZ=0
    g69: LineSegment StartX=243.575 StartY=46.5669 StartZ=0 EndX=246.205 EndY=48.0108 EndZ=0
    g70: ArcOfCircle CenterX=247.391 CenterY=52.0843 CenterZ=0 NormalX=0 NormalY=0 NormalZ=1 AngleXU=0 Radius=4.24264 StartAngle=4.42912 EndAngle=9.14151
    g71: LineSegment StartX=243.475 StartY=65.4951 StartZ=0 EndX=245.073 EndY=63.5726 EndZ=0
    g72: LineSegment StartX=243.575 StartY=46.5669 StartZ=0 EndX=245.072 EndY=43.8408 EndZ=0
    g73: LineSegment StartX=245.072 StartY=43.8408 StartZ=0 EndX=302.535 EndY=75.4095 EndZ=0
    g74: LineSegment StartX=239.192 StartY=54.5542 StartZ=0 EndX=302.567 EndY=89.3511 EndZ=0
    g75: LineSegment StartX=232.072 StartY=127.221 StartZ=0 EndX=232.072 EndY=124.221 EndZ=0
    g76: LineSegment StartX=232.072 StartY=136.221 StartZ=0 EndX=232.072 EndY=133.221 EndZ=0
    g77: LineSegment StartX=232.072 StartY=136.221 StartZ=0 EndX=407.073 EndY=136.221 EndZ=0
    g78: LineSegment StartX=322.073 StartY=124.221 StartZ=0 EndX=362.073 EndY=124.221 EndZ=0
    g79: LineSegment StartX=362.567 StartY=122.294 StartZ=0 EndX=336.157 EndY=107.779 EndZ=0
    g80: LineSegment StartX=322.073 StartY=105.865 StartZ=0 EndX=328.643 EndY=105.865 EndZ=0
    g81: LineSegment StartX=318.073 StartY=120.221 StartZ=0 EndX=318.073 EndY=109.865 EndZ=0
    g82: LineSegment StartX=232.072 StartY=124.221 StartZ=0 EndX=302.073 EndY=124.221 EndZ=0
    g83: LineSegment StartX=302.996 StartY=121.665 StartZ=0 EndX=240.171 EndY=69.471 EndZ=0
    g84: LineSegment StartX=240.171 StartY=69.471 StartZ=0 EndX=241.711 EndY=67.6177 EndZ=0
    g85: LineSegment StartX=241.711 StartY=67.6177 StartZ=0 EndX=246.787 EndY=71.8365 EndZ=0
    g86: LineSegment StartX=246.787 StartY=71.8365 StartZ=0 EndX=248.551 EndY=69.712 EndZ=0
    g87: LineSegment StartX=248.551 StartY=69.712 StartZ=0 EndX=243.475 EndY=65.4951 EndZ=0
    g88: LineSegment StartX=245.073 StartY=63.5726 StartZ=0 EndX=302.996 EndY=111.695 EndZ=0
    g89: LineSegment StartX=239.192 StartY=54.5542 StartZ=0 EndX=240.687 EndY=51.8263 EndZ=0
    g90: LineSegment StartX=375.073 StartY=48.2206 StartZ=0 EndX=382.073 EndY=48.2206 EndZ=0
    g91: LineSegment StartX=407.073 StartY=48.2206 StartZ=0 EndX=400.073 EndY=48.2206 EndZ=0
    g92: LineSegment StartX=394.073 StartY=48.2206 StartZ=0 EndX=394.073 EndY=52.2206 EndZ=0
    g93: LineSegment StartX=388.073 StartY=48.2206 StartZ=0 EndX=388.073 EndY=58.2206 EndZ=0
    g94: ArcOfCircle CenterX=385.073 CenterY=61.2206 CenterZ=0 NormalX=0 NormalY=0 NormalZ=1 AngleXU=0 Radius=4.24264 StartAngle=5.49779 EndAngle=10.2102
    g95: ArcOfCircle CenterX=397.073 CenterY=55.2206 CenterZ=0 NormalX=0 NormalY=0 NormalZ=1 AngleXU=0 Radius=4.24264 StartAngle=5.49779 EndAngle=10.2102
    g96: LineSegment StartX=382.073 StartY=58.2206 StartZ=0 EndX=382.073 EndY=48.2206 EndZ=0
    g97: LineSegment StartX=400.073 StartY=52.2206 StartZ=0 EndX=400.073 EndY=48.2206 EndZ=0
    g98: LineSegment StartX=394.073 StartY=48.2206 StartZ=0 EndX=388.073 EndY=48.2206 EndZ=0
    g99: LineSegment StartX=306.073 StartY=-27.5935 StartZ=0 EndX=310.073 EndY=-27.5935 EndZ=0
    g100: LineSegment StartX=318.073 StartY=-27.5935 StartZ=0 EndX=314.073 EndY=-27.5935 EndZ=0
    g101: LineSegment StartX=310.073 StartY=-27.5935 StartZ=0 EndX=310.073 EndY=-31.5935 EndZ=0
    g102: LineSegment StartX=314.073 StartY=-27.5935 StartZ=0 EndX=314.073 EndY=-31.5935 EndZ=0
    g103: ArcOfCircle CenterX=312.073 CenterY=-33.5935 CenterZ=0 NormalX=0 NormalY=0 NormalZ=1 AngleXU=0 Radius=2.82843 StartAngle=2.35619 EndAngle=7.06858
    g104: LineSegment StartX=375.073 StartY=72.4095 StartZ=0 EndX=375.073 EndY=48.2206 EndZ=0
    g105: LineSegment StartX=407.073 StartY=48.2206 StartZ=0 EndX=407.073 EndY=136.221 EndZ=0
    g106: LineSegment StartX=318.073 StartY=-27.5935 StartZ=0 EndX=318.073 EndY=72.4095 EndZ=0
    g107: LineSegment StartX=306.073 StartY=73.3346 StartZ=0 EndX=306.073 EndY=-27.5935 EndZ=0
  constraints (136):
    c: Weight(g0) = 1
    c: Equal(g0,g1)
    c: Equal(g0,g2)
    c: InternalAlignment(g0,g3)
    c: InternalAlignment(g1,g3)
    c: InternalAlignment(g2,g3)
    c: InternalAlignment(g4,g3)
    c: InternalAlignment(g5,g3)
    c: Weight(g6) = 1
    c: Equal(g6,g7)
    c: Equal(g6,g8)
    c: InternalAlignment(g6,g9)
    c: InternalAlignment(g7,g9)
    c: InternalAlignment(g8,g9)
    c: InternalAlignment(g10,g9)
    c: InternalAlignment(g11,g9)
    c: Block(g3)
    c: Block(g9)
    c: Coincident(g12,g3)
    c: Coincident(g12,g9)
    c: Vertical(g12)
    c: Weight(g13) = 1
    c: Equal(g13,g14)
    c: Equal(g13,g15)
    c: InternalAlignment(g14,g16)
    c: InternalAlignment(g15,g16)
    c: InternalAlignment(g17,g16)
    c: InternalAlignment(g18,g16)
    c: Block(g71)
    c: Block(g72)
    c: Coincident(g73,g72)
    c: Coincident(g73,g22)
    c: Block(g73)
    c: Coincident(g70,g69)
    c: Coincident(g70,g68)
    c: Coincident(g74,g9)
    c: Block(g74)
    c: Distance(g71) = 2.5
    c: Block(g64)
    c: Block(g46)
    c: Block(g59)
    c: Coincident(g75,g64)
    c: Vertical(g75)
    c: Coincident(g76,g64)
    c: Vertical(g76)
    c: Coincident(g77,g76)
    c: Horizontal(g77)
    c: Coincident(g78,g34)
    c: Coincident(g78,g28)
    c: Horizontal(g78)
    c: Coincident(g79,g28)
    c: Coincident(g79,g46)
    c: Coincident(g80,g40)
    c: Coincident(g80,g46)
    c: Horizontal(g80)
    c: Coincident(g81,g34)
    c: Coincident(g81,g40)
    c: Vertical(g81)
    c: Block(g34)
    c: Block(g40)
    c: Block(g28)
    c: Coincident(g82,g75)
    c: Coincident(g82,g16)
    c: Horizontal(g82)
    c: Coincident(g83,g16)
    c: Block(g82)
    c: Block(g83)
    c: Block(g16)
    c: Coincident(g84,g83)
    c: Block(g84)
    c: Coincident(g85,g84)
    c: Block(g85)
    c: Coincident(g86,g85)
    c: Coincident(g87,g86)
    c: Coincident(g87,g71)
    c: Block(g87)
    c: Coincident(g88,g71)
    c: Coincident(g88,g3)
    c: Block(g88)
    c: Coincident(g89,g74)
    c: Coincident(g89,g68)
    c: Block(g70)
    c: Block(g68)
    c: Block(g69)
    c: Block(g22)
    c: Block(g50)
    c: Block(g56)
    c: Horizontal(g90)
    c: Distance(g90) = 7
    c: Horizontal(g91)
    c: Distance(g91) = 7
    c: Vertical(g92)
    c: Distance(g92) = 4
    c: Vertical(g93)
    c: Distance(g93) = 10
    c: Coincident(g94,g93)
    c: Coincident(g95,g92)
    c: Block(g95)
    c: Block(g94)
    c: Coincident(g96,g94)
    c: Coincident(g96,g90)
    c: Vertical(g96)
    c: Coincident(g97,g95)
    c: Coincident(g97,g91)
    c: Vertical(g97)
    c: Coincident(g98,g92)
    c: Coincident(g98,g93)
    c: Horizontal(g98)
    c: Horizontal(g99)
    c: Distance(g99) = 4
    c: Horizontal(g100)
    c: Distance(g100) = 4
    c: Coincident(g101,g99)
    c: Vertical(g101)
    c: Coincident(g102,g100)
    c: Vertical(g102)
    c: Distance(g101) = 4
    c: Distance(g102) = 4
    c: Coincident(g103,g101)
    c: Coincident(g103,g102)
    c: Block(g103)
    c: Coincident(g104,g56)
    c: Coincident(g104,g90)
    c: Vertical(g104)
    c: Block(g104)
    c: Coincident(g105,g91)
    c: Coincident(g105,g77)
    c: Vertical(g105)
    c: Block(g77)
    c: Block(g105)
    c: Coincident(g106,g100)
    c: Coincident(g106,g50)
    c: Vertical(g106)
    c: Coincident(g107,g22)
    c: Coincident(g107,g99)
    c: Vertical(g107)
FEATURE [Sketcher::SketchObject] Sketch009  label="middleBottom"
  FullyConstrained = true
  sketch-geometry (109):
    g0: Circle CenterX=175.022 CenterY=5.37834 CenterZ=0 NormalX=0 NormalY=0 NormalZ=1 AngleXU=0 Radius=1
    g1: Circle CenterX=179.022 CenterY=7.57463 CenterZ=0 NormalX=0 NormalY=0 NormalZ=1 AngleXU=0 Radius=1
    g2: Circle CenterX=179.022 CenterY=5.34704 CenterZ=0 NormalX=0 NormalY=0 NormalZ=1 AngleXU=0 Radius=1
    g3: BSplineCurve PolesCount=3 KnotsCount=2 Degree=2 IsPeriodic=0
    g4: GeomPoint X=175.022 Y=5.37834 Z=0
    g5: GeomPoint X=179.022 Y=5.34704 Z=0
    g6: Circle CenterX=189.124 CenterY=5.37834 CenterZ=0 NormalX=0 NormalY=0 NormalZ=1 AngleXU=0 Radius=1
    g7: Circle CenterX=185.124 CenterY=7.57463 CenterZ=0 NormalX=0 NormalY=0 NormalZ=1 AngleXU=0 Radius=1
    g8: Circle CenterX=185.124 CenterY=5.34704 CenterZ=0 NormalX=0 NormalY=0 NormalZ=1 AngleXU=0 Radius=1
    g9: BSplineCurve PolesCount=3 KnotsCount=2 Degree=2 IsPeriodic=0
    g10: GeomPoint X=189.124 Y=5.37834 Z=0
    g11: GeomPoint X=185.124 Y=5.34704 Z=0
    g12: Circle CenterX=224.513 CenterY=-14.0532 CenterZ=0 NormalX=0 NormalY=0 NormalZ=1 AngleXU=0 Radius=1
    g13: Circle CenterX=236.584 CenterY=-24.2775 CenterZ=0 NormalX=0 NormalY=0 NormalZ=1 AngleXU=0 Radius=1
    g14: BSplineCurve PolesCount=3 KnotsCount=2 Degree=2 IsPeriodic=0
    g15: GeomPoint X=236.584 Y=-24.2775 Z=0
    g16: Circle CenterX=125.607 CenterY=-21.7539 CenterZ=0 NormalX=0 NormalY=0 NormalZ=1 AngleXU=0 Radius=1
    g17: Circle CenterX=139.632 CenterY=-14.0532 CenterZ=0 NormalX=0 NormalY=0 NormalZ=1 AngleXU=0 Radius=1
    g18: Circle CenterX=127.325 CenterY=-24.2775 CenterZ=0 NormalX=0 NormalY=0 NormalZ=1 AngleXU=0 Radius=1
    g19: BSplineCurve PolesCount=3 KnotsCount=2 Degree=2 IsPeriodic=0
    g20: GeomPoint X=125.607 Y=-21.7539 Z=0
    g21: GeomPoint X=127.325 Y=-24.2775 Z=0
    g22: Circle CenterX=179.022 CenterY=-85.8163 CenterZ=0 NormalX=0 NormalY=0 NormalZ=1 AngleXU=0 Radius=1
    g23: Circle CenterX=179.022 CenterY=-91.7794 CenterZ=0 NormalX=0 NormalY=0 NormalZ=1 AngleXU=0 Radius=1
    g24: Circle CenterX=171.895 CenterY=-91.8014 CenterZ=0 NormalX=0 NormalY=0 NormalZ=1 AngleXU=0 Radius=1
    g25: BSplineCurve PolesCount=3 KnotsCount=2 Degree=2 IsPeriodic=0
    g26: GeomPoint X=179.022 Y=-85.8163 Z=0
    g27: GeomPoint X=171.895 Y=-91.8014 Z=0
    g28: Circle CenterX=185.124 CenterY=-86.2028 CenterZ=0 NormalX=0 NormalY=0 NormalZ=1 AngleXU=0 Radius=1
    g29: Circle CenterX=185.124 CenterY=-91.7794 CenterZ=0 NormalX=0 NormalY=0 NormalZ=1 AngleXU=0 Radius=1
    g30: Circle CenterX=191.747 CenterY=-91.7794 CenterZ=0 NormalX=0 NormalY=0 NormalZ=1 AngleXU=0 Radius=1
    g31: BSplineCurve PolesCount=3 KnotsCount=2 Degree=2 IsPeriodic=0
    g32: GeomPoint X=185.124 Y=-86.2028 Z=0
    g33: GeomPoint X=191.747 Y=-91.7794 Z=0
    g34: BSplineCurve PolesCount=5 KnotsCount=3 Degree=3 IsPeriodic=0
    g35: LineSegment StartX=132.072 StartY=-100.779 StartZ=0 EndX=132.072 EndY=-103.779 EndZ=0
    g36: GeomPoint X=232.072 Y=-94.7794 Z=0
    g37: GeomPoint X=223.072 Y=-97.7794 Z=0
    g38: Circle CenterX=232.072 CenterY=-94.7794 CenterZ=0 NormalX=0 NormalY=0 NormalZ=1 AngleXU=0 Radius=1
    g39: Circle CenterX=232.072 CenterY=-100.779 CenterZ=0 NormalX=0 NormalY=0 NormalZ=1 AngleXU=0 Radius=1
    g40: BSplineCurve PolesCount=5 KnotsCount=3 Degree=3 IsPeriodic=0
    g41: GeomPoint X=232.072 Y=-100.779 Z=0
    g42: LineSegment StartX=123.656 StartY=-37.1092 StartZ=0 EndX=122.136 EndY=-35.2714 EndZ=0
    g43: LineSegment StartX=117.05 StartY=-39.4781 StartZ=0 EndX=115.291 EndY=-37.3514 EndZ=0
    g44: LineSegment StartX=120.377 StartY=-33.1447 StartZ=0 EndX=118.86 EndY=-31.3104 EndZ=0
    g45: ArcOfCircle CenterX=116.562 CenterY=-19.6236 CenterZ=0 NormalX=0 NormalY=0 NormalZ=1 AngleXU=0 Radius=4.24264 StartAngle=1.28753 EndAngle=5.99992
    g46: LineSegment StartX=240.266 StartY=-37.1092 StartZ=0 EndX=189.124 EndY=5.37834 EndZ=0
    g47: LineSegment StartX=191.747 StartY=-91.7794 StartZ=0 EndX=232.072 EndY=-91.7794 EndZ=0
    g48: LineSegment StartX=232.072 StartY=-91.7794 StartZ=0 EndX=232.072 EndY=-94.7794 EndZ=0
    g49: LineSegment StartX=232.072 StartY=-100.779 StartZ=0 EndX=232.072 EndY=-103.779 EndZ=0
    g50: LineSegment StartX=132.072 StartY=-103.779 StartZ=0 EndX=232.072 EndY=-103.779 EndZ=0
    g51: LineSegment StartX=132.072 StartY=-91.8014 StartZ=0 EndX=132.072 EndY=-94.7791 EndZ=0
    g52: LineSegment StartX=132.072 StartY=-91.8014 StartZ=0 EndX=171.895 EndY=-91.8014 EndZ=0
    g53: LineSegment StartX=179.022 StartY=-85.8163 StartZ=0 EndX=179.022 EndY=5.34704 EndZ=0
    g54: LineSegment StartX=175.022 StartY=5.37834 StartZ=0 EndX=123.656 EndY=-37.1092 EndZ=0
    g55: LineSegment StartX=185.124 StartY=5.34704 StartZ=0 EndX=185.124 EndY=-86.2028 EndZ=0
    g56: LineSegment StartX=122.136 StartY=-35.2714 StartZ=0 EndX=117.05 EndY=-39.4781 EndZ=0
    g57: LineSegment StartX=115.291 StartY=-37.3514 StartZ=0 EndX=120.377 EndY=-33.1447 EndZ=0
    g58: LineSegment StartX=118.86 StartY=-31.3104 StartZ=0 EndX=127.325 EndY=-24.2775 EndZ=0
    g59: LineSegment StartX=125.607 StartY=-21.7539 StartZ=0 EndX=124.815 EndY=-22.1887 EndZ=0
    g60: LineSegment StartX=123.265 StartY=-19.3655 StartZ=0 EndX=124.815 EndY=-22.1887 EndZ=0
    g61: LineSegment StartX=120.636 StartY=-20.8094 StartZ=0 EndX=123.265 EndY=-19.3655 EndZ=0
    g62: LineSegment StartX=117.748 StartY=-15.55 StartZ=0 EndX=120.377 EndY=-14.1062 EndZ=0
    g63: LineSegment StartX=120.377 StartY=-14.1062 StartZ=0 EndX=118.934 EndY=-11.4765 EndZ=0
    g64: LineSegment StartX=236.584 StartY=-24.2775 StartZ=0 EndX=245.072 EndY=-31.3037 EndZ=0
    g65: LineSegment StartX=245.072 StartY=-31.3037 StartZ=0 EndX=243.535 EndY=-33.1602 EndZ=0
    g66: LineSegment StartX=243.535 StartY=-33.1602 StartZ=0 EndX=248.619 EndY=-37.3688 EndZ=0
    g67: LineSegment StartX=248.619 StartY=-37.3688 StartZ=0 EndX=246.855 EndY=-39.5064 EndZ=0
    g68: LineSegment StartX=246.855 StartY=-39.5064 StartZ=0 EndX=241.778 EndY=-35.2889 EndZ=0
    g69: LineSegment StartX=241.778 StartY=-35.2889 StartZ=0 EndX=240.266 EndY=-37.1092 EndZ=0
    g70: LineSegment StartX=243.628 StartY=-14.0323 StartZ=0 EndX=246.258 EndY=-15.476 EndZ=0
    g71: LineSegment StartX=240.741 StartY=-19.2917 StartZ=0 EndX=243.37 EndY=-20.7355 EndZ=0
    g72: ArcOfCircle CenterX=247.444 CenterY=-19.5496 CenterZ=0 NormalX=0 NormalY=0 NormalZ=1 AngleXU=0 Radius=4.24264 StartAngle=3.4249 EndAngle=8.13729
    g73: LineSegment StartX=240.741 StartY=-19.2917 StartZ=0 EndX=239.201 EndY=-22.0968 EndZ=0
    g74: LineSegment StartX=238.538 StartY=-21.7516 StartZ=0 EndX=239.201 EndY=-22.0968 EndZ=0
    g75: LineSegment StartX=245.072 StartY=-11.4025 StartZ=0 EndX=243.628 EndY=-14.0323 EndZ=0
    g76-g91: Circle x16 (B-spline internal-alignment scaffolding for g92; pole/knot coordinates omitted)
    g92: BSplineCurve PolesCount=16 KnotsCount=14 Degree=3 IsPeriodic=0
    g93-g106: GeomPoint x14 (B-spline internal-alignment scaffolding for g92; pole/knot coordinates omitted)
    g107: LineSegment StartX=165.871 StartY=14.2956 StartZ=0 EndX=118.934 EndY=-11.4765 EndZ=0
    g108: LineSegment StartX=198.264 StartY=14.2963 StartZ=0 EndX=245.072 EndY=-11.4025 EndZ=0
  constraints (146):
    c: Weight(g0) = 1
    c: Equal(g0,g1)
    c: Equal(g0,g2)
    c: InternalAlignment(g0,g3)
    c: InternalAlignment(g1,g3)
    c: InternalAlignment(g2,g3)
    c: InternalAlignment(g4,g3)
    c: InternalAlignment(g5,g3)
    c: Weight(g6) = 1
    c: Equal(g6,g7)
    c: Equal(g6,g8)
    c: InternalAlignment(g6,g9)
    c: InternalAlignment(g7,g9)
    c: InternalAlignment(g8,g9)
    c: InternalAlignment(g10,g9)
    c: InternalAlignment(g11,g9)
    c: Block(g9)
    c: Block(g3)
    c: InternalAlignment(g12,g14)
    c: InternalAlignment(g13,g14)
    c: InternalAlignment(g15,g14)
    c: Block(g14)
    c: Weight(g16) = 1
    c: Equal(g16,g17)
    c: Equal(g16,g18)
    c: InternalAlignment(g16,g19)
    c: InternalAlignment(g17,g19)
    c: InternalAlignment(g18,g19)
    c: InternalAlignment(g20,g19)
    c: InternalAlignment(g21,g19)
    c: Block(g19)
    c: Weight(g22) = 1
    c: Equal(g22,g23)
    c: Equal(g22,g24)
    c: InternalAlignment(g22,g25)
    c: InternalAlignment(g23,g25)
    c: InternalAlignment(g24,g25)
    c: InternalAlignment(g26,g25)
    c: InternalAlignment(g27,g25)
    c: Weight(g28) = 1
    c: Equal(g28,g29)
    c: Equal(g28,g30)
    c: InternalAlignment(g28,g31)
    c: InternalAlignment(g29,g31)
    c: InternalAlignment(g30,g31)
    c: InternalAlignment(g32,g31)
    c: InternalAlignment(g33,g31)
    c: Block(g31)
    c: Block(g25)
    c: Block(g34)
    c: Coincident(g35,g34)
    c: Vertical(g35)
    c: Block(g35)
    c: Equal(g38,g39)
    c: InternalAlignment(g38,g40)
    c: InternalAlignment(g39,g40)
    c: InternalAlignment(g36,g40)
    c: InternalAlignment(g37,g40)
    c: InternalAlignment(g41,g40)
    c: Block(g40)
    c: Distance(g42) = 2.385
    c: Distance(g43) = 2.76
    c: Parallel(g42,g44)
    c: Block(g45)
    c: Coincident(g46,g9)
    c: Coincident(g47,g31)
    c: Horizontal(g47)
    c: Block(g47)
    c: Coincident(g48,g47)
    c: Coincident(g48,g40)
    c: Vertical(g48)
    c: Block(g48)
    c: Coincident(g49,g40)
    c: Vertical(g49)
    c: Block(g49)
    c: Coincident(g50,g35)
    c: Coincident(g50,g49)
    c: Horizontal(g50)
    c: Block(g50)
    c: Coincident(g51,g34)
    c: Vertical(g51)
    c: Coincident(g52,g51)
    c: Coincident(g52,g25)
    c: Horizontal(g52)
    c: Coincident(g53,g25)
    c: Coincident(g53,g3)
    c: Vertical(g53)
    c: Coincident(g54,g3)
    c: Coincident(g54,g42)
    c: Coincident(g55,g9)
    c: Coincident(g55,g31)
    c: Vertical(g55)
    c: Block(g42)
    c: Coincident(g56,g42)
    c: Coincident(g56,g43)
    c: Coincident(g57,g43)
    c: Coincident(g57,g44)
    c: Block(g57)
    c: Block(g56)
    c: Coincident(g58,g44)
    c: Coincident(g58,g19)
    c: Block(g58)
    c: Coincident(g59,g19)
    c: Block(g59)
    c: Coincident(g60,g59)
    c: Block(g60)
    c: Coincident(g61,g45)
    c: Coincident(g61,g60)
    c: Coincident(g62,g45)
    c: Coincident(g63,g62)
    c: Block(g63)
    c: Coincident(g64,g14)
    c: Block(g64)
    c: Coincident(g65,g64)
    c: Coincident(g66,g65)
    c: Coincident(g67,g66)
    c: Coincident(g68,g67)
    c: Coincident(g69,g68)
    c: Coincident(g69,g46)
    c: Block(g46)
    c: Block(g68)
    c: Block(g66)
    c: Distance(g70) = 3
    c: Distance(g71) = 3
    c: Coincident(g72,g70)
    c: Coincident(g72,g71)
    c: Block(g72)
    c: Coincident(g73,g71)
    c: Distance(g73) = 3.2
    c: Coincident(g74,g14)
    c: Coincident(g74,g73)
    c: Coincident(g75,g70)
    c: Block(g75)
    c: Block(g73)
    c: Distance(g63) = 3
    c: Distance(g60) = 3.22077
    c: Weight(g76) = 1
    c: Equal(g76, g77-g91) x15
    c: InternalAlignment(g76-g91 -> g92) x16
    c: InternalAlignment(g93-g106 -> g92) x14
    c: Coincident(g107,g92)
    c: Coincident(g107,g63)
    c: Block(g107)
    c: Block(g92)
    c: Coincident(g108,g92)
    c: Coincident(g108,g75)
FEATURE [Sketcher::SketchObject] Sketch010  label="legBottom"
  FullyConstrained = true
  MapMode = 4
  Placement = pos=(0,0,0) rot=(0.57735,0.57735,0.57735;2.0944rad)
  sketch-geometry (38):
    g0: BSplineCurve PolesCount=3 KnotsCount=2 Degree=2 IsPeriodic=0
    g1: Circle CenterX=-199.665 CenterY=-138.314 CenterZ=0 NormalX=0 NormalY=0 NormalZ=1 AngleXU=0 Radius=1
    g2: GeomPoint X=-199.665 Y=-138.314 Z=0
    g3: LineSegment StartX=-199.665 StartY=-138.314 StartZ=0 EndX=-200.721 EndY=-141.122 EndZ=0
    g4: Circle CenterX=-17.0256 CenterY=-190.268 CenterZ=0 NormalX=0 NormalY=0 NormalZ=1 AngleXU=0 Radius=10.5072
    g5: Circle CenterX=-37.7758 CenterY=-187.672 CenterZ=0 NormalX=0 NormalY=0 NormalZ=1 AngleXU=0 Radius=5.64388
    g6: Circle CenterX=-51.4606 CenterY=-185.091 CenterZ=0 NormalX=0 NormalY=0 NormalZ=1 AngleXU=0 Radius=3.01653
    g7: Circle CenterX=-60.4835 CenterY=-182.688 CenterZ=0 NormalX=0 NormalY=0 NormalZ=1 AngleXU=0 Radius=2.12826
    g8: Circle CenterX=-3.29005 CenterY=-177.662 CenterZ=0 NormalX=0 NormalY=0 NormalZ=1 AngleXU=0 Radius=3.26661
    g9: ArcOfCircle CenterX=11.0205 CenterY=-198.019 CenterZ=0 NormalX=0 NormalY=0 NormalZ=1 AngleXU=0 Radius=13 StartAngle=2.78068 EndAngle=5.92131
    g10: LineSegment StartX=5.08312 StartY=-176.581 StartZ=0 EndX=-1.14188 EndY=-193.429 EndZ=0
    g11: ArcOfCircle CenterX=17.2475 CenterY=-181.166 CenterZ=0 NormalX=0 NormalY=0 NormalZ=1 AngleXU=0 Radius=13 StartAngle=1.21042 EndAngle=2.78109
    g12: LineSegment StartX=38.8952 StartY=-231.233 StartZ=0 EndX=-200.721 EndY=-141.122 EndZ=0
    g13: LineSegment StartX=38.8952 StartY=-231.233 StartZ=0 EndX=39.9512 EndY=-228.425 EndZ=0
    g14: ArcOfCircle CenterX=46.9911 CenterY=-209.705 CenterZ=0 NormalX=0 NormalY=0 NormalZ=1 AngleXU=0 Radius=20 StartAngle=2.78766 EndAngle=4.35269
    g15: LineSegment StartX=23.7323 StartY=-126.969 StartZ=0 EndX=17.4091 EndY=-143.817 EndZ=0
    g16: ArcOfCircle CenterX=29.5716 CenterY=-148.408 CenterZ=0 NormalX=0 NormalY=0 NormalZ=1 AngleXU=0 Radius=13 StartAngle=2.78068 EndAngle=4.35262
    g17: ArcOfCircle CenterX=35.8967 CenterY=-131.555 CenterZ=0 NormalX=0 NormalY=0 NormalZ=1 AngleXU=0 Radius=13 StartAngle=1.21584 EndAngle=2.78109
    g18: ArcOfCircle CenterX=48.1805 CenterY=-98.7782 CenterZ=0 NormalX=0 NormalY=0 NormalZ=1 AngleXU=0 Radius=13 StartAngle=2.78068 EndAngle=4.35005
    g19: LineSegment StartX=42.354 StartY=-77.3391 StartZ=0 EndX=36.018 EndY=-94.1875 EndZ=0
    g20: ArcOfCircle CenterX=54.5183 CenterY=-81.9247 CenterZ=0 NormalX=0 NormalY=0 NormalZ=1 AngleXU=0 Radius=13 StartAngle=2.42113 EndAngle=2.78109
    g21: ArcOfCircle CenterX=20.184 CenterY=-217.506 CenterZ=0 NormalX=0 NormalY=0 NormalZ=1 AngleXU=0 Radius=3.81084 StartAngle=1.88136 EndAngle=6.80465
    g22: LineSegment StartX=38.4753 StartY=-115.966 StartZ=0 EndX=41.2852 EndY=-117.017 EndZ=0
    g23: ArcOfCircle CenterX=36.3663 CenterY=-113.042 CenterZ=0 NormalX=0 NormalY=0 NormalZ=1 AngleXU=0 Radius=3.60555 StartAngle=0.230024 EndAngle=5.3372
    g24: LineSegment StartX=39.8769 StartY=-112.22 StartZ=0 EndX=42.6867 EndY=-113.271 EndZ=0
    g25: LineSegment StartX=19.9036 StartY=-165.61 StartZ=0 EndX=22.7134 EndY=-166.661 EndZ=0
    g26: ArcOfCircle CenterX=17.7945 CenterY=-162.686 CenterZ=0 NormalX=0 NormalY=0 NormalZ=1 AngleXU=0 Radius=3.60555 StartAngle=0.230024 EndAngle=5.3372
    g27: LineSegment StartX=21.3051 StartY=-161.864 StartZ=0 EndX=24.1149 EndY=-162.915 EndZ=0
    g28: LineSegment StartX=41.085 StartY=-66.3176 StartZ=0 EndX=46.0385 EndY=-62.5254 EndZ=0
    g29: LineSegment StartX=48.9563 StartY=-66.3367 StartZ=0 EndX=44.7488 EndY=-73.3482 EndZ=0
    g30: ArcOfCircle CenterX=49.8795 CenterY=-62.6074 CenterZ=0 NormalX=0 NormalY=0 NormalZ=1 AngleXU=0 Radius=3.84187 StartAngle=4.46973 EndAngle=9.40343
    g31: LineSegment StartX=41.085 StartY=-66.3176 StartZ=0 EndX=8.65492 EndY=-152.553 EndZ=0
    g32: LineSegment StartX=43.5724 StartY=-110.934 StartZ=0 EndX=42.6867 EndY=-113.271 EndZ=0
    g33: LineSegment StartX=40.4148 StartY=-119.365 StartZ=0 EndX=41.2852 EndY=-117.017 EndZ=0
    g34: LineSegment StartX=21.8316 StartY=-169.001 StartZ=0 EndX=22.7134 EndY=-166.661 EndZ=0
    g35: LineSegment StartX=24.9948 StartY=-160.575 StartZ=0 EndX=24.1149 EndY=-162.915 EndZ=0
    g36: LineSegment StartX=23.1786 StartY=-202.622 StartZ=0 EndX=19.0195 EndY=-213.878 EndZ=0
    g37: LineSegment StartX=28.2308 StartY=-202.773 StartZ=0 EndX=23.4884 EndY=-215.608 EndZ=0
  constraints (65):
    c: Block(g9)
    c: Block(g11)
    c: InternalAlignment(g1,g0)
    c: InternalAlignment(g2,g0)
    c: Block(g0)
    c: Block(g4)
    c: Block(g8)
    c: Block(g5)
    c: Block(g6)
    c: Block(g7)
    c: Block(g14)
    c: Coincident(g13,g12)
    c: Coincident(g13,g14)
    c: Block(g13)
    c: Coincident(g3,g0)
    c: Coincident(g3,g12)
    c: Block(g12)
    c: Coincident(g10,g11)
    c: Coincident(g10,g9)
    c: Block(g16)
    c: Block(g17)
    c: Coincident(g15,g17)
    c: Coincident(g15,g16)
    c: Block(g18)
    c: Block(g20)
    c: Coincident(g19,g20)
    c: Coincident(g19,g18)
    c: Block(g21)
    c: Block(g23)
    c: Coincident(g24,g23)
    c: Coincident(g22,g23)
    c: Parallel(g24,g22)
    c: Block(g22)
    c: Block(g24)
    c: Block(g26)
    c: Coincident(g27,g26)
    c: Coincident(g25,g26)
    c: Parallel(g27,g25)
    c: Block(g25)
    c: Block(g27)
    c: Block(g28)
    c: Coincident(g30,g28)
    c: Coincident(g30,g29)
    c: Block(g30)
    c: Coincident(g31,g28)
    c: Coincident(g31,g0)
    c: Block(g29)
    c: Coincident(g32,g24)
    c: Block(g32)
    c: Coincident(g33,g22)
    c: Block(g33)
    c: Coincident(g34,g25)
    c: Coincident(g35,g27)
    c: Block(g35)
    c: Block(g34)
    c: Coincident(g36,g9)
    c: Coincident(g36,g21)
    c: Block(g36)
    c: Coincident(g11,g34)
    c: Coincident(g16,g35)
    c: Coincident(g17,g33)
    c: Coincident(g18,g32)
    c: Coincident(g20,g29)
    c: Coincident(g37,g14)
    c: Coincident(g37,g21)
